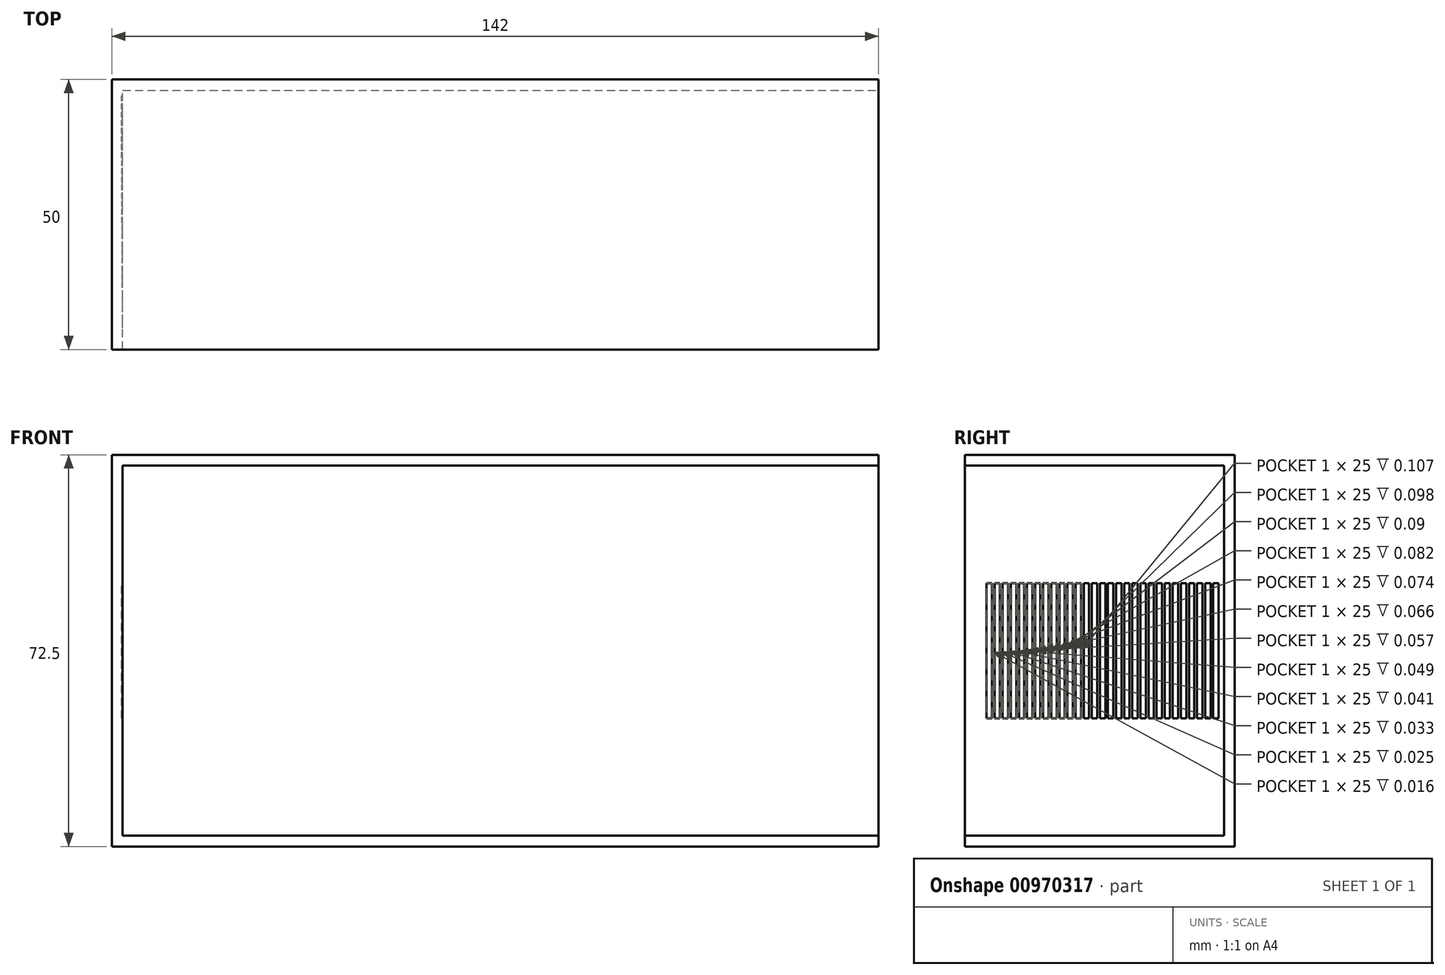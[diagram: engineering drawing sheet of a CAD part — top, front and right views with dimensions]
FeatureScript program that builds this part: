
annotation { "Feature Type Name" : "Feature", "Feature Type Description" : "" }
export const myFeature = defineFeature(function(context is Context, id is Id, definition is map)
    precondition{}
    {
        {
            var Q0;
            Q0=qCreatedBy(makeId("Front.planeOp"),FACE);
            var sketch = newSketch(context, id + "F0", { "sketchPlane" : qUnion([Q0])});
            skLineSegment(sketch, "E0.bottom", {"start": v(-71, -36.25) * mm, "end": v(71, -36.25) * mm});
            skLineSegment(sketch, "E0.top", {"start": v(-71, 36.25) * mm, "end": v(71, 36.25) * mm});
            skLineSegment(sketch, "E0.left", {"start": v(-71, -36.25) * mm, "end": v(-71, 36.25) * mm});
            skLineSegment(sketch, "E0.right", {"start": v(71, -36.25) * mm, "end": v(71, 36.25) * mm});
            skPoint(sketch, "E0.middle", {"position": v(0, 0) * mm});
            skSolve(sketch);
        }
        {
            var Q0;
            Q0=makeQuery(id+"F0.imprint","IMPRINT",FACE,{"disambiguationData":[TD([[makeQuery(id+"F0.imprint","IMPRINT",EDGE,{"derivedFrom":sQuery(id+"F0.wireOp",EDGE,"E0.bottom")}),1.0]])]});
            extrude(context, id + "F1", {"entities" : qUnion([Q0]), "depth" : 50 * mm, "offsetDistance" : 25 * mm});
        }
        {
            var Q0;
            Q0=makeQuery(id+"F1.opExtrude","SWEPT_FACE",FACE,{"disambiguationData":[OSD([sQuery(id+"F0.wireOp",EDGE,"E0.right")])]});
            shell(context, id + "F2", {"entities" : qUnion([Q0]), "thickness" : 2 * mm});
        }
        {
            var Q0;
            Q0=makeQuery(id+"F1.opExtrude","SWEPT_FACE",FACE,{"disambiguationData":[OSD([sQuery(id+"F0.wireOp",EDGE,"E0.right")])]});
            var sketch = newSketch(context, id + "F3", { "sketchPlane" : qUnion([Q0])});
            skLineSegment(sketch, "E1.0", {"start": v(-48, -34.25) * mm, "end": v(-48, 34.25) * mm});
            skLineSegment(sketch, "E2", {"start": v(-48, 34.25) * mm, "end": v(-50, 34.25) * mm});
            skLineSegment(sketch, "E3", {"start": v(-50, 34.25) * mm, "end": v(-50, -34.25) * mm});
            skLineSegment(sketch, "E4", {"start": v(-50, -34.25) * mm, "end": v(-48, -34.25) * mm});
            skSolve(sketch);
        }
        {
            var Q0;
            Q0=makeQuery(id+"F3.imprint","IMPRINT",FACE,{"disambiguationData":[TD([[makeQuery(id+"F3.imprint","IMPRINT",EDGE,{"derivedFrom":sQuery(id+"F3.wireOp",EDGE,"E1.0")}),1.0]])]});
            extrude(context, id + "F4", {"entities" : qUnion([Q0]), "operationType" : NewBodyOperationType.REMOVE, "oppositeDirection" : true, "depth" : 140 * mm, "offsetDistance" : 25 * mm});
        }
        {
            var Q0;
            Q0=qCreatedBy(makeId("Top.planeOp"),FACE);
            var sketch = newSketch(context, id + "F5", { "sketchPlane" : qUnion([Q0])});
            skLineSegment(sketch, "E5.top", {"start": v(-69, -49) * mm, "end": v(-68, -49) * mm});
            skLineSegment(sketch, "E6.bottom", {"start": v(-68, -49) * mm, "end": v(-69, -49) * mm});
            skLineSegment(sketch, "E6.top", {"start": v(-68, -48) * mm, "end": v(-69, -48) * mm});
            skLineSegment(sketch, "E6.left", {"start": v(-68, -49) * mm, "end": v(-68, -48) * mm});
            skLineSegment(sketch, "E6.right", {"start": v(-69, -49) * mm, "end": v(-69, -48) * mm});
            skLineSegment(sketch, "E7.0.1.0", {"start": v(-68, -47.5) * mm, "end": v(-69, -47.5) * mm});
            skLineSegment(sketch, "E7.0.1.1", {"start": v(-68, -46.5) * mm, "end": v(-69, -46.5) * mm});
            skLineSegment(sketch, "E7.0.1.2", {"start": v(-69, -47.5) * mm, "end": v(-68, -47.5) * mm});
            skLineSegment(sketch, "E7.0.1.3", {"start": v(-69, -47.5) * mm, "end": v(-69, -46.5) * mm});
            skLineSegment(sketch, "E7.0.1.4", {"start": v(-68, -47.5) * mm, "end": v(-68, -46.5) * mm});
            skLineSegment(sketch, "E7.0.2.0", {"start": v(-68.02, -46) * mm, "end": v(-69.02, -46) * mm});
            skLineSegment(sketch, "E7.0.2.1", {"start": v(-68.02, -45) * mm, "end": v(-69.02, -45) * mm});
            skLineSegment(sketch, "E7.0.2.2", {"start": v(-69.02, -46) * mm, "end": v(-68.02, -46) * mm});
            skLineSegment(sketch, "E7.0.2.3", {"start": v(-69.02, -46) * mm, "end": v(-69.02, -45) * mm});
            skLineSegment(sketch, "E7.0.2.4", {"start": v(-68.02, -46) * mm, "end": v(-68.02, -45) * mm});
            skLineSegment(sketch, "E7.0.3.0", {"start": v(-68.02, -44.5) * mm, "end": v(-69.02, -44.5) * mm});
            skLineSegment(sketch, "E7.0.3.1", {"start": v(-68.02, -43.5) * mm, "end": v(-69.02, -43.5) * mm});
            skLineSegment(sketch, "E7.0.3.2", {"start": v(-69.02, -44.5) * mm, "end": v(-68.02, -44.5) * mm});
            skLineSegment(sketch, "E7.0.3.3", {"start": v(-69.02, -44.5) * mm, "end": v(-69.02, -43.5) * mm});
            skLineSegment(sketch, "E7.0.3.4", {"start": v(-68.02, -44.5) * mm, "end": v(-68.02, -43.5) * mm});
            skLineSegment(sketch, "E7.0.4.0", {"start": v(-68.03, -43) * mm, "end": v(-69.03, -43) * mm});
            skLineSegment(sketch, "E7.0.4.1", {"start": v(-68.03, -42) * mm, "end": v(-69.03, -42) * mm});
            skLineSegment(sketch, "E7.0.4.2", {"start": v(-69.03, -43) * mm, "end": v(-68.03, -43) * mm});
            skLineSegment(sketch, "E7.0.4.3", {"start": v(-69.03, -43) * mm, "end": v(-69.03, -42) * mm});
            skLineSegment(sketch, "E7.0.4.4", {"start": v(-68.03, -43) * mm, "end": v(-68.03, -42) * mm});
            skLineSegment(sketch, "E7.0.5.0", {"start": v(-68.04, -41.5) * mm, "end": v(-69.04, -41.5) * mm});
            skLineSegment(sketch, "E7.0.5.1", {"start": v(-68.04, -40.5) * mm, "end": v(-69.04, -40.5) * mm});
            skLineSegment(sketch, "E7.0.5.2", {"start": v(-69.04, -41.5) * mm, "end": v(-68.04, -41.5) * mm});
            skLineSegment(sketch, "E7.0.5.3", {"start": v(-69.04, -41.5) * mm, "end": v(-69.04, -40.5) * mm});
            skLineSegment(sketch, "E7.0.5.4", {"start": v(-68.04, -41.5) * mm, "end": v(-68.04, -40.5) * mm});
            skLineSegment(sketch, "E7.0.6.0", {"start": v(-68.05, -40) * mm, "end": v(-69.05, -40) * mm});
            skLineSegment(sketch, "E7.0.6.1", {"start": v(-68.05, -39) * mm, "end": v(-69.05, -39) * mm});
            skLineSegment(sketch, "E7.0.6.2", {"start": v(-69.05, -40) * mm, "end": v(-68.05, -40) * mm});
            skLineSegment(sketch, "E7.0.6.3", {"start": v(-69.05, -40) * mm, "end": v(-69.05, -39) * mm});
            skLineSegment(sketch, "E7.0.6.4", {"start": v(-68.05, -40) * mm, "end": v(-68.05, -39) * mm});
            skLineSegment(sketch, "E7.0.7.0", {"start": v(-68.06, -38.5) * mm, "end": v(-69.06, -38.5) * mm});
            skLineSegment(sketch, "E7.0.7.1", {"start": v(-68.06, -37.5) * mm, "end": v(-69.06, -37.5) * mm});
            skLineSegment(sketch, "E7.0.7.2", {"start": v(-69.06, -38.5) * mm, "end": v(-68.06, -38.5) * mm});
            skLineSegment(sketch, "E7.0.7.3", {"start": v(-69.06, -38.5) * mm, "end": v(-69.06, -37.5) * mm});
            skLineSegment(sketch, "E7.0.7.4", {"start": v(-68.06, -38.5) * mm, "end": v(-68.06, -37.5) * mm});
            skLineSegment(sketch, "E7.0.8.0", {"start": v(-68.07, -37) * mm, "end": v(-69.07, -37) * mm});
            skLineSegment(sketch, "E7.0.8.1", {"start": v(-68.07, -36) * mm, "end": v(-69.07, -36) * mm});
            skLineSegment(sketch, "E7.0.8.2", {"start": v(-69.07, -37) * mm, "end": v(-68.07, -37) * mm});
            skLineSegment(sketch, "E7.0.8.3", {"start": v(-69.07, -37) * mm, "end": v(-69.07, -36) * mm});
            skLineSegment(sketch, "E7.0.8.4", {"start": v(-68.07, -37) * mm, "end": v(-68.07, -36) * mm});
            skLineSegment(sketch, "E7.0.9.0", {"start": v(-68.07, -35.5) * mm, "end": v(-69.07, -35.5) * mm});
            skLineSegment(sketch, "E7.0.9.1", {"start": v(-68.07, -34.5) * mm, "end": v(-69.07, -34.5) * mm});
            skLineSegment(sketch, "E7.0.9.2", {"start": v(-69.07, -35.5) * mm, "end": v(-68.07, -35.5) * mm});
            skLineSegment(sketch, "E7.0.9.3", {"start": v(-69.07, -35.5) * mm, "end": v(-69.07, -34.5) * mm});
            skLineSegment(sketch, "E7.0.9.4", {"start": v(-68.07, -35.5) * mm, "end": v(-68.07, -34.5) * mm});
            skLineSegment(sketch, "E7.0.10.0", {"start": v(-68.08, -34) * mm, "end": v(-69.08, -34) * mm});
            skLineSegment(sketch, "E7.0.10.1", {"start": v(-68.08, -33) * mm, "end": v(-69.08, -33) * mm});
            skLineSegment(sketch, "E7.0.10.2", {"start": v(-69.08, -34) * mm, "end": v(-68.08, -34) * mm});
            skLineSegment(sketch, "E7.0.10.3", {"start": v(-69.08, -34) * mm, "end": v(-69.08, -33) * mm});
            skLineSegment(sketch, "E7.0.10.4", {"start": v(-68.08, -34) * mm, "end": v(-68.08, -33) * mm});
            skLineSegment(sketch, "E7.0.11.0", {"start": v(-68.1, -32.5) * mm, "end": v(-69.1, -32.5) * mm});
            skLineSegment(sketch, "E7.0.11.1", {"start": v(-68.1, -31.5) * mm, "end": v(-69.1, -31.5) * mm});
            skLineSegment(sketch, "E7.0.11.2", {"start": v(-69.1, -32.5) * mm, "end": v(-68.1, -32.5) * mm});
            skLineSegment(sketch, "E7.0.11.3", {"start": v(-69.1, -32.5) * mm, "end": v(-69.1, -31.5) * mm});
            skLineSegment(sketch, "E7.0.11.4", {"start": v(-68.1, -32.5) * mm, "end": v(-68.1, -31.5) * mm});
            skLineSegment(sketch, "E7.0.12.0", {"start": v(-68.1, -31) * mm, "end": v(-69.1, -31) * mm});
            skLineSegment(sketch, "E7.0.12.1", {"start": v(-68.1, -30) * mm, "end": v(-69.1, -30) * mm});
            skLineSegment(sketch, "E7.0.12.2", {"start": v(-69.1, -31) * mm, "end": v(-68.1, -31) * mm});
            skLineSegment(sketch, "E7.0.12.3", {"start": v(-69.1, -31) * mm, "end": v(-69.1, -30) * mm});
            skLineSegment(sketch, "E7.0.12.4", {"start": v(-68.1, -31) * mm, "end": v(-68.1, -30) * mm});
            skLineSegment(sketch, "E7.0.13.0", {"start": v(-68.1, -29.5) * mm, "end": v(-69.1, -29.5) * mm});
            skLineSegment(sketch, "E7.0.13.1", {"start": v(-68.1, -28.5) * mm, "end": v(-69.1, -28.5) * mm});
            skLineSegment(sketch, "E7.0.13.2", {"start": v(-69.1, -29.5) * mm, "end": v(-68.1, -29.5) * mm});
            skLineSegment(sketch, "E7.0.13.3", {"start": v(-69.1, -29.5) * mm, "end": v(-69.1, -28.5) * mm});
            skLineSegment(sketch, "E7.0.13.4", {"start": v(-68.1, -29.5) * mm, "end": v(-68.1, -28.5) * mm});
            skLineSegment(sketch, "E7.0.14.0", {"start": v(-68.11, -28) * mm, "end": v(-69.11, -28) * mm});
            skLineSegment(sketch, "E7.0.14.1", {"start": v(-68.11, -27) * mm, "end": v(-69.11, -27) * mm});
            skLineSegment(sketch, "E7.0.14.2", {"start": v(-69.11, -28) * mm, "end": v(-68.11, -28) * mm});
            skLineSegment(sketch, "E7.0.14.3", {"start": v(-69.11, -28) * mm, "end": v(-69.11, -27) * mm});
            skLineSegment(sketch, "E7.0.14.4", {"start": v(-68.11, -28) * mm, "end": v(-68.11, -27) * mm});
            skLineSegment(sketch, "E7.0.15.0", {"start": v(-68.12, -26.5) * mm, "end": v(-69.12, -26.5) * mm});
            skLineSegment(sketch, "E7.0.15.1", {"start": v(-68.12, -25.5) * mm, "end": v(-69.12, -25.5) * mm});
            skLineSegment(sketch, "E7.0.15.2", {"start": v(-69.12, -26.5) * mm, "end": v(-68.12, -26.5) * mm});
            skLineSegment(sketch, "E7.0.15.3", {"start": v(-69.12, -26.5) * mm, "end": v(-69.12, -25.5) * mm});
            skLineSegment(sketch, "E7.0.15.4", {"start": v(-68.12, -26.5) * mm, "end": v(-68.12, -25.5) * mm});
            skLineSegment(sketch, "E7.0.16.0", {"start": v(-68.13, -25) * mm, "end": v(-69.13, -25) * mm});
            skLineSegment(sketch, "E7.0.16.1", {"start": v(-68.13, -24) * mm, "end": v(-69.13, -24) * mm});
            skLineSegment(sketch, "E7.0.16.2", {"start": v(-69.13, -25) * mm, "end": v(-68.13, -25) * mm});
            skLineSegment(sketch, "E7.0.16.3", {"start": v(-69.13, -25) * mm, "end": v(-69.13, -24) * mm});
            skLineSegment(sketch, "E7.0.16.4", {"start": v(-68.13, -25) * mm, "end": v(-68.13, -24) * mm});
            skLineSegment(sketch, "E7.0.17.0", {"start": v(-68.14, -23.5) * mm, "end": v(-69.14, -23.5) * mm});
            skLineSegment(sketch, "E7.0.17.1", {"start": v(-68.14, -22.5) * mm, "end": v(-69.14, -22.5) * mm});
            skLineSegment(sketch, "E7.0.17.2", {"start": v(-69.14, -23.5) * mm, "end": v(-68.14, -23.5) * mm});
            skLineSegment(sketch, "E7.0.17.3", {"start": v(-69.14, -23.5) * mm, "end": v(-69.14, -22.5) * mm});
            skLineSegment(sketch, "E7.0.17.4", {"start": v(-68.14, -23.5) * mm, "end": v(-68.14, -22.5) * mm});
            skLineSegment(sketch, "E7.0.18.0", {"start": v(-68.15, -22) * mm, "end": v(-69.15, -22) * mm});
            skLineSegment(sketch, "E7.0.18.1", {"start": v(-68.15, -21) * mm, "end": v(-69.15, -21) * mm});
            skLineSegment(sketch, "E7.0.18.2", {"start": v(-69.15, -22) * mm, "end": v(-68.15, -22) * mm});
            skLineSegment(sketch, "E7.0.18.3", {"start": v(-69.15, -22) * mm, "end": v(-69.15, -21) * mm});
            skLineSegment(sketch, "E7.0.18.4", {"start": v(-68.15, -22) * mm, "end": v(-68.15, -21) * mm});
            skLineSegment(sketch, "E7.0.19.0", {"start": v(-68.16, -20.5) * mm, "end": v(-69.16, -20.5) * mm});
            skLineSegment(sketch, "E7.0.19.1", {"start": v(-68.16, -19.5) * mm, "end": v(-69.16, -19.5) * mm});
            skLineSegment(sketch, "E7.0.19.2", {"start": v(-69.16, -20.5) * mm, "end": v(-68.16, -20.5) * mm});
            skLineSegment(sketch, "E7.0.19.3", {"start": v(-69.16, -20.5) * mm, "end": v(-69.16, -19.5) * mm});
            skLineSegment(sketch, "E7.0.19.4", {"start": v(-68.16, -20.5) * mm, "end": v(-68.16, -19.5) * mm});
            skLineSegment(sketch, "E7.0.20.0", {"start": v(-68.16, -19) * mm, "end": v(-69.16, -19) * mm});
            skLineSegment(sketch, "E7.0.20.1", {"start": v(-68.16, -18) * mm, "end": v(-69.16, -18) * mm});
            skLineSegment(sketch, "E7.0.20.2", {"start": v(-69.16, -19) * mm, "end": v(-68.16, -19) * mm});
            skLineSegment(sketch, "E7.0.20.3", {"start": v(-69.16, -19) * mm, "end": v(-69.16, -18) * mm});
            skLineSegment(sketch, "E7.0.20.4", {"start": v(-68.16, -19) * mm, "end": v(-68.16, -18) * mm});
            skLineSegment(sketch, "E7.0.21.0", {"start": v(-68.17, -17.5) * mm, "end": v(-69.17, -17.5) * mm});
            skLineSegment(sketch, "E7.0.21.1", {"start": v(-68.17, -16.5) * mm, "end": v(-69.17, -16.5) * mm});
            skLineSegment(sketch, "E7.0.21.2", {"start": v(-69.17, -17.5) * mm, "end": v(-68.17, -17.5) * mm});
            skLineSegment(sketch, "E7.0.21.3", {"start": v(-69.17, -17.5) * mm, "end": v(-69.17, -16.5) * mm});
            skLineSegment(sketch, "E7.0.21.4", {"start": v(-68.17, -17.5) * mm, "end": v(-68.17, -16.5) * mm});
            skLineSegment(sketch, "E7.0.22.0", {"start": v(-68.18, -16) * mm, "end": v(-69.18, -16) * mm});
            skLineSegment(sketch, "E7.0.22.1", {"start": v(-68.18, -15) * mm, "end": v(-69.18, -15) * mm});
            skLineSegment(sketch, "E7.0.22.2", {"start": v(-69.18, -16) * mm, "end": v(-68.18, -16) * mm});
            skLineSegment(sketch, "E7.0.22.3", {"start": v(-69.18, -16) * mm, "end": v(-69.18, -15) * mm});
            skLineSegment(sketch, "E7.0.22.4", {"start": v(-68.18, -16) * mm, "end": v(-68.18, -15) * mm});
            skLineSegment(sketch, "E7.0.23.0", {"start": v(-68.19, -14.5) * mm, "end": v(-69.19, -14.5) * mm});
            skLineSegment(sketch, "E7.0.23.1", {"start": v(-68.19, -13.5) * mm, "end": v(-69.19, -13.5) * mm});
            skLineSegment(sketch, "E7.0.23.2", {"start": v(-69.19, -14.5) * mm, "end": v(-68.19, -14.5) * mm});
            skLineSegment(sketch, "E7.0.23.3", {"start": v(-69.19, -14.5) * mm, "end": v(-69.19, -13.5) * mm});
            skLineSegment(sketch, "E7.0.23.4", {"start": v(-68.19, -14.5) * mm, "end": v(-68.19, -13.5) * mm});
            skLineSegment(sketch, "E7.0.24.0", {"start": v(-68.2, -13) * mm, "end": v(-69.2, -13) * mm});
            skLineSegment(sketch, "E7.0.24.1", {"start": v(-68.2, -12) * mm, "end": v(-69.2, -12) * mm});
            skLineSegment(sketch, "E7.0.24.2", {"start": v(-69.2, -13) * mm, "end": v(-68.2, -13) * mm});
            skLineSegment(sketch, "E7.0.24.3", {"start": v(-69.2, -13) * mm, "end": v(-69.2, -12) * mm});
            skLineSegment(sketch, "E7.0.24.4", {"start": v(-68.2, -13) * mm, "end": v(-68.2, -12) * mm});
            skLineSegment(sketch, "E7.0.25.0", {"start": v(-68.2, -11.5) * mm, "end": v(-69.2, -11.5) * mm});
            skLineSegment(sketch, "E7.0.25.1", {"start": v(-68.2, -10.5) * mm, "end": v(-69.2, -10.5) * mm});
            skLineSegment(sketch, "E7.0.25.2", {"start": v(-69.2, -11.5) * mm, "end": v(-68.2, -11.5) * mm});
            skLineSegment(sketch, "E7.0.25.3", {"start": v(-69.2, -11.5) * mm, "end": v(-69.2, -10.5) * mm});
            skLineSegment(sketch, "E7.0.25.4", {"start": v(-68.2, -11.5) * mm, "end": v(-68.2, -10.5) * mm});
            skLineSegment(sketch, "E7.0.26.0", {"start": v(-68.21, -10) * mm, "end": v(-69.21, -10) * mm});
            skLineSegment(sketch, "E7.0.26.1", {"start": v(-68.21, -9) * mm, "end": v(-69.21, -9) * mm});
            skLineSegment(sketch, "E7.0.26.2", {"start": v(-69.21, -10) * mm, "end": v(-68.21, -10) * mm});
            skLineSegment(sketch, "E7.0.26.3", {"start": v(-69.21, -10) * mm, "end": v(-69.21, -9) * mm});
            skLineSegment(sketch, "E7.0.26.4", {"start": v(-68.21, -10) * mm, "end": v(-68.21, -9) * mm});
            skLineSegment(sketch, "E7.0.27.0", {"start": v(-68.22, -8.5) * mm, "end": v(-69.22, -8.5) * mm});
            skLineSegment(sketch, "E7.0.27.1", {"start": v(-68.22, -7.5) * mm, "end": v(-69.22, -7.5) * mm});
            skLineSegment(sketch, "E7.0.27.2", {"start": v(-69.22, -8.5) * mm, "end": v(-68.22, -8.5) * mm});
            skLineSegment(sketch, "E7.0.27.3", {"start": v(-69.22, -8.5) * mm, "end": v(-69.22, -7.5) * mm});
            skLineSegment(sketch, "E7.0.27.4", {"start": v(-68.22, -8.5) * mm, "end": v(-68.22, -7.5) * mm});
            skLineSegment(sketch, "E7.0.28.0", {"start": v(-68.23, -7) * mm, "end": v(-69.23, -7) * mm});
            skLineSegment(sketch, "E7.0.28.1", {"start": v(-68.23, -6) * mm, "end": v(-69.23, -6) * mm});
            skLineSegment(sketch, "E7.0.28.2", {"start": v(-69.23, -7) * mm, "end": v(-68.23, -7) * mm});
            skLineSegment(sketch, "E7.0.28.3", {"start": v(-69.23, -7) * mm, "end": v(-69.23, -6) * mm});
            skLineSegment(sketch, "E7.0.28.4", {"start": v(-68.23, -7) * mm, "end": v(-68.23, -6) * mm});
            skLineSegment(sketch, "E7.0.29.0", {"start": v(-68.24, -5.5) * mm, "end": v(-69.24, -5.5) * mm});
            skLineSegment(sketch, "E7.0.29.1", {"start": v(-68.24, -4.5) * mm, "end": v(-69.24, -4.5) * mm});
            skLineSegment(sketch, "E7.0.29.2", {"start": v(-69.24, -5.5) * mm, "end": v(-68.24, -5.5) * mm});
            skLineSegment(sketch, "E7.0.29.3", {"start": v(-69.24, -5.5) * mm, "end": v(-69.24, -4.5) * mm});
            skLineSegment(sketch, "E7.0.29.4", {"start": v(-68.24, -5.5) * mm, "end": v(-68.24, -4.5) * mm});
            skLineSegment(sketch, "E7.0.30.0", {"start": v(-68.25, -4) * mm, "end": v(-69.25, -4) * mm});
            skLineSegment(sketch, "E7.0.30.1", {"start": v(-68.25, -3) * mm, "end": v(-69.25, -3) * mm});
            skLineSegment(sketch, "E7.0.30.2", {"start": v(-69.25, -4) * mm, "end": v(-68.25, -4) * mm});
            skLineSegment(sketch, "E7.0.30.3", {"start": v(-69.25, -4) * mm, "end": v(-69.25, -3) * mm});
            skLineSegment(sketch, "E7.0.30.4", {"start": v(-68.25, -4) * mm, "end": v(-68.25, -3) * mm});
            skLineSegment(sketch, "E7.1.0.0", {"start": v(-66.5, -49) * mm, "end": v(-67.5, -49) * mm});
            skLineSegment(sketch, "E7.1.0.1", {"start": v(-66.5, -48) * mm, "end": v(-67.5, -48) * mm});
            skLineSegment(sketch, "E7.1.0.2", {"start": v(-67.5, -49) * mm, "end": v(-66.5, -49) * mm});
            skLineSegment(sketch, "E7.1.0.3", {"start": v(-67.5, -49) * mm, "end": v(-67.5, -48) * mm});
            skLineSegment(sketch, "E7.1.0.4", {"start": v(-66.5, -49) * mm, "end": v(-66.5, -48) * mm});
            skLineSegment(sketch, "E7.1.1.0", {"start": v(-66.5, -47.5) * mm, "end": v(-67.5, -47.5) * mm});
            skLineSegment(sketch, "E7.1.1.1", {"start": v(-66.5, -46.5) * mm, "end": v(-67.5, -46.5) * mm});
            skLineSegment(sketch, "E7.1.1.2", {"start": v(-67.5, -47.5) * mm, "end": v(-66.5, -47.5) * mm});
            skLineSegment(sketch, "E7.1.1.3", {"start": v(-67.5, -47.5) * mm, "end": v(-67.5, -46.5) * mm});
            skLineSegment(sketch, "E7.1.1.4", {"start": v(-66.5, -47.5) * mm, "end": v(-66.5, -46.5) * mm});
            skLineSegment(sketch, "E7.1.2.0", {"start": v(-66.52, -46) * mm, "end": v(-67.52, -46) * mm});
            skLineSegment(sketch, "E7.1.2.1", {"start": v(-66.52, -45) * mm, "end": v(-67.52, -45) * mm});
            skLineSegment(sketch, "E7.1.2.2", {"start": v(-67.52, -46) * mm, "end": v(-66.52, -46) * mm});
            skLineSegment(sketch, "E7.1.2.3", {"start": v(-67.52, -46) * mm, "end": v(-67.52, -45) * mm});
            skLineSegment(sketch, "E7.1.2.4", {"start": v(-66.52, -46) * mm, "end": v(-66.52, -45) * mm});
            skLineSegment(sketch, "E7.1.3.0", {"start": v(-66.52, -44.5) * mm, "end": v(-67.52, -44.5) * mm});
            skLineSegment(sketch, "E7.1.3.1", {"start": v(-66.52, -43.5) * mm, "end": v(-67.52, -43.5) * mm});
            skLineSegment(sketch, "E7.1.3.2", {"start": v(-67.52, -44.5) * mm, "end": v(-66.52, -44.5) * mm});
            skLineSegment(sketch, "E7.1.3.3", {"start": v(-67.52, -44.5) * mm, "end": v(-67.52, -43.5) * mm});
            skLineSegment(sketch, "E7.1.3.4", {"start": v(-66.52, -44.5) * mm, "end": v(-66.52, -43.5) * mm});
            skLineSegment(sketch, "E7.1.4.0", {"start": v(-66.53, -43) * mm, "end": v(-67.53, -43) * mm});
            skLineSegment(sketch, "E7.1.4.1", {"start": v(-66.53, -42) * mm, "end": v(-67.53, -42) * mm});
            skLineSegment(sketch, "E7.1.4.2", {"start": v(-67.53, -43) * mm, "end": v(-66.53, -43) * mm});
            skLineSegment(sketch, "E7.1.4.3", {"start": v(-67.53, -43) * mm, "end": v(-67.53, -42) * mm});
            skLineSegment(sketch, "E7.1.4.4", {"start": v(-66.53, -43) * mm, "end": v(-66.53, -42) * mm});
            skLineSegment(sketch, "E7.1.5.0", {"start": v(-66.54, -41.5) * mm, "end": v(-67.54, -41.5) * mm});
            skLineSegment(sketch, "E7.1.5.1", {"start": v(-66.54, -40.5) * mm, "end": v(-67.54, -40.5) * mm});
            skLineSegment(sketch, "E7.1.5.2", {"start": v(-67.54, -41.5) * mm, "end": v(-66.54, -41.5) * mm});
            skLineSegment(sketch, "E7.1.5.3", {"start": v(-67.54, -41.5) * mm, "end": v(-67.54, -40.5) * mm});
            skLineSegment(sketch, "E7.1.5.4", {"start": v(-66.54, -41.5) * mm, "end": v(-66.54, -40.5) * mm});
            skLineSegment(sketch, "E7.1.6.0", {"start": v(-66.55, -40) * mm, "end": v(-67.55, -40) * mm});
            skLineSegment(sketch, "E7.1.6.1", {"start": v(-66.55, -39) * mm, "end": v(-67.55, -39) * mm});
            skLineSegment(sketch, "E7.1.6.2", {"start": v(-67.55, -40) * mm, "end": v(-66.55, -40) * mm});
            skLineSegment(sketch, "E7.1.6.3", {"start": v(-67.55, -40) * mm, "end": v(-67.55, -39) * mm});
            skLineSegment(sketch, "E7.1.6.4", {"start": v(-66.55, -40) * mm, "end": v(-66.55, -39) * mm});
            skLineSegment(sketch, "E7.1.7.0", {"start": v(-66.56, -38.5) * mm, "end": v(-67.56, -38.5) * mm});
            skLineSegment(sketch, "E7.1.7.1", {"start": v(-66.56, -37.5) * mm, "end": v(-67.56, -37.5) * mm});
            skLineSegment(sketch, "E7.1.7.2", {"start": v(-67.56, -38.5) * mm, "end": v(-66.56, -38.5) * mm});
            skLineSegment(sketch, "E7.1.7.3", {"start": v(-67.56, -38.5) * mm, "end": v(-67.56, -37.5) * mm});
            skLineSegment(sketch, "E7.1.7.4", {"start": v(-66.56, -38.5) * mm, "end": v(-66.56, -37.5) * mm});
            skLineSegment(sketch, "E7.1.8.0", {"start": v(-66.57, -37) * mm, "end": v(-67.57, -37) * mm});
            skLineSegment(sketch, "E7.1.8.1", {"start": v(-66.57, -36) * mm, "end": v(-67.57, -36) * mm});
            skLineSegment(sketch, "E7.1.8.2", {"start": v(-67.57, -37) * mm, "end": v(-66.57, -37) * mm});
            skLineSegment(sketch, "E7.1.8.3", {"start": v(-67.57, -37) * mm, "end": v(-67.57, -36) * mm});
            skLineSegment(sketch, "E7.1.8.4", {"start": v(-66.57, -37) * mm, "end": v(-66.57, -36) * mm});
            skLineSegment(sketch, "E7.1.9.0", {"start": v(-66.57, -35.5) * mm, "end": v(-67.57, -35.5) * mm});
            skLineSegment(sketch, "E7.1.9.1", {"start": v(-66.57, -34.5) * mm, "end": v(-67.57, -34.5) * mm});
            skLineSegment(sketch, "E7.1.9.2", {"start": v(-67.57, -35.5) * mm, "end": v(-66.57, -35.5) * mm});
            skLineSegment(sketch, "E7.1.9.3", {"start": v(-67.57, -35.5) * mm, "end": v(-67.57, -34.5) * mm});
            skLineSegment(sketch, "E7.1.9.4", {"start": v(-66.57, -35.5) * mm, "end": v(-66.57, -34.5) * mm});
            skLineSegment(sketch, "E7.1.10.0", {"start": v(-66.58, -34) * mm, "end": v(-67.58, -34) * mm});
            skLineSegment(sketch, "E7.1.10.1", {"start": v(-66.58, -33) * mm, "end": v(-67.58, -33) * mm});
            skLineSegment(sketch, "E7.1.10.2", {"start": v(-67.58, -34) * mm, "end": v(-66.58, -34) * mm});
            skLineSegment(sketch, "E7.1.10.3", {"start": v(-67.58, -34) * mm, "end": v(-67.58, -33) * mm});
            skLineSegment(sketch, "E7.1.10.4", {"start": v(-66.58, -34) * mm, "end": v(-66.58, -33) * mm});
            skLineSegment(sketch, "E7.1.11.0", {"start": v(-66.6, -32.5) * mm, "end": v(-67.6, -32.5) * mm});
            skLineSegment(sketch, "E7.1.11.1", {"start": v(-66.6, -31.5) * mm, "end": v(-67.6, -31.5) * mm});
            skLineSegment(sketch, "E7.1.11.2", {"start": v(-67.6, -32.5) * mm, "end": v(-66.6, -32.5) * mm});
            skLineSegment(sketch, "E7.1.11.3", {"start": v(-67.6, -32.5) * mm, "end": v(-67.6, -31.5) * mm});
            skLineSegment(sketch, "E7.1.11.4", {"start": v(-66.6, -32.5) * mm, "end": v(-66.6, -31.5) * mm});
            skLineSegment(sketch, "E7.1.12.0", {"start": v(-66.6, -31) * mm, "end": v(-67.6, -31) * mm});
            skLineSegment(sketch, "E7.1.12.1", {"start": v(-66.6, -30) * mm, "end": v(-67.6, -30) * mm});
            skLineSegment(sketch, "E7.1.12.2", {"start": v(-67.6, -31) * mm, "end": v(-66.6, -31) * mm});
            skLineSegment(sketch, "E7.1.12.3", {"start": v(-67.6, -31) * mm, "end": v(-67.6, -30) * mm});
            skLineSegment(sketch, "E7.1.12.4", {"start": v(-66.6, -31) * mm, "end": v(-66.6, -30) * mm});
            skLineSegment(sketch, "E7.1.13.0", {"start": v(-66.6, -29.5) * mm, "end": v(-67.6, -29.5) * mm});
            skLineSegment(sketch, "E7.1.13.1", {"start": v(-66.6, -28.5) * mm, "end": v(-67.6, -28.5) * mm});
            skLineSegment(sketch, "E7.1.13.2", {"start": v(-67.6, -29.5) * mm, "end": v(-66.6, -29.5) * mm});
            skLineSegment(sketch, "E7.1.13.3", {"start": v(-67.6, -29.5) * mm, "end": v(-67.6, -28.5) * mm});
            skLineSegment(sketch, "E7.1.13.4", {"start": v(-66.6, -29.5) * mm, "end": v(-66.6, -28.5) * mm});
            skLineSegment(sketch, "E7.1.14.0", {"start": v(-66.61, -28) * mm, "end": v(-67.61, -28) * mm});
            skLineSegment(sketch, "E7.1.14.1", {"start": v(-66.61, -27) * mm, "end": v(-67.61, -27) * mm});
            skLineSegment(sketch, "E7.1.14.2", {"start": v(-67.61, -28) * mm, "end": v(-66.61, -28) * mm});
            skLineSegment(sketch, "E7.1.14.3", {"start": v(-67.61, -28) * mm, "end": v(-67.61, -27) * mm});
            skLineSegment(sketch, "E7.1.14.4", {"start": v(-66.61, -28) * mm, "end": v(-66.61, -27) * mm});
            skLineSegment(sketch, "E7.1.15.0", {"start": v(-66.62, -26.5) * mm, "end": v(-67.62, -26.5) * mm});
            skLineSegment(sketch, "E7.1.15.1", {"start": v(-66.62, -25.5) * mm, "end": v(-67.62, -25.5) * mm});
            skLineSegment(sketch, "E7.1.15.2", {"start": v(-67.62, -26.5) * mm, "end": v(-66.62, -26.5) * mm});
            skLineSegment(sketch, "E7.1.15.3", {"start": v(-67.62, -26.5) * mm, "end": v(-67.62, -25.5) * mm});
            skLineSegment(sketch, "E7.1.15.4", {"start": v(-66.62, -26.5) * mm, "end": v(-66.62, -25.5) * mm});
            skLineSegment(sketch, "E7.1.16.0", {"start": v(-66.63, -25) * mm, "end": v(-67.63, -25) * mm});
            skLineSegment(sketch, "E7.1.16.1", {"start": v(-66.63, -24) * mm, "end": v(-67.63, -24) * mm});
            skLineSegment(sketch, "E7.1.16.2", {"start": v(-67.63, -25) * mm, "end": v(-66.63, -25) * mm});
            skLineSegment(sketch, "E7.1.16.3", {"start": v(-67.63, -25) * mm, "end": v(-67.63, -24) * mm});
            skLineSegment(sketch, "E7.1.16.4", {"start": v(-66.63, -25) * mm, "end": v(-66.63, -24) * mm});
            skLineSegment(sketch, "E7.1.17.0", {"start": v(-66.64, -23.5) * mm, "end": v(-67.64, -23.5) * mm});
            skLineSegment(sketch, "E7.1.17.1", {"start": v(-66.64, -22.5) * mm, "end": v(-67.64, -22.5) * mm});
            skLineSegment(sketch, "E7.1.17.2", {"start": v(-67.64, -23.5) * mm, "end": v(-66.64, -23.5) * mm});
            skLineSegment(sketch, "E7.1.17.3", {"start": v(-67.64, -23.5) * mm, "end": v(-67.64, -22.5) * mm});
            skLineSegment(sketch, "E7.1.17.4", {"start": v(-66.64, -23.5) * mm, "end": v(-66.64, -22.5) * mm});
            skLineSegment(sketch, "E7.1.18.0", {"start": v(-66.65, -22) * mm, "end": v(-67.65, -22) * mm});
            skLineSegment(sketch, "E7.1.18.1", {"start": v(-66.65, -21) * mm, "end": v(-67.65, -21) * mm});
            skLineSegment(sketch, "E7.1.18.2", {"start": v(-67.65, -22) * mm, "end": v(-66.65, -22) * mm});
            skLineSegment(sketch, "E7.1.18.3", {"start": v(-67.65, -22) * mm, "end": v(-67.65, -21) * mm});
            skLineSegment(sketch, "E7.1.18.4", {"start": v(-66.65, -22) * mm, "end": v(-66.65, -21) * mm});
            skLineSegment(sketch, "E7.1.19.0", {"start": v(-66.66, -20.5) * mm, "end": v(-67.66, -20.5) * mm});
            skLineSegment(sketch, "E7.1.19.1", {"start": v(-66.66, -19.5) * mm, "end": v(-67.66, -19.5) * mm});
            skLineSegment(sketch, "E7.1.19.2", {"start": v(-67.66, -20.5) * mm, "end": v(-66.66, -20.5) * mm});
            skLineSegment(sketch, "E7.1.19.3", {"start": v(-67.66, -20.5) * mm, "end": v(-67.66, -19.5) * mm});
            skLineSegment(sketch, "E7.1.19.4", {"start": v(-66.66, -20.5) * mm, "end": v(-66.66, -19.5) * mm});
            skLineSegment(sketch, "E7.1.20.0", {"start": v(-66.66, -19) * mm, "end": v(-67.66, -19) * mm});
            skLineSegment(sketch, "E7.1.20.1", {"start": v(-66.66, -18) * mm, "end": v(-67.66, -18) * mm});
            skLineSegment(sketch, "E7.1.20.2", {"start": v(-67.66, -19) * mm, "end": v(-66.66, -19) * mm});
            skLineSegment(sketch, "E7.1.20.3", {"start": v(-67.66, -19) * mm, "end": v(-67.66, -18) * mm});
            skLineSegment(sketch, "E7.1.20.4", {"start": v(-66.66, -19) * mm, "end": v(-66.66, -18) * mm});
            skLineSegment(sketch, "E7.1.21.0", {"start": v(-66.67, -17.5) * mm, "end": v(-67.67, -17.5) * mm});
            skLineSegment(sketch, "E7.1.21.1", {"start": v(-66.67, -16.5) * mm, "end": v(-67.67, -16.5) * mm});
            skLineSegment(sketch, "E7.1.21.2", {"start": v(-67.67, -17.5) * mm, "end": v(-66.67, -17.5) * mm});
            skLineSegment(sketch, "E7.1.21.3", {"start": v(-67.67, -17.5) * mm, "end": v(-67.67, -16.5) * mm});
            skLineSegment(sketch, "E7.1.21.4", {"start": v(-66.67, -17.5) * mm, "end": v(-66.67, -16.5) * mm});
            skLineSegment(sketch, "E7.1.22.0", {"start": v(-66.68, -16) * mm, "end": v(-67.68, -16) * mm});
            skLineSegment(sketch, "E7.1.22.1", {"start": v(-66.68, -15) * mm, "end": v(-67.68, -15) * mm});
            skLineSegment(sketch, "E7.1.22.2", {"start": v(-67.68, -16) * mm, "end": v(-66.68, -16) * mm});
            skLineSegment(sketch, "E7.1.22.3", {"start": v(-67.68, -16) * mm, "end": v(-67.68, -15) * mm});
            skLineSegment(sketch, "E7.1.22.4", {"start": v(-66.68, -16) * mm, "end": v(-66.68, -15) * mm});
            skLineSegment(sketch, "E7.1.23.0", {"start": v(-66.69, -14.5) * mm, "end": v(-67.69, -14.5) * mm});
            skLineSegment(sketch, "E7.1.23.1", {"start": v(-66.69, -13.5) * mm, "end": v(-67.69, -13.5) * mm});
            skLineSegment(sketch, "E7.1.23.2", {"start": v(-67.69, -14.5) * mm, "end": v(-66.69, -14.5) * mm});
            skLineSegment(sketch, "E7.1.23.3", {"start": v(-67.69, -14.5) * mm, "end": v(-67.69, -13.5) * mm});
            skLineSegment(sketch, "E7.1.23.4", {"start": v(-66.69, -14.5) * mm, "end": v(-66.69, -13.5) * mm});
            skLineSegment(sketch, "E7.1.24.0", {"start": v(-66.7, -13) * mm, "end": v(-67.7, -13) * mm});
            skLineSegment(sketch, "E7.1.24.1", {"start": v(-66.7, -12) * mm, "end": v(-67.7, -12) * mm});
            skLineSegment(sketch, "E7.1.24.2", {"start": v(-67.7, -13) * mm, "end": v(-66.7, -13) * mm});
            skLineSegment(sketch, "E7.1.24.3", {"start": v(-67.7, -13) * mm, "end": v(-67.7, -12) * mm});
            skLineSegment(sketch, "E7.1.24.4", {"start": v(-66.7, -13) * mm, "end": v(-66.7, -12) * mm});
            skLineSegment(sketch, "E7.1.25.0", {"start": v(-66.7, -11.5) * mm, "end": v(-67.7, -11.5) * mm});
            skLineSegment(sketch, "E7.1.25.1", {"start": v(-66.7, -10.5) * mm, "end": v(-67.7, -10.5) * mm});
            skLineSegment(sketch, "E7.1.25.2", {"start": v(-67.7, -11.5) * mm, "end": v(-66.7, -11.5) * mm});
            skLineSegment(sketch, "E7.1.25.3", {"start": v(-67.7, -11.5) * mm, "end": v(-67.7, -10.5) * mm});
            skLineSegment(sketch, "E7.1.25.4", {"start": v(-66.7, -11.5) * mm, "end": v(-66.7, -10.5) * mm});
            skLineSegment(sketch, "E7.1.26.0", {"start": v(-66.71, -10) * mm, "end": v(-67.71, -10) * mm});
            skLineSegment(sketch, "E7.1.26.1", {"start": v(-66.71, -9) * mm, "end": v(-67.71, -9) * mm});
            skLineSegment(sketch, "E7.1.26.2", {"start": v(-67.71, -10) * mm, "end": v(-66.71, -10) * mm});
            skLineSegment(sketch, "E7.1.26.3", {"start": v(-67.71, -10) * mm, "end": v(-67.71, -9) * mm});
            skLineSegment(sketch, "E7.1.26.4", {"start": v(-66.71, -10) * mm, "end": v(-66.71, -9) * mm});
            skLineSegment(sketch, "E7.1.27.0", {"start": v(-66.72, -8.5) * mm, "end": v(-67.72, -8.5) * mm});
            skLineSegment(sketch, "E7.1.27.1", {"start": v(-66.72, -7.5) * mm, "end": v(-67.72, -7.5) * mm});
            skLineSegment(sketch, "E7.1.27.2", {"start": v(-67.72, -8.5) * mm, "end": v(-66.72, -8.5) * mm});
            skLineSegment(sketch, "E7.1.27.3", {"start": v(-67.72, -8.5) * mm, "end": v(-67.72, -7.5) * mm});
            skLineSegment(sketch, "E7.1.27.4", {"start": v(-66.72, -8.5) * mm, "end": v(-66.72, -7.5) * mm});
            skLineSegment(sketch, "E7.1.28.0", {"start": v(-66.73, -7) * mm, "end": v(-67.73, -7) * mm});
            skLineSegment(sketch, "E7.1.28.1", {"start": v(-66.73, -6) * mm, "end": v(-67.73, -6) * mm});
            skLineSegment(sketch, "E7.1.28.2", {"start": v(-67.73, -7) * mm, "end": v(-66.73, -7) * mm});
            skLineSegment(sketch, "E7.1.28.3", {"start": v(-67.73, -7) * mm, "end": v(-67.73, -6) * mm});
            skLineSegment(sketch, "E7.1.28.4", {"start": v(-66.73, -7) * mm, "end": v(-66.73, -6) * mm});
            skLineSegment(sketch, "E7.1.29.0", {"start": v(-66.74, -5.5) * mm, "end": v(-67.74, -5.5) * mm});
            skLineSegment(sketch, "E7.1.29.1", {"start": v(-66.74, -4.5) * mm, "end": v(-67.74, -4.5) * mm});
            skLineSegment(sketch, "E7.1.29.2", {"start": v(-67.74, -5.5) * mm, "end": v(-66.74, -5.5) * mm});
            skLineSegment(sketch, "E7.1.29.3", {"start": v(-67.74, -5.5) * mm, "end": v(-67.74, -4.5) * mm});
            skLineSegment(sketch, "E7.1.29.4", {"start": v(-66.74, -5.5) * mm, "end": v(-66.74, -4.5) * mm});
            skLineSegment(sketch, "E7.1.30.0", {"start": v(-66.75, -4) * mm, "end": v(-67.75, -4) * mm});
            skLineSegment(sketch, "E7.1.30.1", {"start": v(-66.75, -3) * mm, "end": v(-67.75, -3) * mm});
            skLineSegment(sketch, "E7.1.30.2", {"start": v(-67.75, -4) * mm, "end": v(-66.75, -4) * mm});
            skLineSegment(sketch, "E7.1.30.3", {"start": v(-67.75, -4) * mm, "end": v(-67.75, -3) * mm});
            skLineSegment(sketch, "E7.1.30.4", {"start": v(-66.75, -4) * mm, "end": v(-66.75, -3) * mm});
            skLineSegment(sketch, "E7.2.0.0", {"start": v(-65, -49) * mm, "end": v(-66, -49) * mm});
            skLineSegment(sketch, "E7.2.0.1", {"start": v(-65, -48) * mm, "end": v(-66, -48) * mm});
            skLineSegment(sketch, "E7.2.0.2", {"start": v(-66, -49) * mm, "end": v(-65, -49) * mm});
            skLineSegment(sketch, "E7.2.0.3", {"start": v(-66, -49) * mm, "end": v(-66, -48) * mm});
            skLineSegment(sketch, "E7.2.0.4", {"start": v(-65, -49) * mm, "end": v(-65, -48) * mm});
            skLineSegment(sketch, "E7.2.1.0", {"start": v(-65, -47.5) * mm, "end": v(-66, -47.5) * mm});
            skLineSegment(sketch, "E7.2.1.1", {"start": v(-65, -46.5) * mm, "end": v(-66, -46.5) * mm});
            skLineSegment(sketch, "E7.2.1.2", {"start": v(-66, -47.5) * mm, "end": v(-65, -47.5) * mm});
            skLineSegment(sketch, "E7.2.1.3", {"start": v(-66, -47.5) * mm, "end": v(-66, -46.5) * mm});
            skLineSegment(sketch, "E7.2.1.4", {"start": v(-65, -47.5) * mm, "end": v(-65, -46.5) * mm});
            skLineSegment(sketch, "E7.2.2.0", {"start": v(-65.02, -46) * mm, "end": v(-66.02, -46) * mm});
            skLineSegment(sketch, "E7.2.2.1", {"start": v(-65.02, -45) * mm, "end": v(-66.02, -45) * mm});
            skLineSegment(sketch, "E7.2.2.2", {"start": v(-66.02, -46) * mm, "end": v(-65.02, -46) * mm});
            skLineSegment(sketch, "E7.2.2.3", {"start": v(-66.02, -46) * mm, "end": v(-66.02, -45) * mm});
            skLineSegment(sketch, "E7.2.2.4", {"start": v(-65.02, -46) * mm, "end": v(-65.02, -45) * mm});
            skLineSegment(sketch, "E7.2.3.0", {"start": v(-65.02, -44.5) * mm, "end": v(-66.02, -44.5) * mm});
            skLineSegment(sketch, "E7.2.3.1", {"start": v(-65.02, -43.5) * mm, "end": v(-66.02, -43.5) * mm});
            skLineSegment(sketch, "E7.2.3.2", {"start": v(-66.02, -44.5) * mm, "end": v(-65.02, -44.5) * mm});
            skLineSegment(sketch, "E7.2.3.3", {"start": v(-66.02, -44.5) * mm, "end": v(-66.02, -43.5) * mm});
            skLineSegment(sketch, "E7.2.3.4", {"start": v(-65.02, -44.5) * mm, "end": v(-65.02, -43.5) * mm});
            skLineSegment(sketch, "E7.2.4.0", {"start": v(-65.03, -43) * mm, "end": v(-66.03, -43) * mm});
            skLineSegment(sketch, "E7.2.4.1", {"start": v(-65.03, -42) * mm, "end": v(-66.03, -42) * mm});
            skLineSegment(sketch, "E7.2.4.2", {"start": v(-66.03, -43) * mm, "end": v(-65.03, -43) * mm});
            skLineSegment(sketch, "E7.2.4.3", {"start": v(-66.03, -43) * mm, "end": v(-66.03, -42) * mm});
            skLineSegment(sketch, "E7.2.4.4", {"start": v(-65.03, -43) * mm, "end": v(-65.03, -42) * mm});
            skLineSegment(sketch, "E7.2.5.0", {"start": v(-65.04, -41.5) * mm, "end": v(-66.04, -41.5) * mm});
            skLineSegment(sketch, "E7.2.5.1", {"start": v(-65.04, -40.5) * mm, "end": v(-66.04, -40.5) * mm});
            skLineSegment(sketch, "E7.2.5.2", {"start": v(-66.04, -41.5) * mm, "end": v(-65.04, -41.5) * mm});
            skLineSegment(sketch, "E7.2.5.3", {"start": v(-66.04, -41.5) * mm, "end": v(-66.04, -40.5) * mm});
            skLineSegment(sketch, "E7.2.5.4", {"start": v(-65.04, -41.5) * mm, "end": v(-65.04, -40.5) * mm});
            skLineSegment(sketch, "E7.2.6.0", {"start": v(-65.05, -40) * mm, "end": v(-66.05, -40) * mm});
            skLineSegment(sketch, "E7.2.6.1", {"start": v(-65.05, -39) * mm, "end": v(-66.05, -39) * mm});
            skLineSegment(sketch, "E7.2.6.2", {"start": v(-66.05, -40) * mm, "end": v(-65.05, -40) * mm});
            skLineSegment(sketch, "E7.2.6.3", {"start": v(-66.05, -40) * mm, "end": v(-66.05, -39) * mm});
            skLineSegment(sketch, "E7.2.6.4", {"start": v(-65.05, -40) * mm, "end": v(-65.05, -39) * mm});
            skLineSegment(sketch, "E7.2.7.0", {"start": v(-65.06, -38.5) * mm, "end": v(-66.06, -38.5) * mm});
            skLineSegment(sketch, "E7.2.7.1", {"start": v(-65.06, -37.5) * mm, "end": v(-66.06, -37.5) * mm});
            skLineSegment(sketch, "E7.2.7.2", {"start": v(-66.06, -38.5) * mm, "end": v(-65.06, -38.5) * mm});
            skLineSegment(sketch, "E7.2.7.3", {"start": v(-66.06, -38.5) * mm, "end": v(-66.06, -37.5) * mm});
            skLineSegment(sketch, "E7.2.7.4", {"start": v(-65.06, -38.5) * mm, "end": v(-65.06, -37.5) * mm});
            skLineSegment(sketch, "E7.2.8.0", {"start": v(-65.07, -37) * mm, "end": v(-66.07, -37) * mm});
            skLineSegment(sketch, "E7.2.8.1", {"start": v(-65.07, -36) * mm, "end": v(-66.07, -36) * mm});
            skLineSegment(sketch, "E7.2.8.2", {"start": v(-66.07, -37) * mm, "end": v(-65.07, -37) * mm});
            skLineSegment(sketch, "E7.2.8.3", {"start": v(-66.07, -37) * mm, "end": v(-66.07, -36) * mm});
            skLineSegment(sketch, "E7.2.8.4", {"start": v(-65.07, -37) * mm, "end": v(-65.07, -36) * mm});
            skLineSegment(sketch, "E7.2.9.0", {"start": v(-65.07, -35.5) * mm, "end": v(-66.07, -35.5) * mm});
            skLineSegment(sketch, "E7.2.9.1", {"start": v(-65.07, -34.5) * mm, "end": v(-66.07, -34.5) * mm});
            skLineSegment(sketch, "E7.2.9.2", {"start": v(-66.07, -35.5) * mm, "end": v(-65.07, -35.5) * mm});
            skLineSegment(sketch, "E7.2.9.3", {"start": v(-66.07, -35.5) * mm, "end": v(-66.07, -34.5) * mm});
            skLineSegment(sketch, "E7.2.9.4", {"start": v(-65.07, -35.5) * mm, "end": v(-65.07, -34.5) * mm});
            skLineSegment(sketch, "E7.2.10.0", {"start": v(-65.08, -34) * mm, "end": v(-66.08, -34) * mm});
            skLineSegment(sketch, "E7.2.10.1", {"start": v(-65.08, -33) * mm, "end": v(-66.08, -33) * mm});
            skLineSegment(sketch, "E7.2.10.2", {"start": v(-66.08, -34) * mm, "end": v(-65.08, -34) * mm});
            skLineSegment(sketch, "E7.2.10.3", {"start": v(-66.08, -34) * mm, "end": v(-66.08, -33) * mm});
            skLineSegment(sketch, "E7.2.10.4", {"start": v(-65.08, -34) * mm, "end": v(-65.08, -33) * mm});
            skLineSegment(sketch, "E7.2.11.0", {"start": v(-65.1, -32.5) * mm, "end": v(-66.1, -32.5) * mm});
            skLineSegment(sketch, "E7.2.11.1", {"start": v(-65.1, -31.5) * mm, "end": v(-66.1, -31.5) * mm});
            skLineSegment(sketch, "E7.2.11.2", {"start": v(-66.1, -32.5) * mm, "end": v(-65.1, -32.5) * mm});
            skLineSegment(sketch, "E7.2.11.3", {"start": v(-66.1, -32.5) * mm, "end": v(-66.1, -31.5) * mm});
            skLineSegment(sketch, "E7.2.11.4", {"start": v(-65.1, -32.5) * mm, "end": v(-65.1, -31.5) * mm});
            skLineSegment(sketch, "E7.2.12.0", {"start": v(-65.1, -31) * mm, "end": v(-66.1, -31) * mm});
            skLineSegment(sketch, "E7.2.12.1", {"start": v(-65.1, -30) * mm, "end": v(-66.1, -30) * mm});
            skLineSegment(sketch, "E7.2.12.2", {"start": v(-66.1, -31) * mm, "end": v(-65.1, -31) * mm});
            skLineSegment(sketch, "E7.2.12.3", {"start": v(-66.1, -31) * mm, "end": v(-66.1, -30) * mm});
            skLineSegment(sketch, "E7.2.12.4", {"start": v(-65.1, -31) * mm, "end": v(-65.1, -30) * mm});
            skLineSegment(sketch, "E7.2.13.0", {"start": v(-65.1, -29.5) * mm, "end": v(-66.1, -29.5) * mm});
            skLineSegment(sketch, "E7.2.13.1", {"start": v(-65.1, -28.5) * mm, "end": v(-66.1, -28.5) * mm});
            skLineSegment(sketch, "E7.2.13.2", {"start": v(-66.1, -29.5) * mm, "end": v(-65.1, -29.5) * mm});
            skLineSegment(sketch, "E7.2.13.3", {"start": v(-66.1, -29.5) * mm, "end": v(-66.1, -28.5) * mm});
            skLineSegment(sketch, "E7.2.13.4", {"start": v(-65.1, -29.5) * mm, "end": v(-65.1, -28.5) * mm});
            skLineSegment(sketch, "E7.2.14.0", {"start": v(-65.11, -28) * mm, "end": v(-66.11, -28) * mm});
            skLineSegment(sketch, "E7.2.14.1", {"start": v(-65.11, -27) * mm, "end": v(-66.11, -27) * mm});
            skLineSegment(sketch, "E7.2.14.2", {"start": v(-66.11, -28) * mm, "end": v(-65.11, -28) * mm});
            skLineSegment(sketch, "E7.2.14.3", {"start": v(-66.11, -28) * mm, "end": v(-66.11, -27) * mm});
            skLineSegment(sketch, "E7.2.14.4", {"start": v(-65.11, -28) * mm, "end": v(-65.11, -27) * mm});
            skLineSegment(sketch, "E7.2.15.0", {"start": v(-65.12, -26.5) * mm, "end": v(-66.12, -26.5) * mm});
            skLineSegment(sketch, "E7.2.15.1", {"start": v(-65.12, -25.5) * mm, "end": v(-66.12, -25.5) * mm});
            skLineSegment(sketch, "E7.2.15.2", {"start": v(-66.12, -26.5) * mm, "end": v(-65.12, -26.5) * mm});
            skLineSegment(sketch, "E7.2.15.3", {"start": v(-66.12, -26.5) * mm, "end": v(-66.12, -25.5) * mm});
            skLineSegment(sketch, "E7.2.15.4", {"start": v(-65.12, -26.5) * mm, "end": v(-65.12, -25.5) * mm});
            skLineSegment(sketch, "E7.2.16.0", {"start": v(-65.13, -25) * mm, "end": v(-66.13, -25) * mm});
            skLineSegment(sketch, "E7.2.16.1", {"start": v(-65.13, -24) * mm, "end": v(-66.13, -24) * mm});
            skLineSegment(sketch, "E7.2.16.2", {"start": v(-66.13, -25) * mm, "end": v(-65.13, -25) * mm});
            skLineSegment(sketch, "E7.2.16.3", {"start": v(-66.13, -25) * mm, "end": v(-66.13, -24) * mm});
            skLineSegment(sketch, "E7.2.16.4", {"start": v(-65.13, -25) * mm, "end": v(-65.13, -24) * mm});
            skLineSegment(sketch, "E7.2.17.0", {"start": v(-65.14, -23.5) * mm, "end": v(-66.14, -23.5) * mm});
            skLineSegment(sketch, "E7.2.17.1", {"start": v(-65.14, -22.5) * mm, "end": v(-66.14, -22.5) * mm});
            skLineSegment(sketch, "E7.2.17.2", {"start": v(-66.14, -23.5) * mm, "end": v(-65.14, -23.5) * mm});
            skLineSegment(sketch, "E7.2.17.3", {"start": v(-66.14, -23.5) * mm, "end": v(-66.14, -22.5) * mm});
            skLineSegment(sketch, "E7.2.17.4", {"start": v(-65.14, -23.5) * mm, "end": v(-65.14, -22.5) * mm});
            skLineSegment(sketch, "E7.2.18.0", {"start": v(-65.15, -22) * mm, "end": v(-66.15, -22) * mm});
            skLineSegment(sketch, "E7.2.18.1", {"start": v(-65.15, -21) * mm, "end": v(-66.15, -21) * mm});
            skLineSegment(sketch, "E7.2.18.2", {"start": v(-66.15, -22) * mm, "end": v(-65.15, -22) * mm});
            skLineSegment(sketch, "E7.2.18.3", {"start": v(-66.15, -22) * mm, "end": v(-66.15, -21) * mm});
            skLineSegment(sketch, "E7.2.18.4", {"start": v(-65.15, -22) * mm, "end": v(-65.15, -21) * mm});
            skLineSegment(sketch, "E7.2.19.0", {"start": v(-65.16, -20.5) * mm, "end": v(-66.16, -20.5) * mm});
            skLineSegment(sketch, "E7.2.19.1", {"start": v(-65.16, -19.5) * mm, "end": v(-66.16, -19.5) * mm});
            skLineSegment(sketch, "E7.2.19.2", {"start": v(-66.16, -20.5) * mm, "end": v(-65.16, -20.5) * mm});
            skLineSegment(sketch, "E7.2.19.3", {"start": v(-66.16, -20.5) * mm, "end": v(-66.16, -19.5) * mm});
            skLineSegment(sketch, "E7.2.19.4", {"start": v(-65.16, -20.5) * mm, "end": v(-65.16, -19.5) * mm});
            skLineSegment(sketch, "E7.2.20.0", {"start": v(-65.16, -19) * mm, "end": v(-66.16, -19) * mm});
            skLineSegment(sketch, "E7.2.20.1", {"start": v(-65.16, -18) * mm, "end": v(-66.16, -18) * mm});
            skLineSegment(sketch, "E7.2.20.2", {"start": v(-66.16, -19) * mm, "end": v(-65.16, -19) * mm});
            skLineSegment(sketch, "E7.2.20.3", {"start": v(-66.16, -19) * mm, "end": v(-66.16, -18) * mm});
            skLineSegment(sketch, "E7.2.20.4", {"start": v(-65.16, -19) * mm, "end": v(-65.16, -18) * mm});
            skLineSegment(sketch, "E7.2.21.0", {"start": v(-65.17, -17.5) * mm, "end": v(-66.17, -17.5) * mm});
            skLineSegment(sketch, "E7.2.21.1", {"start": v(-65.17, -16.5) * mm, "end": v(-66.17, -16.5) * mm});
            skLineSegment(sketch, "E7.2.21.2", {"start": v(-66.17, -17.5) * mm, "end": v(-65.17, -17.5) * mm});
            skLineSegment(sketch, "E7.2.21.3", {"start": v(-66.17, -17.5) * mm, "end": v(-66.17, -16.5) * mm});
            skLineSegment(sketch, "E7.2.21.4", {"start": v(-65.17, -17.5) * mm, "end": v(-65.17, -16.5) * mm});
            skLineSegment(sketch, "E7.2.22.0", {"start": v(-65.18, -16) * mm, "end": v(-66.18, -16) * mm});
            skLineSegment(sketch, "E7.2.22.1", {"start": v(-65.18, -15) * mm, "end": v(-66.18, -15) * mm});
            skLineSegment(sketch, "E7.2.22.2", {"start": v(-66.18, -16) * mm, "end": v(-65.18, -16) * mm});
            skLineSegment(sketch, "E7.2.22.3", {"start": v(-66.18, -16) * mm, "end": v(-66.18, -15) * mm});
            skLineSegment(sketch, "E7.2.22.4", {"start": v(-65.18, -16) * mm, "end": v(-65.18, -15) * mm});
            skLineSegment(sketch, "E7.2.23.0", {"start": v(-65.19, -14.5) * mm, "end": v(-66.19, -14.5) * mm});
            skLineSegment(sketch, "E7.2.23.1", {"start": v(-65.19, -13.5) * mm, "end": v(-66.19, -13.5) * mm});
            skLineSegment(sketch, "E7.2.23.2", {"start": v(-66.19, -14.5) * mm, "end": v(-65.19, -14.5) * mm});
            skLineSegment(sketch, "E7.2.23.3", {"start": v(-66.19, -14.5) * mm, "end": v(-66.19, -13.5) * mm});
            skLineSegment(sketch, "E7.2.23.4", {"start": v(-65.19, -14.5) * mm, "end": v(-65.19, -13.5) * mm});
            skLineSegment(sketch, "E7.2.24.0", {"start": v(-65.2, -13) * mm, "end": v(-66.2, -13) * mm});
            skLineSegment(sketch, "E7.2.24.1", {"start": v(-65.2, -12) * mm, "end": v(-66.2, -12) * mm});
            skLineSegment(sketch, "E7.2.24.2", {"start": v(-66.2, -13) * mm, "end": v(-65.2, -13) * mm});
            skLineSegment(sketch, "E7.2.24.3", {"start": v(-66.2, -13) * mm, "end": v(-66.2, -12) * mm});
            skLineSegment(sketch, "E7.2.24.4", {"start": v(-65.2, -13) * mm, "end": v(-65.2, -12) * mm});
            skLineSegment(sketch, "E7.2.25.0", {"start": v(-65.2, -11.5) * mm, "end": v(-66.2, -11.5) * mm});
            skLineSegment(sketch, "E7.2.25.1", {"start": v(-65.2, -10.5) * mm, "end": v(-66.2, -10.5) * mm});
            skLineSegment(sketch, "E7.2.25.2", {"start": v(-66.2, -11.5) * mm, "end": v(-65.2, -11.5) * mm});
            skLineSegment(sketch, "E7.2.25.3", {"start": v(-66.2, -11.5) * mm, "end": v(-66.2, -10.5) * mm});
            skLineSegment(sketch, "E7.2.25.4", {"start": v(-65.2, -11.5) * mm, "end": v(-65.2, -10.5) * mm});
            skLineSegment(sketch, "E7.2.26.0", {"start": v(-65.21, -10) * mm, "end": v(-66.21, -10) * mm});
            skLineSegment(sketch, "E7.2.26.1", {"start": v(-65.21, -9) * mm, "end": v(-66.21, -9) * mm});
            skLineSegment(sketch, "E7.2.26.2", {"start": v(-66.21, -10) * mm, "end": v(-65.21, -10) * mm});
            skLineSegment(sketch, "E7.2.26.3", {"start": v(-66.21, -10) * mm, "end": v(-66.21, -9) * mm});
            skLineSegment(sketch, "E7.2.26.4", {"start": v(-65.21, -10) * mm, "end": v(-65.21, -9) * mm});
            skLineSegment(sketch, "E7.2.27.0", {"start": v(-65.22, -8.5) * mm, "end": v(-66.22, -8.5) * mm});
            skLineSegment(sketch, "E7.2.27.1", {"start": v(-65.22, -7.5) * mm, "end": v(-66.22, -7.5) * mm});
            skLineSegment(sketch, "E7.2.27.2", {"start": v(-66.22, -8.5) * mm, "end": v(-65.22, -8.5) * mm});
            skLineSegment(sketch, "E7.2.27.3", {"start": v(-66.22, -8.5) * mm, "end": v(-66.22, -7.5) * mm});
            skLineSegment(sketch, "E7.2.27.4", {"start": v(-65.22, -8.5) * mm, "end": v(-65.22, -7.5) * mm});
            skLineSegment(sketch, "E7.2.28.0", {"start": v(-65.23, -7) * mm, "end": v(-66.23, -7) * mm});
            skLineSegment(sketch, "E7.2.28.1", {"start": v(-65.23, -6) * mm, "end": v(-66.23, -6) * mm});
            skLineSegment(sketch, "E7.2.28.2", {"start": v(-66.23, -7) * mm, "end": v(-65.23, -7) * mm});
            skLineSegment(sketch, "E7.2.28.3", {"start": v(-66.23, -7) * mm, "end": v(-66.23, -6) * mm});
            skLineSegment(sketch, "E7.2.28.4", {"start": v(-65.23, -7) * mm, "end": v(-65.23, -6) * mm});
            skLineSegment(sketch, "E7.2.29.0", {"start": v(-65.24, -5.5) * mm, "end": v(-66.24, -5.5) * mm});
            skLineSegment(sketch, "E7.2.29.1", {"start": v(-65.24, -4.5) * mm, "end": v(-66.24, -4.5) * mm});
            skLineSegment(sketch, "E7.2.29.2", {"start": v(-66.24, -5.5) * mm, "end": v(-65.24, -5.5) * mm});
            skLineSegment(sketch, "E7.2.29.3", {"start": v(-66.24, -5.5) * mm, "end": v(-66.24, -4.5) * mm});
            skLineSegment(sketch, "E7.2.29.4", {"start": v(-65.24, -5.5) * mm, "end": v(-65.24, -4.5) * mm});
            skLineSegment(sketch, "E7.2.30.0", {"start": v(-65.25, -4) * mm, "end": v(-66.25, -4) * mm});
            skLineSegment(sketch, "E7.2.30.1", {"start": v(-65.25, -3) * mm, "end": v(-66.25, -3) * mm});
            skLineSegment(sketch, "E7.2.30.2", {"start": v(-66.25, -4) * mm, "end": v(-65.25, -4) * mm});
            skLineSegment(sketch, "E7.2.30.3", {"start": v(-66.25, -4) * mm, "end": v(-66.25, -3) * mm});
            skLineSegment(sketch, "E7.2.30.4", {"start": v(-65.25, -4) * mm, "end": v(-65.25, -3) * mm});
            skLineSegment(sketch, "E7.3.0.0", {"start": v(-63.5, -49) * mm, "end": v(-64.5, -49) * mm});
            skLineSegment(sketch, "E7.3.0.1", {"start": v(-63.5, -48) * mm, "end": v(-64.5, -48) * mm});
            skLineSegment(sketch, "E7.3.0.2", {"start": v(-64.5, -49) * mm, "end": v(-63.5, -49) * mm});
            skLineSegment(sketch, "E7.3.0.3", {"start": v(-64.5, -49) * mm, "end": v(-64.5, -48) * mm});
            skLineSegment(sketch, "E7.3.0.4", {"start": v(-63.5, -49) * mm, "end": v(-63.5, -48) * mm});
            skLineSegment(sketch, "E7.3.1.0", {"start": v(-63.5, -47.5) * mm, "end": v(-64.5, -47.5) * mm});
            skLineSegment(sketch, "E7.3.1.1", {"start": v(-63.5, -46.5) * mm, "end": v(-64.5, -46.5) * mm});
            skLineSegment(sketch, "E7.3.1.2", {"start": v(-64.5, -47.5) * mm, "end": v(-63.5, -47.5) * mm});
            skLineSegment(sketch, "E7.3.1.3", {"start": v(-64.5, -47.5) * mm, "end": v(-64.5, -46.5) * mm});
            skLineSegment(sketch, "E7.3.1.4", {"start": v(-63.5, -47.5) * mm, "end": v(-63.5, -46.5) * mm});
            skLineSegment(sketch, "E7.3.2.0", {"start": v(-63.52, -46) * mm, "end": v(-64.52, -46) * mm});
            skLineSegment(sketch, "E7.3.2.1", {"start": v(-63.52, -45) * mm, "end": v(-64.52, -45) * mm});
            skLineSegment(sketch, "E7.3.2.2", {"start": v(-64.52, -46) * mm, "end": v(-63.52, -46) * mm});
            skLineSegment(sketch, "E7.3.2.3", {"start": v(-64.52, -46) * mm, "end": v(-64.52, -45) * mm});
            skLineSegment(sketch, "E7.3.2.4", {"start": v(-63.52, -46) * mm, "end": v(-63.52, -45) * mm});
            skLineSegment(sketch, "E7.3.3.0", {"start": v(-63.52, -44.5) * mm, "end": v(-64.52, -44.5) * mm});
            skLineSegment(sketch, "E7.3.3.1", {"start": v(-63.52, -43.5) * mm, "end": v(-64.52, -43.5) * mm});
            skLineSegment(sketch, "E7.3.3.2", {"start": v(-64.52, -44.5) * mm, "end": v(-63.52, -44.5) * mm});
            skLineSegment(sketch, "E7.3.3.3", {"start": v(-64.52, -44.5) * mm, "end": v(-64.52, -43.5) * mm});
            skLineSegment(sketch, "E7.3.3.4", {"start": v(-63.52, -44.5) * mm, "end": v(-63.52, -43.5) * mm});
            skLineSegment(sketch, "E7.3.4.0", {"start": v(-63.53, -43) * mm, "end": v(-64.53, -43) * mm});
            skLineSegment(sketch, "E7.3.4.1", {"start": v(-63.53, -42) * mm, "end": v(-64.53, -42) * mm});
            skLineSegment(sketch, "E7.3.4.2", {"start": v(-64.53, -43) * mm, "end": v(-63.53, -43) * mm});
            skLineSegment(sketch, "E7.3.4.3", {"start": v(-64.53, -43) * mm, "end": v(-64.53, -42) * mm});
            skLineSegment(sketch, "E7.3.4.4", {"start": v(-63.53, -43) * mm, "end": v(-63.53, -42) * mm});
            skLineSegment(sketch, "E7.3.5.0", {"start": v(-63.54, -41.5) * mm, "end": v(-64.54, -41.5) * mm});
            skLineSegment(sketch, "E7.3.5.1", {"start": v(-63.54, -40.5) * mm, "end": v(-64.54, -40.5) * mm});
            skLineSegment(sketch, "E7.3.5.2", {"start": v(-64.54, -41.5) * mm, "end": v(-63.54, -41.5) * mm});
            skLineSegment(sketch, "E7.3.5.3", {"start": v(-64.54, -41.5) * mm, "end": v(-64.54, -40.5) * mm});
            skLineSegment(sketch, "E7.3.5.4", {"start": v(-63.54, -41.5) * mm, "end": v(-63.54, -40.5) * mm});
            skLineSegment(sketch, "E7.3.6.0", {"start": v(-63.55, -40) * mm, "end": v(-64.55, -40) * mm});
            skLineSegment(sketch, "E7.3.6.1", {"start": v(-63.55, -39) * mm, "end": v(-64.55, -39) * mm});
            skLineSegment(sketch, "E7.3.6.2", {"start": v(-64.55, -40) * mm, "end": v(-63.55, -40) * mm});
            skLineSegment(sketch, "E7.3.6.3", {"start": v(-64.55, -40) * mm, "end": v(-64.55, -39) * mm});
            skLineSegment(sketch, "E7.3.6.4", {"start": v(-63.55, -40) * mm, "end": v(-63.55, -39) * mm});
            skLineSegment(sketch, "E7.3.7.0", {"start": v(-63.56, -38.5) * mm, "end": v(-64.56, -38.5) * mm});
            skLineSegment(sketch, "E7.3.7.1", {"start": v(-63.56, -37.5) * mm, "end": v(-64.56, -37.5) * mm});
            skLineSegment(sketch, "E7.3.7.2", {"start": v(-64.56, -38.5) * mm, "end": v(-63.56, -38.5) * mm});
            skLineSegment(sketch, "E7.3.7.3", {"start": v(-64.56, -38.5) * mm, "end": v(-64.56, -37.5) * mm});
            skLineSegment(sketch, "E7.3.7.4", {"start": v(-63.56, -38.5) * mm, "end": v(-63.56, -37.5) * mm});
            skLineSegment(sketch, "E7.3.8.0", {"start": v(-63.57, -37) * mm, "end": v(-64.57, -37) * mm});
            skLineSegment(sketch, "E7.3.8.1", {"start": v(-63.57, -36) * mm, "end": v(-64.57, -36) * mm});
            skLineSegment(sketch, "E7.3.8.2", {"start": v(-64.57, -37) * mm, "end": v(-63.57, -37) * mm});
            skLineSegment(sketch, "E7.3.8.3", {"start": v(-64.57, -37) * mm, "end": v(-64.57, -36) * mm});
            skLineSegment(sketch, "E7.3.8.4", {"start": v(-63.57, -37) * mm, "end": v(-63.57, -36) * mm});
            skLineSegment(sketch, "E7.3.9.0", {"start": v(-63.57, -35.5) * mm, "end": v(-64.57, -35.5) * mm});
            skLineSegment(sketch, "E7.3.9.1", {"start": v(-63.57, -34.5) * mm, "end": v(-64.57, -34.5) * mm});
            skLineSegment(sketch, "E7.3.9.2", {"start": v(-64.57, -35.5) * mm, "end": v(-63.57, -35.5) * mm});
            skLineSegment(sketch, "E7.3.9.3", {"start": v(-64.57, -35.5) * mm, "end": v(-64.57, -34.5) * mm});
            skLineSegment(sketch, "E7.3.9.4", {"start": v(-63.57, -35.5) * mm, "end": v(-63.57, -34.5) * mm});
            skLineSegment(sketch, "E7.3.10.0", {"start": v(-63.58, -34) * mm, "end": v(-64.58, -34) * mm});
            skLineSegment(sketch, "E7.3.10.1", {"start": v(-63.58, -33) * mm, "end": v(-64.58, -33) * mm});
            skLineSegment(sketch, "E7.3.10.2", {"start": v(-64.58, -34) * mm, "end": v(-63.58, -34) * mm});
            skLineSegment(sketch, "E7.3.10.3", {"start": v(-64.58, -34) * mm, "end": v(-64.58, -33) * mm});
            skLineSegment(sketch, "E7.3.10.4", {"start": v(-63.58, -34) * mm, "end": v(-63.58, -33) * mm});
            skLineSegment(sketch, "E7.3.11.0", {"start": v(-63.6, -32.5) * mm, "end": v(-64.6, -32.5) * mm});
            skLineSegment(sketch, "E7.3.11.1", {"start": v(-63.6, -31.5) * mm, "end": v(-64.6, -31.5) * mm});
            skLineSegment(sketch, "E7.3.11.2", {"start": v(-64.6, -32.5) * mm, "end": v(-63.6, -32.5) * mm});
            skLineSegment(sketch, "E7.3.11.3", {"start": v(-64.6, -32.5) * mm, "end": v(-64.6, -31.5) * mm});
            skLineSegment(sketch, "E7.3.11.4", {"start": v(-63.6, -32.5) * mm, "end": v(-63.6, -31.5) * mm});
            skLineSegment(sketch, "E7.3.12.0", {"start": v(-63.6, -31) * mm, "end": v(-64.6, -31) * mm});
            skLineSegment(sketch, "E7.3.12.1", {"start": v(-63.6, -30) * mm, "end": v(-64.6, -30) * mm});
            skLineSegment(sketch, "E7.3.12.2", {"start": v(-64.6, -31) * mm, "end": v(-63.6, -31) * mm});
            skLineSegment(sketch, "E7.3.12.3", {"start": v(-64.6, -31) * mm, "end": v(-64.6, -30) * mm});
            skLineSegment(sketch, "E7.3.12.4", {"start": v(-63.6, -31) * mm, "end": v(-63.6, -30) * mm});
            skLineSegment(sketch, "E7.3.13.0", {"start": v(-63.6, -29.5) * mm, "end": v(-64.6, -29.5) * mm});
            skLineSegment(sketch, "E7.3.13.1", {"start": v(-63.6, -28.5) * mm, "end": v(-64.6, -28.5) * mm});
            skLineSegment(sketch, "E7.3.13.2", {"start": v(-64.6, -29.5) * mm, "end": v(-63.6, -29.5) * mm});
            skLineSegment(sketch, "E7.3.13.3", {"start": v(-64.6, -29.5) * mm, "end": v(-64.6, -28.5) * mm});
            skLineSegment(sketch, "E7.3.13.4", {"start": v(-63.6, -29.5) * mm, "end": v(-63.6, -28.5) * mm});
            skLineSegment(sketch, "E7.3.14.0", {"start": v(-63.61, -28) * mm, "end": v(-64.61, -28) * mm});
            skLineSegment(sketch, "E7.3.14.1", {"start": v(-63.61, -27) * mm, "end": v(-64.61, -27) * mm});
            skLineSegment(sketch, "E7.3.14.2", {"start": v(-64.61, -28) * mm, "end": v(-63.61, -28) * mm});
            skLineSegment(sketch, "E7.3.14.3", {"start": v(-64.61, -28) * mm, "end": v(-64.61, -27) * mm});
            skLineSegment(sketch, "E7.3.14.4", {"start": v(-63.61, -28) * mm, "end": v(-63.61, -27) * mm});
            skLineSegment(sketch, "E7.3.15.0", {"start": v(-63.62, -26.5) * mm, "end": v(-64.62, -26.5) * mm});
            skLineSegment(sketch, "E7.3.15.1", {"start": v(-63.62, -25.5) * mm, "end": v(-64.62, -25.5) * mm});
            skLineSegment(sketch, "E7.3.15.2", {"start": v(-64.62, -26.5) * mm, "end": v(-63.62, -26.5) * mm});
            skLineSegment(sketch, "E7.3.15.3", {"start": v(-64.62, -26.5) * mm, "end": v(-64.62, -25.5) * mm});
            skLineSegment(sketch, "E7.3.15.4", {"start": v(-63.62, -26.5) * mm, "end": v(-63.62, -25.5) * mm});
            skLineSegment(sketch, "E7.3.16.0", {"start": v(-63.63, -25) * mm, "end": v(-64.63, -25) * mm});
            skLineSegment(sketch, "E7.3.16.1", {"start": v(-63.63, -24) * mm, "end": v(-64.63, -24) * mm});
            skLineSegment(sketch, "E7.3.16.2", {"start": v(-64.63, -25) * mm, "end": v(-63.63, -25) * mm});
            skLineSegment(sketch, "E7.3.16.3", {"start": v(-64.63, -25) * mm, "end": v(-64.63, -24) * mm});
            skLineSegment(sketch, "E7.3.16.4", {"start": v(-63.63, -25) * mm, "end": v(-63.63, -24) * mm});
            skLineSegment(sketch, "E7.3.17.0", {"start": v(-63.64, -23.5) * mm, "end": v(-64.64, -23.5) * mm});
            skLineSegment(sketch, "E7.3.17.1", {"start": v(-63.64, -22.5) * mm, "end": v(-64.64, -22.5) * mm});
            skLineSegment(sketch, "E7.3.17.2", {"start": v(-64.64, -23.5) * mm, "end": v(-63.64, -23.5) * mm});
            skLineSegment(sketch, "E7.3.17.3", {"start": v(-64.64, -23.5) * mm, "end": v(-64.64, -22.5) * mm});
            skLineSegment(sketch, "E7.3.17.4", {"start": v(-63.64, -23.5) * mm, "end": v(-63.64, -22.5) * mm});
            skLineSegment(sketch, "E7.3.18.0", {"start": v(-63.65, -22) * mm, "end": v(-64.65, -22) * mm});
            skLineSegment(sketch, "E7.3.18.1", {"start": v(-63.65, -21) * mm, "end": v(-64.65, -21) * mm});
            skLineSegment(sketch, "E7.3.18.2", {"start": v(-64.65, -22) * mm, "end": v(-63.65, -22) * mm});
            skLineSegment(sketch, "E7.3.18.3", {"start": v(-64.65, -22) * mm, "end": v(-64.65, -21) * mm});
            skLineSegment(sketch, "E7.3.18.4", {"start": v(-63.65, -22) * mm, "end": v(-63.65, -21) * mm});
            skLineSegment(sketch, "E7.3.19.0", {"start": v(-63.66, -20.5) * mm, "end": v(-64.66, -20.5) * mm});
            skLineSegment(sketch, "E7.3.19.1", {"start": v(-63.66, -19.5) * mm, "end": v(-64.66, -19.5) * mm});
            skLineSegment(sketch, "E7.3.19.2", {"start": v(-64.66, -20.5) * mm, "end": v(-63.66, -20.5) * mm});
            skLineSegment(sketch, "E7.3.19.3", {"start": v(-64.66, -20.5) * mm, "end": v(-64.66, -19.5) * mm});
            skLineSegment(sketch, "E7.3.19.4", {"start": v(-63.66, -20.5) * mm, "end": v(-63.66, -19.5) * mm});
            skLineSegment(sketch, "E7.3.20.0", {"start": v(-63.66, -19) * mm, "end": v(-64.66, -19) * mm});
            skLineSegment(sketch, "E7.3.20.1", {"start": v(-63.66, -18) * mm, "end": v(-64.66, -18) * mm});
            skLineSegment(sketch, "E7.3.20.2", {"start": v(-64.66, -19) * mm, "end": v(-63.66, -19) * mm});
            skLineSegment(sketch, "E7.3.20.3", {"start": v(-64.66, -19) * mm, "end": v(-64.66, -18) * mm});
            skLineSegment(sketch, "E7.3.20.4", {"start": v(-63.66, -19) * mm, "end": v(-63.66, -18) * mm});
            skLineSegment(sketch, "E7.3.21.0", {"start": v(-63.67, -17.5) * mm, "end": v(-64.67, -17.5) * mm});
            skLineSegment(sketch, "E7.3.21.1", {"start": v(-63.67, -16.5) * mm, "end": v(-64.67, -16.5) * mm});
            skLineSegment(sketch, "E7.3.21.2", {"start": v(-64.67, -17.5) * mm, "end": v(-63.67, -17.5) * mm});
            skLineSegment(sketch, "E7.3.21.3", {"start": v(-64.67, -17.5) * mm, "end": v(-64.67, -16.5) * mm});
            skLineSegment(sketch, "E7.3.21.4", {"start": v(-63.67, -17.5) * mm, "end": v(-63.67, -16.5) * mm});
            skLineSegment(sketch, "E7.3.22.0", {"start": v(-63.68, -16) * mm, "end": v(-64.68, -16) * mm});
            skLineSegment(sketch, "E7.3.22.1", {"start": v(-63.68, -15) * mm, "end": v(-64.68, -15) * mm});
            skLineSegment(sketch, "E7.3.22.2", {"start": v(-64.68, -16) * mm, "end": v(-63.68, -16) * mm});
            skLineSegment(sketch, "E7.3.22.3", {"start": v(-64.68, -16) * mm, "end": v(-64.68, -15) * mm});
            skLineSegment(sketch, "E7.3.22.4", {"start": v(-63.68, -16) * mm, "end": v(-63.68, -15) * mm});
            skLineSegment(sketch, "E7.3.23.0", {"start": v(-63.69, -14.5) * mm, "end": v(-64.69, -14.5) * mm});
            skLineSegment(sketch, "E7.3.23.1", {"start": v(-63.69, -13.5) * mm, "end": v(-64.69, -13.5) * mm});
            skLineSegment(sketch, "E7.3.23.2", {"start": v(-64.69, -14.5) * mm, "end": v(-63.69, -14.5) * mm});
            skLineSegment(sketch, "E7.3.23.3", {"start": v(-64.69, -14.5) * mm, "end": v(-64.69, -13.5) * mm});
            skLineSegment(sketch, "E7.3.23.4", {"start": v(-63.69, -14.5) * mm, "end": v(-63.69, -13.5) * mm});
            skLineSegment(sketch, "E7.3.24.0", {"start": v(-63.7, -13) * mm, "end": v(-64.7, -13) * mm});
            skLineSegment(sketch, "E7.3.24.1", {"start": v(-63.7, -12) * mm, "end": v(-64.7, -12) * mm});
            skLineSegment(sketch, "E7.3.24.2", {"start": v(-64.7, -13) * mm, "end": v(-63.7, -13) * mm});
            skLineSegment(sketch, "E7.3.24.3", {"start": v(-64.7, -13) * mm, "end": v(-64.7, -12) * mm});
            skLineSegment(sketch, "E7.3.24.4", {"start": v(-63.7, -13) * mm, "end": v(-63.7, -12) * mm});
            skLineSegment(sketch, "E7.3.25.0", {"start": v(-63.7, -11.5) * mm, "end": v(-64.7, -11.5) * mm});
            skLineSegment(sketch, "E7.3.25.1", {"start": v(-63.7, -10.5) * mm, "end": v(-64.7, -10.5) * mm});
            skLineSegment(sketch, "E7.3.25.2", {"start": v(-64.7, -11.5) * mm, "end": v(-63.7, -11.5) * mm});
            skLineSegment(sketch, "E7.3.25.3", {"start": v(-64.7, -11.5) * mm, "end": v(-64.7, -10.5) * mm});
            skLineSegment(sketch, "E7.3.25.4", {"start": v(-63.7, -11.5) * mm, "end": v(-63.7, -10.5) * mm});
            skLineSegment(sketch, "E7.3.26.0", {"start": v(-63.71, -10) * mm, "end": v(-64.71, -10) * mm});
            skLineSegment(sketch, "E7.3.26.1", {"start": v(-63.71, -9) * mm, "end": v(-64.71, -9) * mm});
            skLineSegment(sketch, "E7.3.26.2", {"start": v(-64.71, -10) * mm, "end": v(-63.71, -10) * mm});
            skLineSegment(sketch, "E7.3.26.3", {"start": v(-64.71, -10) * mm, "end": v(-64.71, -9) * mm});
            skLineSegment(sketch, "E7.3.26.4", {"start": v(-63.71, -10) * mm, "end": v(-63.71, -9) * mm});
            skLineSegment(sketch, "E7.3.27.0", {"start": v(-63.72, -8.5) * mm, "end": v(-64.72, -8.5) * mm});
            skLineSegment(sketch, "E7.3.27.1", {"start": v(-63.72, -7.5) * mm, "end": v(-64.72, -7.5) * mm});
            skLineSegment(sketch, "E7.3.27.2", {"start": v(-64.72, -8.5) * mm, "end": v(-63.72, -8.5) * mm});
            skLineSegment(sketch, "E7.3.27.3", {"start": v(-64.72, -8.5) * mm, "end": v(-64.72, -7.5) * mm});
            skLineSegment(sketch, "E7.3.27.4", {"start": v(-63.72, -8.5) * mm, "end": v(-63.72, -7.5) * mm});
            skLineSegment(sketch, "E7.3.28.0", {"start": v(-63.73, -7) * mm, "end": v(-64.73, -7) * mm});
            skLineSegment(sketch, "E7.3.28.1", {"start": v(-63.73, -6) * mm, "end": v(-64.73, -6) * mm});
            skLineSegment(sketch, "E7.3.28.2", {"start": v(-64.73, -7) * mm, "end": v(-63.73, -7) * mm});
            skLineSegment(sketch, "E7.3.28.3", {"start": v(-64.73, -7) * mm, "end": v(-64.73, -6) * mm});
            skLineSegment(sketch, "E7.3.28.4", {"start": v(-63.73, -7) * mm, "end": v(-63.73, -6) * mm});
            skLineSegment(sketch, "E7.3.29.0", {"start": v(-63.74, -5.5) * mm, "end": v(-64.74, -5.5) * mm});
            skLineSegment(sketch, "E7.3.29.1", {"start": v(-63.74, -4.5) * mm, "end": v(-64.74, -4.5) * mm});
            skLineSegment(sketch, "E7.3.29.2", {"start": v(-64.74, -5.5) * mm, "end": v(-63.74, -5.5) * mm});
            skLineSegment(sketch, "E7.3.29.3", {"start": v(-64.74, -5.5) * mm, "end": v(-64.74, -4.5) * mm});
            skLineSegment(sketch, "E7.3.29.4", {"start": v(-63.74, -5.5) * mm, "end": v(-63.74, -4.5) * mm});
            skLineSegment(sketch, "E7.3.30.0", {"start": v(-63.75, -4) * mm, "end": v(-64.75, -4) * mm});
            skLineSegment(sketch, "E7.3.30.1", {"start": v(-63.75, -3) * mm, "end": v(-64.75, -3) * mm});
            skLineSegment(sketch, "E7.3.30.2", {"start": v(-64.75, -4) * mm, "end": v(-63.75, -4) * mm});
            skLineSegment(sketch, "E7.3.30.3", {"start": v(-64.75, -4) * mm, "end": v(-64.75, -3) * mm});
            skLineSegment(sketch, "E7.3.30.4", {"start": v(-63.75, -4) * mm, "end": v(-63.75, -3) * mm});
            skLineSegment(sketch, "E7.4.0.0", {"start": v(-62, -49) * mm, "end": v(-63, -49) * mm});
            skLineSegment(sketch, "E7.4.0.1", {"start": v(-62, -48) * mm, "end": v(-63, -48) * mm});
            skLineSegment(sketch, "E7.4.0.2", {"start": v(-63, -49) * mm, "end": v(-62, -49) * mm});
            skLineSegment(sketch, "E7.4.0.3", {"start": v(-63, -49) * mm, "end": v(-63, -48) * mm});
            skLineSegment(sketch, "E7.4.0.4", {"start": v(-62, -49) * mm, "end": v(-62, -48) * mm});
            skLineSegment(sketch, "E7.4.1.0", {"start": v(-62, -47.5) * mm, "end": v(-63, -47.5) * mm});
            skLineSegment(sketch, "E7.4.1.1", {"start": v(-62, -46.5) * mm, "end": v(-63, -46.5) * mm});
            skLineSegment(sketch, "E7.4.1.2", {"start": v(-63, -47.5) * mm, "end": v(-62, -47.5) * mm});
            skLineSegment(sketch, "E7.4.1.3", {"start": v(-63, -47.5) * mm, "end": v(-63, -46.5) * mm});
            skLineSegment(sketch, "E7.4.1.4", {"start": v(-62, -47.5) * mm, "end": v(-62, -46.5) * mm});
            skLineSegment(sketch, "E7.4.2.0", {"start": v(-62.02, -46) * mm, "end": v(-63.02, -46) * mm});
            skLineSegment(sketch, "E7.4.2.1", {"start": v(-62.02, -45) * mm, "end": v(-63.02, -45) * mm});
            skLineSegment(sketch, "E7.4.2.2", {"start": v(-63.02, -46) * mm, "end": v(-62.02, -46) * mm});
            skLineSegment(sketch, "E7.4.2.3", {"start": v(-63.02, -46) * mm, "end": v(-63.02, -45) * mm});
            skLineSegment(sketch, "E7.4.2.4", {"start": v(-62.02, -46) * mm, "end": v(-62.02, -45) * mm});
            skLineSegment(sketch, "E7.4.3.0", {"start": v(-62.02, -44.5) * mm, "end": v(-63.02, -44.5) * mm});
            skLineSegment(sketch, "E7.4.3.1", {"start": v(-62.02, -43.5) * mm, "end": v(-63.02, -43.5) * mm});
            skLineSegment(sketch, "E7.4.3.2", {"start": v(-63.02, -44.5) * mm, "end": v(-62.02, -44.5) * mm});
            skLineSegment(sketch, "E7.4.3.3", {"start": v(-63.02, -44.5) * mm, "end": v(-63.02, -43.5) * mm});
            skLineSegment(sketch, "E7.4.3.4", {"start": v(-62.02, -44.5) * mm, "end": v(-62.02, -43.5) * mm});
            skLineSegment(sketch, "E7.4.4.0", {"start": v(-62.03, -43) * mm, "end": v(-63.03, -43) * mm});
            skLineSegment(sketch, "E7.4.4.1", {"start": v(-62.03, -42) * mm, "end": v(-63.03, -42) * mm});
            skLineSegment(sketch, "E7.4.4.2", {"start": v(-63.03, -43) * mm, "end": v(-62.03, -43) * mm});
            skLineSegment(sketch, "E7.4.4.3", {"start": v(-63.03, -43) * mm, "end": v(-63.03, -42) * mm});
            skLineSegment(sketch, "E7.4.4.4", {"start": v(-62.03, -43) * mm, "end": v(-62.03, -42) * mm});
            skLineSegment(sketch, "E7.4.5.0", {"start": v(-62.04, -41.5) * mm, "end": v(-63.04, -41.5) * mm});
            skLineSegment(sketch, "E7.4.5.1", {"start": v(-62.04, -40.5) * mm, "end": v(-63.04, -40.5) * mm});
            skLineSegment(sketch, "E7.4.5.2", {"start": v(-63.04, -41.5) * mm, "end": v(-62.04, -41.5) * mm});
            skLineSegment(sketch, "E7.4.5.3", {"start": v(-63.04, -41.5) * mm, "end": v(-63.04, -40.5) * mm});
            skLineSegment(sketch, "E7.4.5.4", {"start": v(-62.04, -41.5) * mm, "end": v(-62.04, -40.5) * mm});
            skLineSegment(sketch, "E7.4.6.0", {"start": v(-62.05, -40) * mm, "end": v(-63.05, -40) * mm});
            skLineSegment(sketch, "E7.4.6.1", {"start": v(-62.05, -39) * mm, "end": v(-63.05, -39) * mm});
            skLineSegment(sketch, "E7.4.6.2", {"start": v(-63.05, -40) * mm, "end": v(-62.05, -40) * mm});
            skLineSegment(sketch, "E7.4.6.3", {"start": v(-63.05, -40) * mm, "end": v(-63.05, -39) * mm});
            skLineSegment(sketch, "E7.4.6.4", {"start": v(-62.05, -40) * mm, "end": v(-62.05, -39) * mm});
            skLineSegment(sketch, "E7.4.7.0", {"start": v(-62.06, -38.5) * mm, "end": v(-63.06, -38.5) * mm});
            skLineSegment(sketch, "E7.4.7.1", {"start": v(-62.06, -37.5) * mm, "end": v(-63.06, -37.5) * mm});
            skLineSegment(sketch, "E7.4.7.2", {"start": v(-63.06, -38.5) * mm, "end": v(-62.06, -38.5) * mm});
            skLineSegment(sketch, "E7.4.7.3", {"start": v(-63.06, -38.5) * mm, "end": v(-63.06, -37.5) * mm});
            skLineSegment(sketch, "E7.4.7.4", {"start": v(-62.06, -38.5) * mm, "end": v(-62.06, -37.5) * mm});
            skLineSegment(sketch, "E7.4.8.0", {"start": v(-62.07, -37) * mm, "end": v(-63.07, -37) * mm});
            skLineSegment(sketch, "E7.4.8.1", {"start": v(-62.07, -36) * mm, "end": v(-63.07, -36) * mm});
            skLineSegment(sketch, "E7.4.8.2", {"start": v(-63.07, -37) * mm, "end": v(-62.07, -37) * mm});
            skLineSegment(sketch, "E7.4.8.3", {"start": v(-63.07, -37) * mm, "end": v(-63.07, -36) * mm});
            skLineSegment(sketch, "E7.4.8.4", {"start": v(-62.07, -37) * mm, "end": v(-62.07, -36) * mm});
            skLineSegment(sketch, "E7.4.9.0", {"start": v(-62.07, -35.5) * mm, "end": v(-63.07, -35.5) * mm});
            skLineSegment(sketch, "E7.4.9.1", {"start": v(-62.07, -34.5) * mm, "end": v(-63.07, -34.5) * mm});
            skLineSegment(sketch, "E7.4.9.2", {"start": v(-63.07, -35.5) * mm, "end": v(-62.07, -35.5) * mm});
            skLineSegment(sketch, "E7.4.9.3", {"start": v(-63.07, -35.5) * mm, "end": v(-63.07, -34.5) * mm});
            skLineSegment(sketch, "E7.4.9.4", {"start": v(-62.07, -35.5) * mm, "end": v(-62.07, -34.5) * mm});
            skLineSegment(sketch, "E7.4.10.0", {"start": v(-62.08, -34) * mm, "end": v(-63.08, -34) * mm});
            skLineSegment(sketch, "E7.4.10.1", {"start": v(-62.08, -33) * mm, "end": v(-63.08, -33) * mm});
            skLineSegment(sketch, "E7.4.10.2", {"start": v(-63.08, -34) * mm, "end": v(-62.08, -34) * mm});
            skLineSegment(sketch, "E7.4.10.3", {"start": v(-63.08, -34) * mm, "end": v(-63.08, -33) * mm});
            skLineSegment(sketch, "E7.4.10.4", {"start": v(-62.08, -34) * mm, "end": v(-62.08, -33) * mm});
            skLineSegment(sketch, "E7.4.11.0", {"start": v(-62.1, -32.5) * mm, "end": v(-63.1, -32.5) * mm});
            skLineSegment(sketch, "E7.4.11.1", {"start": v(-62.1, -31.5) * mm, "end": v(-63.1, -31.5) * mm});
            skLineSegment(sketch, "E7.4.11.2", {"start": v(-63.1, -32.5) * mm, "end": v(-62.1, -32.5) * mm});
            skLineSegment(sketch, "E7.4.11.3", {"start": v(-63.1, -32.5) * mm, "end": v(-63.1, -31.5) * mm});
            skLineSegment(sketch, "E7.4.11.4", {"start": v(-62.1, -32.5) * mm, "end": v(-62.1, -31.5) * mm});
            skLineSegment(sketch, "E7.4.12.0", {"start": v(-62.1, -31) * mm, "end": v(-63.1, -31) * mm});
            skLineSegment(sketch, "E7.4.12.1", {"start": v(-62.1, -30) * mm, "end": v(-63.1, -30) * mm});
            skLineSegment(sketch, "E7.4.12.2", {"start": v(-63.1, -31) * mm, "end": v(-62.1, -31) * mm});
            skLineSegment(sketch, "E7.4.12.3", {"start": v(-63.1, -31) * mm, "end": v(-63.1, -30) * mm});
            skLineSegment(sketch, "E7.4.12.4", {"start": v(-62.1, -31) * mm, "end": v(-62.1, -30) * mm});
            skLineSegment(sketch, "E7.4.13.0", {"start": v(-62.1, -29.5) * mm, "end": v(-63.1, -29.5) * mm});
            skLineSegment(sketch, "E7.4.13.1", {"start": v(-62.1, -28.5) * mm, "end": v(-63.1, -28.5) * mm});
            skLineSegment(sketch, "E7.4.13.2", {"start": v(-63.1, -29.5) * mm, "end": v(-62.1, -29.5) * mm});
            skLineSegment(sketch, "E7.4.13.3", {"start": v(-63.1, -29.5) * mm, "end": v(-63.1, -28.5) * mm});
            skLineSegment(sketch, "E7.4.13.4", {"start": v(-62.1, -29.5) * mm, "end": v(-62.1, -28.5) * mm});
            skLineSegment(sketch, "E7.4.14.0", {"start": v(-62.11, -28) * mm, "end": v(-63.11, -28) * mm});
            skLineSegment(sketch, "E7.4.14.1", {"start": v(-62.11, -27) * mm, "end": v(-63.11, -27) * mm});
            skLineSegment(sketch, "E7.4.14.2", {"start": v(-63.11, -28) * mm, "end": v(-62.11, -28) * mm});
            skLineSegment(sketch, "E7.4.14.3", {"start": v(-63.11, -28) * mm, "end": v(-63.11, -27) * mm});
            skLineSegment(sketch, "E7.4.14.4", {"start": v(-62.11, -28) * mm, "end": v(-62.11, -27) * mm});
            skLineSegment(sketch, "E7.4.15.0", {"start": v(-62.12, -26.5) * mm, "end": v(-63.12, -26.5) * mm});
            skLineSegment(sketch, "E7.4.15.1", {"start": v(-62.12, -25.5) * mm, "end": v(-63.12, -25.5) * mm});
            skLineSegment(sketch, "E7.4.15.2", {"start": v(-63.12, -26.5) * mm, "end": v(-62.12, -26.5) * mm});
            skLineSegment(sketch, "E7.4.15.3", {"start": v(-63.12, -26.5) * mm, "end": v(-63.12, -25.5) * mm});
            skLineSegment(sketch, "E7.4.15.4", {"start": v(-62.12, -26.5) * mm, "end": v(-62.12, -25.5) * mm});
            skLineSegment(sketch, "E7.4.16.0", {"start": v(-62.13, -25) * mm, "end": v(-63.13, -25) * mm});
            skLineSegment(sketch, "E7.4.16.1", {"start": v(-62.13, -24) * mm, "end": v(-63.13, -24) * mm});
            skLineSegment(sketch, "E7.4.16.2", {"start": v(-63.13, -25) * mm, "end": v(-62.13, -25) * mm});
            skLineSegment(sketch, "E7.4.16.3", {"start": v(-63.13, -25) * mm, "end": v(-63.13, -24) * mm});
            skLineSegment(sketch, "E7.4.16.4", {"start": v(-62.13, -25) * mm, "end": v(-62.13, -24) * mm});
            skLineSegment(sketch, "E7.4.17.0", {"start": v(-62.14, -23.5) * mm, "end": v(-63.14, -23.5) * mm});
            skLineSegment(sketch, "E7.4.17.1", {"start": v(-62.14, -22.5) * mm, "end": v(-63.14, -22.5) * mm});
            skLineSegment(sketch, "E7.4.17.2", {"start": v(-63.14, -23.5) * mm, "end": v(-62.14, -23.5) * mm});
            skLineSegment(sketch, "E7.4.17.3", {"start": v(-63.14, -23.5) * mm, "end": v(-63.14, -22.5) * mm});
            skLineSegment(sketch, "E7.4.17.4", {"start": v(-62.14, -23.5) * mm, "end": v(-62.14, -22.5) * mm});
            skLineSegment(sketch, "E7.4.18.0", {"start": v(-62.15, -22) * mm, "end": v(-63.15, -22) * mm});
            skLineSegment(sketch, "E7.4.18.1", {"start": v(-62.15, -21) * mm, "end": v(-63.15, -21) * mm});
            skLineSegment(sketch, "E7.4.18.2", {"start": v(-63.15, -22) * mm, "end": v(-62.15, -22) * mm});
            skLineSegment(sketch, "E7.4.18.3", {"start": v(-63.15, -22) * mm, "end": v(-63.15, -21) * mm});
            skLineSegment(sketch, "E7.4.18.4", {"start": v(-62.15, -22) * mm, "end": v(-62.15, -21) * mm});
            skLineSegment(sketch, "E7.4.19.0", {"start": v(-62.16, -20.5) * mm, "end": v(-63.16, -20.5) * mm});
            skLineSegment(sketch, "E7.4.19.1", {"start": v(-62.16, -19.5) * mm, "end": v(-63.16, -19.5) * mm});
            skLineSegment(sketch, "E7.4.19.2", {"start": v(-63.16, -20.5) * mm, "end": v(-62.16, -20.5) * mm});
            skLineSegment(sketch, "E7.4.19.3", {"start": v(-63.16, -20.5) * mm, "end": v(-63.16, -19.5) * mm});
            skLineSegment(sketch, "E7.4.19.4", {"start": v(-62.16, -20.5) * mm, "end": v(-62.16, -19.5) * mm});
            skLineSegment(sketch, "E7.4.20.0", {"start": v(-62.16, -19) * mm, "end": v(-63.16, -19) * mm});
            skLineSegment(sketch, "E7.4.20.1", {"start": v(-62.16, -18) * mm, "end": v(-63.16, -18) * mm});
            skLineSegment(sketch, "E7.4.20.2", {"start": v(-63.16, -19) * mm, "end": v(-62.16, -19) * mm});
            skLineSegment(sketch, "E7.4.20.3", {"start": v(-63.16, -19) * mm, "end": v(-63.16, -18) * mm});
            skLineSegment(sketch, "E7.4.20.4", {"start": v(-62.16, -19) * mm, "end": v(-62.16, -18) * mm});
            skLineSegment(sketch, "E7.4.21.0", {"start": v(-62.17, -17.5) * mm, "end": v(-63.17, -17.5) * mm});
            skLineSegment(sketch, "E7.4.21.1", {"start": v(-62.17, -16.5) * mm, "end": v(-63.17, -16.5) * mm});
            skLineSegment(sketch, "E7.4.21.2", {"start": v(-63.17, -17.5) * mm, "end": v(-62.17, -17.5) * mm});
            skLineSegment(sketch, "E7.4.21.3", {"start": v(-63.17, -17.5) * mm, "end": v(-63.17, -16.5) * mm});
            skLineSegment(sketch, "E7.4.21.4", {"start": v(-62.17, -17.5) * mm, "end": v(-62.17, -16.5) * mm});
            skLineSegment(sketch, "E7.4.22.0", {"start": v(-62.18, -16) * mm, "end": v(-63.18, -16) * mm});
            skLineSegment(sketch, "E7.4.22.1", {"start": v(-62.18, -15) * mm, "end": v(-63.18, -15) * mm});
            skLineSegment(sketch, "E7.4.22.2", {"start": v(-63.18, -16) * mm, "end": v(-62.18, -16) * mm});
            skLineSegment(sketch, "E7.4.22.3", {"start": v(-63.18, -16) * mm, "end": v(-63.18, -15) * mm});
            skLineSegment(sketch, "E7.4.22.4", {"start": v(-62.18, -16) * mm, "end": v(-62.18, -15) * mm});
            skLineSegment(sketch, "E7.4.23.0", {"start": v(-62.19, -14.5) * mm, "end": v(-63.19, -14.5) * mm});
            skLineSegment(sketch, "E7.4.23.1", {"start": v(-62.19, -13.5) * mm, "end": v(-63.19, -13.5) * mm});
            skLineSegment(sketch, "E7.4.23.2", {"start": v(-63.19, -14.5) * mm, "end": v(-62.19, -14.5) * mm});
            skLineSegment(sketch, "E7.4.23.3", {"start": v(-63.19, -14.5) * mm, "end": v(-63.19, -13.5) * mm});
            skLineSegment(sketch, "E7.4.23.4", {"start": v(-62.19, -14.5) * mm, "end": v(-62.19, -13.5) * mm});
            skLineSegment(sketch, "E7.4.24.0", {"start": v(-62.2, -13) * mm, "end": v(-63.2, -13) * mm});
            skLineSegment(sketch, "E7.4.24.1", {"start": v(-62.2, -12) * mm, "end": v(-63.2, -12) * mm});
            skLineSegment(sketch, "E7.4.24.2", {"start": v(-63.2, -13) * mm, "end": v(-62.2, -13) * mm});
            skLineSegment(sketch, "E7.4.24.3", {"start": v(-63.2, -13) * mm, "end": v(-63.2, -12) * mm});
            skLineSegment(sketch, "E7.4.24.4", {"start": v(-62.2, -13) * mm, "end": v(-62.2, -12) * mm});
            skLineSegment(sketch, "E7.4.25.0", {"start": v(-62.2, -11.5) * mm, "end": v(-63.2, -11.5) * mm});
            skLineSegment(sketch, "E7.4.25.1", {"start": v(-62.2, -10.5) * mm, "end": v(-63.2, -10.5) * mm});
            skLineSegment(sketch, "E7.4.25.2", {"start": v(-63.2, -11.5) * mm, "end": v(-62.2, -11.5) * mm});
            skLineSegment(sketch, "E7.4.25.3", {"start": v(-63.2, -11.5) * mm, "end": v(-63.2, -10.5) * mm});
            skLineSegment(sketch, "E7.4.25.4", {"start": v(-62.2, -11.5) * mm, "end": v(-62.2, -10.5) * mm});
            skLineSegment(sketch, "E7.4.26.0", {"start": v(-62.21, -10) * mm, "end": v(-63.21, -10) * mm});
            skLineSegment(sketch, "E7.4.26.1", {"start": v(-62.21, -9) * mm, "end": v(-63.21, -9) * mm});
            skLineSegment(sketch, "E7.4.26.2", {"start": v(-63.21, -10) * mm, "end": v(-62.21, -10) * mm});
            skLineSegment(sketch, "E7.4.26.3", {"start": v(-63.21, -10) * mm, "end": v(-63.21, -9) * mm});
            skLineSegment(sketch, "E7.4.26.4", {"start": v(-62.21, -10) * mm, "end": v(-62.21, -9) * mm});
            skLineSegment(sketch, "E7.4.27.0", {"start": v(-62.22, -8.5) * mm, "end": v(-63.22, -8.5) * mm});
            skLineSegment(sketch, "E7.4.27.1", {"start": v(-62.22, -7.5) * mm, "end": v(-63.22, -7.5) * mm});
            skLineSegment(sketch, "E7.4.27.2", {"start": v(-63.22, -8.5) * mm, "end": v(-62.22, -8.5) * mm});
            skLineSegment(sketch, "E7.4.27.3", {"start": v(-63.22, -8.5) * mm, "end": v(-63.22, -7.5) * mm});
            skLineSegment(sketch, "E7.4.27.4", {"start": v(-62.22, -8.5) * mm, "end": v(-62.22, -7.5) * mm});
            skLineSegment(sketch, "E7.4.28.0", {"start": v(-62.23, -7) * mm, "end": v(-63.23, -7) * mm});
            skLineSegment(sketch, "E7.4.28.1", {"start": v(-62.23, -6) * mm, "end": v(-63.23, -6) * mm});
            skLineSegment(sketch, "E7.4.28.2", {"start": v(-63.23, -7) * mm, "end": v(-62.23, -7) * mm});
            skLineSegment(sketch, "E7.4.28.3", {"start": v(-63.23, -7) * mm, "end": v(-63.23, -6) * mm});
            skLineSegment(sketch, "E7.4.28.4", {"start": v(-62.23, -7) * mm, "end": v(-62.23, -6) * mm});
            skLineSegment(sketch, "E7.4.29.0", {"start": v(-62.24, -5.5) * mm, "end": v(-63.24, -5.5) * mm});
            skLineSegment(sketch, "E7.4.29.1", {"start": v(-62.24, -4.5) * mm, "end": v(-63.24, -4.5) * mm});
            skLineSegment(sketch, "E7.4.29.2", {"start": v(-63.24, -5.5) * mm, "end": v(-62.24, -5.5) * mm});
            skLineSegment(sketch, "E7.4.29.3", {"start": v(-63.24, -5.5) * mm, "end": v(-63.24, -4.5) * mm});
            skLineSegment(sketch, "E7.4.29.4", {"start": v(-62.24, -5.5) * mm, "end": v(-62.24, -4.5) * mm});
            skLineSegment(sketch, "E7.4.30.0", {"start": v(-62.25, -4) * mm, "end": v(-63.25, -4) * mm});
            skLineSegment(sketch, "E7.4.30.1", {"start": v(-62.25, -3) * mm, "end": v(-63.25, -3) * mm});
            skLineSegment(sketch, "E7.4.30.2", {"start": v(-63.25, -4) * mm, "end": v(-62.25, -4) * mm});
            skLineSegment(sketch, "E7.4.30.3", {"start": v(-63.25, -4) * mm, "end": v(-63.25, -3) * mm});
            skLineSegment(sketch, "E7.4.30.4", {"start": v(-62.25, -4) * mm, "end": v(-62.25, -3) * mm});
            skLineSegment(sketch, "E7.5.0.0", {"start": v(-60.5, -49) * mm, "end": v(-61.5, -49) * mm});
            skLineSegment(sketch, "E7.5.0.1", {"start": v(-60.5, -48) * mm, "end": v(-61.5, -48) * mm});
            skLineSegment(sketch, "E7.5.0.2", {"start": v(-61.5, -49) * mm, "end": v(-60.5, -49) * mm});
            skLineSegment(sketch, "E7.5.0.3", {"start": v(-61.5, -49) * mm, "end": v(-61.5, -48) * mm});
            skLineSegment(sketch, "E7.5.0.4", {"start": v(-60.5, -49) * mm, "end": v(-60.5, -48) * mm});
            skLineSegment(sketch, "E7.5.1.0", {"start": v(-60.5, -47.5) * mm, "end": v(-61.5, -47.5) * mm});
            skLineSegment(sketch, "E7.5.1.1", {"start": v(-60.5, -46.5) * mm, "end": v(-61.5, -46.5) * mm});
            skLineSegment(sketch, "E7.5.1.2", {"start": v(-61.5, -47.5) * mm, "end": v(-60.5, -47.5) * mm});
            skLineSegment(sketch, "E7.5.1.3", {"start": v(-61.5, -47.5) * mm, "end": v(-61.5, -46.5) * mm});
            skLineSegment(sketch, "E7.5.1.4", {"start": v(-60.5, -47.5) * mm, "end": v(-60.5, -46.5) * mm});
            skLineSegment(sketch, "E7.5.2.0", {"start": v(-60.52, -46) * mm, "end": v(-61.52, -46) * mm});
            skLineSegment(sketch, "E7.5.2.1", {"start": v(-60.52, -45) * mm, "end": v(-61.52, -45) * mm});
            skLineSegment(sketch, "E7.5.2.2", {"start": v(-61.52, -46) * mm, "end": v(-60.52, -46) * mm});
            skLineSegment(sketch, "E7.5.2.3", {"start": v(-61.52, -46) * mm, "end": v(-61.52, -45) * mm});
            skLineSegment(sketch, "E7.5.2.4", {"start": v(-60.52, -46) * mm, "end": v(-60.52, -45) * mm});
            skLineSegment(sketch, "E7.5.3.0", {"start": v(-60.52, -44.5) * mm, "end": v(-61.52, -44.5) * mm});
            skLineSegment(sketch, "E7.5.3.1", {"start": v(-60.52, -43.5) * mm, "end": v(-61.52, -43.5) * mm});
            skLineSegment(sketch, "E7.5.3.2", {"start": v(-61.52, -44.5) * mm, "end": v(-60.52, -44.5) * mm});
            skLineSegment(sketch, "E7.5.3.3", {"start": v(-61.52, -44.5) * mm, "end": v(-61.52, -43.5) * mm});
            skLineSegment(sketch, "E7.5.3.4", {"start": v(-60.52, -44.5) * mm, "end": v(-60.52, -43.5) * mm});
            skLineSegment(sketch, "E7.5.4.0", {"start": v(-60.53, -43) * mm, "end": v(-61.53, -43) * mm});
            skLineSegment(sketch, "E7.5.4.1", {"start": v(-60.53, -42) * mm, "end": v(-61.53, -42) * mm});
            skLineSegment(sketch, "E7.5.4.2", {"start": v(-61.53, -43) * mm, "end": v(-60.53, -43) * mm});
            skLineSegment(sketch, "E7.5.4.3", {"start": v(-61.53, -43) * mm, "end": v(-61.53, -42) * mm});
            skLineSegment(sketch, "E7.5.4.4", {"start": v(-60.53, -43) * mm, "end": v(-60.53, -42) * mm});
            skLineSegment(sketch, "E7.5.5.0", {"start": v(-60.54, -41.5) * mm, "end": v(-61.54, -41.5) * mm});
            skLineSegment(sketch, "E7.5.5.1", {"start": v(-60.54, -40.5) * mm, "end": v(-61.54, -40.5) * mm});
            skLineSegment(sketch, "E7.5.5.2", {"start": v(-61.54, -41.5) * mm, "end": v(-60.54, -41.5) * mm});
            skLineSegment(sketch, "E7.5.5.3", {"start": v(-61.54, -41.5) * mm, "end": v(-61.54, -40.5) * mm});
            skLineSegment(sketch, "E7.5.5.4", {"start": v(-60.54, -41.5) * mm, "end": v(-60.54, -40.5) * mm});
            skLineSegment(sketch, "E7.5.6.0", {"start": v(-60.55, -40) * mm, "end": v(-61.55, -40) * mm});
            skLineSegment(sketch, "E7.5.6.1", {"start": v(-60.55, -39) * mm, "end": v(-61.55, -39) * mm});
            skLineSegment(sketch, "E7.5.6.2", {"start": v(-61.55, -40) * mm, "end": v(-60.55, -40) * mm});
            skLineSegment(sketch, "E7.5.6.3", {"start": v(-61.55, -40) * mm, "end": v(-61.55, -39) * mm});
            skLineSegment(sketch, "E7.5.6.4", {"start": v(-60.55, -40) * mm, "end": v(-60.55, -39) * mm});
            skLineSegment(sketch, "E7.5.7.0", {"start": v(-60.56, -38.5) * mm, "end": v(-61.56, -38.5) * mm});
            skLineSegment(sketch, "E7.5.7.1", {"start": v(-60.56, -37.5) * mm, "end": v(-61.56, -37.5) * mm});
            skLineSegment(sketch, "E7.5.7.2", {"start": v(-61.56, -38.5) * mm, "end": v(-60.56, -38.5) * mm});
            skLineSegment(sketch, "E7.5.7.3", {"start": v(-61.56, -38.5) * mm, "end": v(-61.56, -37.5) * mm});
            skLineSegment(sketch, "E7.5.7.4", {"start": v(-60.56, -38.5) * mm, "end": v(-60.56, -37.5) * mm});
            skLineSegment(sketch, "E7.5.8.0", {"start": v(-60.57, -37) * mm, "end": v(-61.57, -37) * mm});
            skLineSegment(sketch, "E7.5.8.1", {"start": v(-60.57, -36) * mm, "end": v(-61.57, -36) * mm});
            skLineSegment(sketch, "E7.5.8.2", {"start": v(-61.57, -37) * mm, "end": v(-60.57, -37) * mm});
            skLineSegment(sketch, "E7.5.8.3", {"start": v(-61.57, -37) * mm, "end": v(-61.57, -36) * mm});
            skLineSegment(sketch, "E7.5.8.4", {"start": v(-60.57, -37) * mm, "end": v(-60.57, -36) * mm});
            skLineSegment(sketch, "E7.5.9.0", {"start": v(-60.57, -35.5) * mm, "end": v(-61.57, -35.5) * mm});
            skLineSegment(sketch, "E7.5.9.1", {"start": v(-60.57, -34.5) * mm, "end": v(-61.57, -34.5) * mm});
            skLineSegment(sketch, "E7.5.9.2", {"start": v(-61.57, -35.5) * mm, "end": v(-60.57, -35.5) * mm});
            skLineSegment(sketch, "E7.5.9.3", {"start": v(-61.57, -35.5) * mm, "end": v(-61.57, -34.5) * mm});
            skLineSegment(sketch, "E7.5.9.4", {"start": v(-60.57, -35.5) * mm, "end": v(-60.57, -34.5) * mm});
            skLineSegment(sketch, "E7.5.10.0", {"start": v(-60.58, -34) * mm, "end": v(-61.58, -34) * mm});
            skLineSegment(sketch, "E7.5.10.1", {"start": v(-60.58, -33) * mm, "end": v(-61.58, -33) * mm});
            skLineSegment(sketch, "E7.5.10.2", {"start": v(-61.58, -34) * mm, "end": v(-60.58, -34) * mm});
            skLineSegment(sketch, "E7.5.10.3", {"start": v(-61.58, -34) * mm, "end": v(-61.58, -33) * mm});
            skLineSegment(sketch, "E7.5.10.4", {"start": v(-60.58, -34) * mm, "end": v(-60.58, -33) * mm});
            skLineSegment(sketch, "E7.5.11.0", {"start": v(-60.6, -32.5) * mm, "end": v(-61.6, -32.5) * mm});
            skLineSegment(sketch, "E7.5.11.1", {"start": v(-60.6, -31.5) * mm, "end": v(-61.6, -31.5) * mm});
            skLineSegment(sketch, "E7.5.11.2", {"start": v(-61.6, -32.5) * mm, "end": v(-60.6, -32.5) * mm});
            skLineSegment(sketch, "E7.5.11.3", {"start": v(-61.6, -32.5) * mm, "end": v(-61.6, -31.5) * mm});
            skLineSegment(sketch, "E7.5.11.4", {"start": v(-60.6, -32.5) * mm, "end": v(-60.6, -31.5) * mm});
            skLineSegment(sketch, "E7.5.12.0", {"start": v(-60.6, -31) * mm, "end": v(-61.6, -31) * mm});
            skLineSegment(sketch, "E7.5.12.1", {"start": v(-60.6, -30) * mm, "end": v(-61.6, -30) * mm});
            skLineSegment(sketch, "E7.5.12.2", {"start": v(-61.6, -31) * mm, "end": v(-60.6, -31) * mm});
            skLineSegment(sketch, "E7.5.12.3", {"start": v(-61.6, -31) * mm, "end": v(-61.6, -30) * mm});
            skLineSegment(sketch, "E7.5.12.4", {"start": v(-60.6, -31) * mm, "end": v(-60.6, -30) * mm});
            skLineSegment(sketch, "E7.5.13.0", {"start": v(-60.6, -29.5) * mm, "end": v(-61.6, -29.5) * mm});
            skLineSegment(sketch, "E7.5.13.1", {"start": v(-60.6, -28.5) * mm, "end": v(-61.6, -28.5) * mm});
            skLineSegment(sketch, "E7.5.13.2", {"start": v(-61.6, -29.5) * mm, "end": v(-60.6, -29.5) * mm});
            skLineSegment(sketch, "E7.5.13.3", {"start": v(-61.6, -29.5) * mm, "end": v(-61.6, -28.5) * mm});
            skLineSegment(sketch, "E7.5.13.4", {"start": v(-60.6, -29.5) * mm, "end": v(-60.6, -28.5) * mm});
            skLineSegment(sketch, "E7.5.14.0", {"start": v(-60.61, -28) * mm, "end": v(-61.61, -28) * mm});
            skLineSegment(sketch, "E7.5.14.1", {"start": v(-60.61, -27) * mm, "end": v(-61.61, -27) * mm});
            skLineSegment(sketch, "E7.5.14.2", {"start": v(-61.61, -28) * mm, "end": v(-60.61, -28) * mm});
            skLineSegment(sketch, "E7.5.14.3", {"start": v(-61.61, -28) * mm, "end": v(-61.61, -27) * mm});
            skLineSegment(sketch, "E7.5.14.4", {"start": v(-60.61, -28) * mm, "end": v(-60.61, -27) * mm});
            skLineSegment(sketch, "E7.5.15.0", {"start": v(-60.62, -26.5) * mm, "end": v(-61.62, -26.5) * mm});
            skLineSegment(sketch, "E7.5.15.1", {"start": v(-60.62, -25.5) * mm, "end": v(-61.62, -25.5) * mm});
            skLineSegment(sketch, "E7.5.15.2", {"start": v(-61.62, -26.5) * mm, "end": v(-60.62, -26.5) * mm});
            skLineSegment(sketch, "E7.5.15.3", {"start": v(-61.62, -26.5) * mm, "end": v(-61.62, -25.5) * mm});
            skLineSegment(sketch, "E7.5.15.4", {"start": v(-60.62, -26.5) * mm, "end": v(-60.62, -25.5) * mm});
            skLineSegment(sketch, "E7.5.16.0", {"start": v(-60.63, -25) * mm, "end": v(-61.63, -25) * mm});
            skLineSegment(sketch, "E7.5.16.1", {"start": v(-60.63, -24) * mm, "end": v(-61.63, -24) * mm});
            skLineSegment(sketch, "E7.5.16.2", {"start": v(-61.63, -25) * mm, "end": v(-60.63, -25) * mm});
            skLineSegment(sketch, "E7.5.16.3", {"start": v(-61.63, -25) * mm, "end": v(-61.63, -24) * mm});
            skLineSegment(sketch, "E7.5.16.4", {"start": v(-60.63, -25) * mm, "end": v(-60.63, -24) * mm});
            skLineSegment(sketch, "E7.5.17.0", {"start": v(-60.64, -23.5) * mm, "end": v(-61.64, -23.5) * mm});
            skLineSegment(sketch, "E7.5.17.1", {"start": v(-60.64, -22.5) * mm, "end": v(-61.64, -22.5) * mm});
            skLineSegment(sketch, "E7.5.17.2", {"start": v(-61.64, -23.5) * mm, "end": v(-60.64, -23.5) * mm});
            skLineSegment(sketch, "E7.5.17.3", {"start": v(-61.64, -23.5) * mm, "end": v(-61.64, -22.5) * mm});
            skLineSegment(sketch, "E7.5.17.4", {"start": v(-60.64, -23.5) * mm, "end": v(-60.64, -22.5) * mm});
            skLineSegment(sketch, "E7.5.18.0", {"start": v(-60.65, -22) * mm, "end": v(-61.65, -22) * mm});
            skLineSegment(sketch, "E7.5.18.1", {"start": v(-60.65, -21) * mm, "end": v(-61.65, -21) * mm});
            skLineSegment(sketch, "E7.5.18.2", {"start": v(-61.65, -22) * mm, "end": v(-60.65, -22) * mm});
            skLineSegment(sketch, "E7.5.18.3", {"start": v(-61.65, -22) * mm, "end": v(-61.65, -21) * mm});
            skLineSegment(sketch, "E7.5.18.4", {"start": v(-60.65, -22) * mm, "end": v(-60.65, -21) * mm});
            skLineSegment(sketch, "E7.5.19.0", {"start": v(-60.66, -20.5) * mm, "end": v(-61.66, -20.5) * mm});
            skLineSegment(sketch, "E7.5.19.1", {"start": v(-60.66, -19.5) * mm, "end": v(-61.66, -19.5) * mm});
            skLineSegment(sketch, "E7.5.19.2", {"start": v(-61.66, -20.5) * mm, "end": v(-60.66, -20.5) * mm});
            skLineSegment(sketch, "E7.5.19.3", {"start": v(-61.66, -20.5) * mm, "end": v(-61.66, -19.5) * mm});
            skLineSegment(sketch, "E7.5.19.4", {"start": v(-60.66, -20.5) * mm, "end": v(-60.66, -19.5) * mm});
            skLineSegment(sketch, "E7.5.20.0", {"start": v(-60.66, -19) * mm, "end": v(-61.66, -19) * mm});
            skLineSegment(sketch, "E7.5.20.1", {"start": v(-60.66, -18) * mm, "end": v(-61.66, -18) * mm});
            skLineSegment(sketch, "E7.5.20.2", {"start": v(-61.66, -19) * mm, "end": v(-60.66, -19) * mm});
            skLineSegment(sketch, "E7.5.20.3", {"start": v(-61.66, -19) * mm, "end": v(-61.66, -18) * mm});
            skLineSegment(sketch, "E7.5.20.4", {"start": v(-60.66, -19) * mm, "end": v(-60.66, -18) * mm});
            skLineSegment(sketch, "E7.5.21.0", {"start": v(-60.67, -17.5) * mm, "end": v(-61.67, -17.5) * mm});
            skLineSegment(sketch, "E7.5.21.1", {"start": v(-60.67, -16.5) * mm, "end": v(-61.67, -16.5) * mm});
            skLineSegment(sketch, "E7.5.21.2", {"start": v(-61.67, -17.5) * mm, "end": v(-60.67, -17.5) * mm});
            skLineSegment(sketch, "E7.5.21.3", {"start": v(-61.67, -17.5) * mm, "end": v(-61.67, -16.5) * mm});
            skLineSegment(sketch, "E7.5.21.4", {"start": v(-60.67, -17.5) * mm, "end": v(-60.67, -16.5) * mm});
            skLineSegment(sketch, "E7.5.22.0", {"start": v(-60.68, -16) * mm, "end": v(-61.68, -16) * mm});
            skLineSegment(sketch, "E7.5.22.1", {"start": v(-60.68, -15) * mm, "end": v(-61.68, -15) * mm});
            skLineSegment(sketch, "E7.5.22.2", {"start": v(-61.68, -16) * mm, "end": v(-60.68, -16) * mm});
            skLineSegment(sketch, "E7.5.22.3", {"start": v(-61.68, -16) * mm, "end": v(-61.68, -15) * mm});
            skLineSegment(sketch, "E7.5.22.4", {"start": v(-60.68, -16) * mm, "end": v(-60.68, -15) * mm});
            skLineSegment(sketch, "E7.5.23.0", {"start": v(-60.69, -14.5) * mm, "end": v(-61.69, -14.5) * mm});
            skLineSegment(sketch, "E7.5.23.1", {"start": v(-60.69, -13.5) * mm, "end": v(-61.69, -13.5) * mm});
            skLineSegment(sketch, "E7.5.23.2", {"start": v(-61.69, -14.5) * mm, "end": v(-60.69, -14.5) * mm});
            skLineSegment(sketch, "E7.5.23.3", {"start": v(-61.69, -14.5) * mm, "end": v(-61.69, -13.5) * mm});
            skLineSegment(sketch, "E7.5.23.4", {"start": v(-60.69, -14.5) * mm, "end": v(-60.69, -13.5) * mm});
            skLineSegment(sketch, "E7.5.24.0", {"start": v(-60.7, -13) * mm, "end": v(-61.7, -13) * mm});
            skLineSegment(sketch, "E7.5.24.1", {"start": v(-60.7, -12) * mm, "end": v(-61.7, -12) * mm});
            skLineSegment(sketch, "E7.5.24.2", {"start": v(-61.7, -13) * mm, "end": v(-60.7, -13) * mm});
            skLineSegment(sketch, "E7.5.24.3", {"start": v(-61.7, -13) * mm, "end": v(-61.7, -12) * mm});
            skLineSegment(sketch, "E7.5.24.4", {"start": v(-60.7, -13) * mm, "end": v(-60.7, -12) * mm});
            skLineSegment(sketch, "E7.5.25.0", {"start": v(-60.7, -11.5) * mm, "end": v(-61.7, -11.5) * mm});
            skLineSegment(sketch, "E7.5.25.1", {"start": v(-60.7, -10.5) * mm, "end": v(-61.7, -10.5) * mm});
            skLineSegment(sketch, "E7.5.25.2", {"start": v(-61.7, -11.5) * mm, "end": v(-60.7, -11.5) * mm});
            skLineSegment(sketch, "E7.5.25.3", {"start": v(-61.7, -11.5) * mm, "end": v(-61.7, -10.5) * mm});
            skLineSegment(sketch, "E7.5.25.4", {"start": v(-60.7, -11.5) * mm, "end": v(-60.7, -10.5) * mm});
            skLineSegment(sketch, "E7.5.26.0", {"start": v(-60.71, -10) * mm, "end": v(-61.71, -10) * mm});
            skLineSegment(sketch, "E7.5.26.1", {"start": v(-60.71, -9) * mm, "end": v(-61.71, -9) * mm});
            skLineSegment(sketch, "E7.5.26.2", {"start": v(-61.71, -10) * mm, "end": v(-60.71, -10) * mm});
            skLineSegment(sketch, "E7.5.26.3", {"start": v(-61.71, -10) * mm, "end": v(-61.71, -9) * mm});
            skLineSegment(sketch, "E7.5.26.4", {"start": v(-60.71, -10) * mm, "end": v(-60.71, -9) * mm});
            skLineSegment(sketch, "E7.5.27.0", {"start": v(-60.72, -8.5) * mm, "end": v(-61.72, -8.5) * mm});
            skLineSegment(sketch, "E7.5.27.1", {"start": v(-60.72, -7.5) * mm, "end": v(-61.72, -7.5) * mm});
            skLineSegment(sketch, "E7.5.27.2", {"start": v(-61.72, -8.5) * mm, "end": v(-60.72, -8.5) * mm});
            skLineSegment(sketch, "E7.5.27.3", {"start": v(-61.72, -8.5) * mm, "end": v(-61.72, -7.5) * mm});
            skLineSegment(sketch, "E7.5.27.4", {"start": v(-60.72, -8.5) * mm, "end": v(-60.72, -7.5) * mm});
            skLineSegment(sketch, "E7.5.28.0", {"start": v(-60.73, -7) * mm, "end": v(-61.73, -7) * mm});
            skLineSegment(sketch, "E7.5.28.1", {"start": v(-60.73, -6) * mm, "end": v(-61.73, -6) * mm});
            skLineSegment(sketch, "E7.5.28.2", {"start": v(-61.73, -7) * mm, "end": v(-60.73, -7) * mm});
            skLineSegment(sketch, "E7.5.28.3", {"start": v(-61.73, -7) * mm, "end": v(-61.73, -6) * mm});
            skLineSegment(sketch, "E7.5.28.4", {"start": v(-60.73, -7) * mm, "end": v(-60.73, -6) * mm});
            skLineSegment(sketch, "E7.5.29.0", {"start": v(-60.74, -5.5) * mm, "end": v(-61.74, -5.5) * mm});
            skLineSegment(sketch, "E7.5.29.1", {"start": v(-60.74, -4.5) * mm, "end": v(-61.74, -4.5) * mm});
            skLineSegment(sketch, "E7.5.29.2", {"start": v(-61.74, -5.5) * mm, "end": v(-60.74, -5.5) * mm});
            skLineSegment(sketch, "E7.5.29.3", {"start": v(-61.74, -5.5) * mm, "end": v(-61.74, -4.5) * mm});
            skLineSegment(sketch, "E7.5.29.4", {"start": v(-60.74, -5.5) * mm, "end": v(-60.74, -4.5) * mm});
            skLineSegment(sketch, "E7.5.30.0", {"start": v(-60.75, -4) * mm, "end": v(-61.75, -4) * mm});
            skLineSegment(sketch, "E7.5.30.1", {"start": v(-60.75, -3) * mm, "end": v(-61.75, -3) * mm});
            skLineSegment(sketch, "E7.5.30.2", {"start": v(-61.75, -4) * mm, "end": v(-60.75, -4) * mm});
            skLineSegment(sketch, "E7.5.30.3", {"start": v(-61.75, -4) * mm, "end": v(-61.75, -3) * mm});
            skLineSegment(sketch, "E7.5.30.4", {"start": v(-60.75, -4) * mm, "end": v(-60.75, -3) * mm});
            skLineSegment(sketch, "E7.6.0.0", {"start": v(-59, -49) * mm, "end": v(-60, -49) * mm});
            skLineSegment(sketch, "E7.6.0.1", {"start": v(-59, -48) * mm, "end": v(-60, -48) * mm});
            skLineSegment(sketch, "E7.6.0.2", {"start": v(-60, -49) * mm, "end": v(-59, -49) * mm});
            skLineSegment(sketch, "E7.6.0.3", {"start": v(-60, -49) * mm, "end": v(-60, -48) * mm});
            skLineSegment(sketch, "E7.6.0.4", {"start": v(-59, -49) * mm, "end": v(-59, -48) * mm});
            skLineSegment(sketch, "E7.6.1.0", {"start": v(-59, -47.5) * mm, "end": v(-60, -47.5) * mm});
            skLineSegment(sketch, "E7.6.1.1", {"start": v(-59, -46.5) * mm, "end": v(-60, -46.5) * mm});
            skLineSegment(sketch, "E7.6.1.2", {"start": v(-60, -47.5) * mm, "end": v(-59, -47.5) * mm});
            skLineSegment(sketch, "E7.6.1.3", {"start": v(-60, -47.5) * mm, "end": v(-60, -46.5) * mm});
            skLineSegment(sketch, "E7.6.1.4", {"start": v(-59, -47.5) * mm, "end": v(-59, -46.5) * mm});
            skLineSegment(sketch, "E7.6.2.0", {"start": v(-59.02, -46) * mm, "end": v(-60.02, -46) * mm});
            skLineSegment(sketch, "E7.6.2.1", {"start": v(-59.02, -45) * mm, "end": v(-60.02, -45) * mm});
            skLineSegment(sketch, "E7.6.2.2", {"start": v(-60.02, -46) * mm, "end": v(-59.02, -46) * mm});
            skLineSegment(sketch, "E7.6.2.3", {"start": v(-60.02, -46) * mm, "end": v(-60.02, -45) * mm});
            skLineSegment(sketch, "E7.6.2.4", {"start": v(-59.02, -46) * mm, "end": v(-59.02, -45) * mm});
            skLineSegment(sketch, "E7.6.3.0", {"start": v(-59.02, -44.5) * mm, "end": v(-60.02, -44.5) * mm});
            skLineSegment(sketch, "E7.6.3.1", {"start": v(-59.02, -43.5) * mm, "end": v(-60.02, -43.5) * mm});
            skLineSegment(sketch, "E7.6.3.2", {"start": v(-60.02, -44.5) * mm, "end": v(-59.02, -44.5) * mm});
            skLineSegment(sketch, "E7.6.3.3", {"start": v(-60.02, -44.5) * mm, "end": v(-60.02, -43.5) * mm});
            skLineSegment(sketch, "E7.6.3.4", {"start": v(-59.02, -44.5) * mm, "end": v(-59.02, -43.5) * mm});
            skLineSegment(sketch, "E7.6.4.0", {"start": v(-59.03, -43) * mm, "end": v(-60.03, -43) * mm});
            skLineSegment(sketch, "E7.6.4.1", {"start": v(-59.03, -42) * mm, "end": v(-60.03, -42) * mm});
            skLineSegment(sketch, "E7.6.4.2", {"start": v(-60.03, -43) * mm, "end": v(-59.03, -43) * mm});
            skLineSegment(sketch, "E7.6.4.3", {"start": v(-60.03, -43) * mm, "end": v(-60.03, -42) * mm});
            skLineSegment(sketch, "E7.6.4.4", {"start": v(-59.03, -43) * mm, "end": v(-59.03, -42) * mm});
            skLineSegment(sketch, "E7.6.5.0", {"start": v(-59.04, -41.5) * mm, "end": v(-60.04, -41.5) * mm});
            skLineSegment(sketch, "E7.6.5.1", {"start": v(-59.04, -40.5) * mm, "end": v(-60.04, -40.5) * mm});
            skLineSegment(sketch, "E7.6.5.2", {"start": v(-60.04, -41.5) * mm, "end": v(-59.04, -41.5) * mm});
            skLineSegment(sketch, "E7.6.5.3", {"start": v(-60.04, -41.5) * mm, "end": v(-60.04, -40.5) * mm});
            skLineSegment(sketch, "E7.6.5.4", {"start": v(-59.04, -41.5) * mm, "end": v(-59.04, -40.5) * mm});
            skLineSegment(sketch, "E7.6.6.0", {"start": v(-59.05, -40) * mm, "end": v(-60.05, -40) * mm});
            skLineSegment(sketch, "E7.6.6.1", {"start": v(-59.05, -39) * mm, "end": v(-60.05, -39) * mm});
            skLineSegment(sketch, "E7.6.6.2", {"start": v(-60.05, -40) * mm, "end": v(-59.05, -40) * mm});
            skLineSegment(sketch, "E7.6.6.3", {"start": v(-60.05, -40) * mm, "end": v(-60.05, -39) * mm});
            skLineSegment(sketch, "E7.6.6.4", {"start": v(-59.05, -40) * mm, "end": v(-59.05, -39) * mm});
            skLineSegment(sketch, "E7.6.7.0", {"start": v(-59.06, -38.5) * mm, "end": v(-60.06, -38.5) * mm});
            skLineSegment(sketch, "E7.6.7.1", {"start": v(-59.06, -37.5) * mm, "end": v(-60.06, -37.5) * mm});
            skLineSegment(sketch, "E7.6.7.2", {"start": v(-60.06, -38.5) * mm, "end": v(-59.06, -38.5) * mm});
            skLineSegment(sketch, "E7.6.7.3", {"start": v(-60.06, -38.5) * mm, "end": v(-60.06, -37.5) * mm});
            skLineSegment(sketch, "E7.6.7.4", {"start": v(-59.06, -38.5) * mm, "end": v(-59.06, -37.5) * mm});
            skLineSegment(sketch, "E7.6.8.0", {"start": v(-59.07, -37) * mm, "end": v(-60.07, -37) * mm});
            skLineSegment(sketch, "E7.6.8.1", {"start": v(-59.07, -36) * mm, "end": v(-60.07, -36) * mm});
            skLineSegment(sketch, "E7.6.8.2", {"start": v(-60.07, -37) * mm, "end": v(-59.07, -37) * mm});
            skLineSegment(sketch, "E7.6.8.3", {"start": v(-60.07, -37) * mm, "end": v(-60.07, -36) * mm});
            skLineSegment(sketch, "E7.6.8.4", {"start": v(-59.07, -37) * mm, "end": v(-59.07, -36) * mm});
            skLineSegment(sketch, "E7.6.9.0", {"start": v(-59.07, -35.5) * mm, "end": v(-60.07, -35.5) * mm});
            skLineSegment(sketch, "E7.6.9.1", {"start": v(-59.07, -34.5) * mm, "end": v(-60.07, -34.5) * mm});
            skLineSegment(sketch, "E7.6.9.2", {"start": v(-60.07, -35.5) * mm, "end": v(-59.07, -35.5) * mm});
            skLineSegment(sketch, "E7.6.9.3", {"start": v(-60.07, -35.5) * mm, "end": v(-60.07, -34.5) * mm});
            skLineSegment(sketch, "E7.6.9.4", {"start": v(-59.07, -35.5) * mm, "end": v(-59.07, -34.5) * mm});
            skLineSegment(sketch, "E7.6.10.0", {"start": v(-59.08, -34) * mm, "end": v(-60.08, -34) * mm});
            skLineSegment(sketch, "E7.6.10.1", {"start": v(-59.08, -33) * mm, "end": v(-60.08, -33) * mm});
            skLineSegment(sketch, "E7.6.10.2", {"start": v(-60.08, -34) * mm, "end": v(-59.08, -34) * mm});
            skLineSegment(sketch, "E7.6.10.3", {"start": v(-60.08, -34) * mm, "end": v(-60.08, -33) * mm});
            skLineSegment(sketch, "E7.6.10.4", {"start": v(-59.08, -34) * mm, "end": v(-59.08, -33) * mm});
            skLineSegment(sketch, "E7.6.11.0", {"start": v(-59.1, -32.5) * mm, "end": v(-60.1, -32.5) * mm});
            skLineSegment(sketch, "E7.6.11.1", {"start": v(-59.1, -31.5) * mm, "end": v(-60.1, -31.5) * mm});
            skLineSegment(sketch, "E7.6.11.2", {"start": v(-60.1, -32.5) * mm, "end": v(-59.1, -32.5) * mm});
            skLineSegment(sketch, "E7.6.11.3", {"start": v(-60.1, -32.5) * mm, "end": v(-60.1, -31.5) * mm});
            skLineSegment(sketch, "E7.6.11.4", {"start": v(-59.1, -32.5) * mm, "end": v(-59.1, -31.5) * mm});
            skLineSegment(sketch, "E7.6.12.0", {"start": v(-59.1, -31) * mm, "end": v(-60.1, -31) * mm});
            skLineSegment(sketch, "E7.6.12.1", {"start": v(-59.1, -30) * mm, "end": v(-60.1, -30) * mm});
            skLineSegment(sketch, "E7.6.12.2", {"start": v(-60.1, -31) * mm, "end": v(-59.1, -31) * mm});
            skLineSegment(sketch, "E7.6.12.3", {"start": v(-60.1, -31) * mm, "end": v(-60.1, -30) * mm});
            skLineSegment(sketch, "E7.6.12.4", {"start": v(-59.1, -31) * mm, "end": v(-59.1, -30) * mm});
            skLineSegment(sketch, "E7.6.13.0", {"start": v(-59.1, -29.5) * mm, "end": v(-60.1, -29.5) * mm});
            skLineSegment(sketch, "E7.6.13.1", {"start": v(-59.1, -28.5) * mm, "end": v(-60.1, -28.5) * mm});
            skLineSegment(sketch, "E7.6.13.2", {"start": v(-60.1, -29.5) * mm, "end": v(-59.1, -29.5) * mm});
            skLineSegment(sketch, "E7.6.13.3", {"start": v(-60.1, -29.5) * mm, "end": v(-60.1, -28.5) * mm});
            skLineSegment(sketch, "E7.6.13.4", {"start": v(-59.1, -29.5) * mm, "end": v(-59.1, -28.5) * mm});
            skLineSegment(sketch, "E7.6.14.0", {"start": v(-59.11, -28) * mm, "end": v(-60.11, -28) * mm});
            skLineSegment(sketch, "E7.6.14.1", {"start": v(-59.11, -27) * mm, "end": v(-60.11, -27) * mm});
            skLineSegment(sketch, "E7.6.14.2", {"start": v(-60.11, -28) * mm, "end": v(-59.11, -28) * mm});
            skLineSegment(sketch, "E7.6.14.3", {"start": v(-60.11, -28) * mm, "end": v(-60.11, -27) * mm});
            skLineSegment(sketch, "E7.6.14.4", {"start": v(-59.11, -28) * mm, "end": v(-59.11, -27) * mm});
            skLineSegment(sketch, "E7.6.15.0", {"start": v(-59.12, -26.5) * mm, "end": v(-60.12, -26.5) * mm});
            skLineSegment(sketch, "E7.6.15.1", {"start": v(-59.12, -25.5) * mm, "end": v(-60.12, -25.5) * mm});
            skLineSegment(sketch, "E7.6.15.2", {"start": v(-60.12, -26.5) * mm, "end": v(-59.12, -26.5) * mm});
            skLineSegment(sketch, "E7.6.15.3", {"start": v(-60.12, -26.5) * mm, "end": v(-60.12, -25.5) * mm});
            skLineSegment(sketch, "E7.6.15.4", {"start": v(-59.12, -26.5) * mm, "end": v(-59.12, -25.5) * mm});
            skLineSegment(sketch, "E7.6.16.0", {"start": v(-59.13, -25) * mm, "end": v(-60.13, -25) * mm});
            skLineSegment(sketch, "E7.6.16.1", {"start": v(-59.13, -24) * mm, "end": v(-60.13, -24) * mm});
            skLineSegment(sketch, "E7.6.16.2", {"start": v(-60.13, -25) * mm, "end": v(-59.13, -25) * mm});
            skLineSegment(sketch, "E7.6.16.3", {"start": v(-60.13, -25) * mm, "end": v(-60.13, -24) * mm});
            skLineSegment(sketch, "E7.6.16.4", {"start": v(-59.13, -25) * mm, "end": v(-59.13, -24) * mm});
            skLineSegment(sketch, "E7.6.17.0", {"start": v(-59.14, -23.5) * mm, "end": v(-60.14, -23.5) * mm});
            skLineSegment(sketch, "E7.6.17.1", {"start": v(-59.14, -22.5) * mm, "end": v(-60.14, -22.5) * mm});
            skLineSegment(sketch, "E7.6.17.2", {"start": v(-60.14, -23.5) * mm, "end": v(-59.14, -23.5) * mm});
            skLineSegment(sketch, "E7.6.17.3", {"start": v(-60.14, -23.5) * mm, "end": v(-60.14, -22.5) * mm});
            skLineSegment(sketch, "E7.6.17.4", {"start": v(-59.14, -23.5) * mm, "end": v(-59.14, -22.5) * mm});
            skLineSegment(sketch, "E7.6.18.0", {"start": v(-59.15, -22) * mm, "end": v(-60.15, -22) * mm});
            skLineSegment(sketch, "E7.6.18.1", {"start": v(-59.15, -21) * mm, "end": v(-60.15, -21) * mm});
            skLineSegment(sketch, "E7.6.18.2", {"start": v(-60.15, -22) * mm, "end": v(-59.15, -22) * mm});
            skLineSegment(sketch, "E7.6.18.3", {"start": v(-60.15, -22) * mm, "end": v(-60.15, -21) * mm});
            skLineSegment(sketch, "E7.6.18.4", {"start": v(-59.15, -22) * mm, "end": v(-59.15, -21) * mm});
            skLineSegment(sketch, "E7.6.19.0", {"start": v(-59.16, -20.5) * mm, "end": v(-60.16, -20.5) * mm});
            skLineSegment(sketch, "E7.6.19.1", {"start": v(-59.16, -19.5) * mm, "end": v(-60.16, -19.5) * mm});
            skLineSegment(sketch, "E7.6.19.2", {"start": v(-60.16, -20.5) * mm, "end": v(-59.16, -20.5) * mm});
            skLineSegment(sketch, "E7.6.19.3", {"start": v(-60.16, -20.5) * mm, "end": v(-60.16, -19.5) * mm});
            skLineSegment(sketch, "E7.6.19.4", {"start": v(-59.16, -20.5) * mm, "end": v(-59.16, -19.5) * mm});
            skLineSegment(sketch, "E7.6.20.0", {"start": v(-59.16, -19) * mm, "end": v(-60.16, -19) * mm});
            skLineSegment(sketch, "E7.6.20.1", {"start": v(-59.16, -18) * mm, "end": v(-60.16, -18) * mm});
            skLineSegment(sketch, "E7.6.20.2", {"start": v(-60.16, -19) * mm, "end": v(-59.16, -19) * mm});
            skLineSegment(sketch, "E7.6.20.3", {"start": v(-60.16, -19) * mm, "end": v(-60.16, -18) * mm});
            skLineSegment(sketch, "E7.6.20.4", {"start": v(-59.16, -19) * mm, "end": v(-59.16, -18) * mm});
            skLineSegment(sketch, "E7.6.21.0", {"start": v(-59.17, -17.5) * mm, "end": v(-60.17, -17.5) * mm});
            skLineSegment(sketch, "E7.6.21.1", {"start": v(-59.17, -16.5) * mm, "end": v(-60.17, -16.5) * mm});
            skLineSegment(sketch, "E7.6.21.2", {"start": v(-60.17, -17.5) * mm, "end": v(-59.17, -17.5) * mm});
            skLineSegment(sketch, "E7.6.21.3", {"start": v(-60.17, -17.5) * mm, "end": v(-60.17, -16.5) * mm});
            skLineSegment(sketch, "E7.6.21.4", {"start": v(-59.17, -17.5) * mm, "end": v(-59.17, -16.5) * mm});
            skLineSegment(sketch, "E7.6.22.0", {"start": v(-59.18, -16) * mm, "end": v(-60.18, -16) * mm});
            skLineSegment(sketch, "E7.6.22.1", {"start": v(-59.18, -15) * mm, "end": v(-60.18, -15) * mm});
            skLineSegment(sketch, "E7.6.22.2", {"start": v(-60.18, -16) * mm, "end": v(-59.18, -16) * mm});
            skLineSegment(sketch, "E7.6.22.3", {"start": v(-60.18, -16) * mm, "end": v(-60.18, -15) * mm});
            skLineSegment(sketch, "E7.6.22.4", {"start": v(-59.18, -16) * mm, "end": v(-59.18, -15) * mm});
            skLineSegment(sketch, "E7.6.23.0", {"start": v(-59.19, -14.5) * mm, "end": v(-60.19, -14.5) * mm});
            skLineSegment(sketch, "E7.6.23.1", {"start": v(-59.19, -13.5) * mm, "end": v(-60.19, -13.5) * mm});
            skLineSegment(sketch, "E7.6.23.2", {"start": v(-60.19, -14.5) * mm, "end": v(-59.19, -14.5) * mm});
            skLineSegment(sketch, "E7.6.23.3", {"start": v(-60.19, -14.5) * mm, "end": v(-60.19, -13.5) * mm});
            skLineSegment(sketch, "E7.6.23.4", {"start": v(-59.19, -14.5) * mm, "end": v(-59.19, -13.5) * mm});
            skLineSegment(sketch, "E7.6.24.0", {"start": v(-59.2, -13) * mm, "end": v(-60.2, -13) * mm});
            skLineSegment(sketch, "E7.6.24.1", {"start": v(-59.2, -12) * mm, "end": v(-60.2, -12) * mm});
            skLineSegment(sketch, "E7.6.24.2", {"start": v(-60.2, -13) * mm, "end": v(-59.2, -13) * mm});
            skLineSegment(sketch, "E7.6.24.3", {"start": v(-60.2, -13) * mm, "end": v(-60.2, -12) * mm});
            skLineSegment(sketch, "E7.6.24.4", {"start": v(-59.2, -13) * mm, "end": v(-59.2, -12) * mm});
            skLineSegment(sketch, "E7.6.25.0", {"start": v(-59.2, -11.5) * mm, "end": v(-60.2, -11.5) * mm});
            skLineSegment(sketch, "E7.6.25.1", {"start": v(-59.2, -10.5) * mm, "end": v(-60.2, -10.5) * mm});
            skLineSegment(sketch, "E7.6.25.2", {"start": v(-60.2, -11.5) * mm, "end": v(-59.2, -11.5) * mm});
            skLineSegment(sketch, "E7.6.25.3", {"start": v(-60.2, -11.5) * mm, "end": v(-60.2, -10.5) * mm});
            skLineSegment(sketch, "E7.6.25.4", {"start": v(-59.2, -11.5) * mm, "end": v(-59.2, -10.5) * mm});
            skLineSegment(sketch, "E7.6.26.0", {"start": v(-59.21, -10) * mm, "end": v(-60.21, -10) * mm});
            skLineSegment(sketch, "E7.6.26.1", {"start": v(-59.21, -9) * mm, "end": v(-60.21, -9) * mm});
            skLineSegment(sketch, "E7.6.26.2", {"start": v(-60.21, -10) * mm, "end": v(-59.21, -10) * mm});
            skLineSegment(sketch, "E7.6.26.3", {"start": v(-60.21, -10) * mm, "end": v(-60.21, -9) * mm});
            skLineSegment(sketch, "E7.6.26.4", {"start": v(-59.21, -10) * mm, "end": v(-59.21, -9) * mm});
            skLineSegment(sketch, "E7.6.27.0", {"start": v(-59.22, -8.5) * mm, "end": v(-60.22, -8.5) * mm});
            skLineSegment(sketch, "E7.6.27.1", {"start": v(-59.22, -7.5) * mm, "end": v(-60.22, -7.5) * mm});
            skLineSegment(sketch, "E7.6.27.2", {"start": v(-60.22, -8.5) * mm, "end": v(-59.22, -8.5) * mm});
            skLineSegment(sketch, "E7.6.27.3", {"start": v(-60.22, -8.5) * mm, "end": v(-60.22, -7.5) * mm});
            skLineSegment(sketch, "E7.6.27.4", {"start": v(-59.22, -8.5) * mm, "end": v(-59.22, -7.5) * mm});
            skLineSegment(sketch, "E7.6.28.0", {"start": v(-59.23, -7) * mm, "end": v(-60.23, -7) * mm});
            skLineSegment(sketch, "E7.6.28.1", {"start": v(-59.23, -6) * mm, "end": v(-60.23, -6) * mm});
            skLineSegment(sketch, "E7.6.28.2", {"start": v(-60.23, -7) * mm, "end": v(-59.23, -7) * mm});
            skLineSegment(sketch, "E7.6.28.3", {"start": v(-60.23, -7) * mm, "end": v(-60.23, -6) * mm});
            skLineSegment(sketch, "E7.6.28.4", {"start": v(-59.23, -7) * mm, "end": v(-59.23, -6) * mm});
            skLineSegment(sketch, "E7.6.29.0", {"start": v(-59.24, -5.5) * mm, "end": v(-60.24, -5.5) * mm});
            skLineSegment(sketch, "E7.6.29.1", {"start": v(-59.24, -4.5) * mm, "end": v(-60.24, -4.5) * mm});
            skLineSegment(sketch, "E7.6.29.2", {"start": v(-60.24, -5.5) * mm, "end": v(-59.24, -5.5) * mm});
            skLineSegment(sketch, "E7.6.29.3", {"start": v(-60.24, -5.5) * mm, "end": v(-60.24, -4.5) * mm});
            skLineSegment(sketch, "E7.6.29.4", {"start": v(-59.24, -5.5) * mm, "end": v(-59.24, -4.5) * mm});
            skLineSegment(sketch, "E7.6.30.0", {"start": v(-59.25, -4) * mm, "end": v(-60.25, -4) * mm});
            skLineSegment(sketch, "E7.6.30.1", {"start": v(-59.25, -3) * mm, "end": v(-60.25, -3) * mm});
            skLineSegment(sketch, "E7.6.30.2", {"start": v(-60.25, -4) * mm, "end": v(-59.25, -4) * mm});
            skLineSegment(sketch, "E7.6.30.3", {"start": v(-60.25, -4) * mm, "end": v(-60.25, -3) * mm});
            skLineSegment(sketch, "E7.6.30.4", {"start": v(-59.25, -4) * mm, "end": v(-59.25, -3) * mm});
            skLineSegment(sketch, "E7.7.0.0", {"start": v(-57.5, -49) * mm, "end": v(-58.5, -49) * mm});
            skLineSegment(sketch, "E7.7.0.1", {"start": v(-57.5, -48) * mm, "end": v(-58.5, -48) * mm});
            skLineSegment(sketch, "E7.7.0.2", {"start": v(-58.5, -49) * mm, "end": v(-57.5, -49) * mm});
            skLineSegment(sketch, "E7.7.0.3", {"start": v(-58.5, -49) * mm, "end": v(-58.5, -48) * mm});
            skLineSegment(sketch, "E7.7.0.4", {"start": v(-57.5, -49) * mm, "end": v(-57.5, -48) * mm});
            skLineSegment(sketch, "E7.7.1.0", {"start": v(-57.5, -47.5) * mm, "end": v(-58.5, -47.5) * mm});
            skLineSegment(sketch, "E7.7.1.1", {"start": v(-57.5, -46.5) * mm, "end": v(-58.5, -46.5) * mm});
            skLineSegment(sketch, "E7.7.1.2", {"start": v(-58.5, -47.5) * mm, "end": v(-57.5, -47.5) * mm});
            skLineSegment(sketch, "E7.7.1.3", {"start": v(-58.5, -47.5) * mm, "end": v(-58.5, -46.5) * mm});
            skLineSegment(sketch, "E7.7.1.4", {"start": v(-57.5, -47.5) * mm, "end": v(-57.5, -46.5) * mm});
            skLineSegment(sketch, "E7.7.2.0", {"start": v(-57.52, -46) * mm, "end": v(-58.52, -46) * mm});
            skLineSegment(sketch, "E7.7.2.1", {"start": v(-57.52, -45) * mm, "end": v(-58.52, -45) * mm});
            skLineSegment(sketch, "E7.7.2.2", {"start": v(-58.52, -46) * mm, "end": v(-57.52, -46) * mm});
            skLineSegment(sketch, "E7.7.2.3", {"start": v(-58.52, -46) * mm, "end": v(-58.52, -45) * mm});
            skLineSegment(sketch, "E7.7.2.4", {"start": v(-57.52, -46) * mm, "end": v(-57.52, -45) * mm});
            skLineSegment(sketch, "E7.7.3.0", {"start": v(-57.52, -44.5) * mm, "end": v(-58.52, -44.5) * mm});
            skLineSegment(sketch, "E7.7.3.1", {"start": v(-57.52, -43.5) * mm, "end": v(-58.52, -43.5) * mm});
            skLineSegment(sketch, "E7.7.3.2", {"start": v(-58.52, -44.5) * mm, "end": v(-57.52, -44.5) * mm});
            skLineSegment(sketch, "E7.7.3.3", {"start": v(-58.52, -44.5) * mm, "end": v(-58.52, -43.5) * mm});
            skLineSegment(sketch, "E7.7.3.4", {"start": v(-57.52, -44.5) * mm, "end": v(-57.52, -43.5) * mm});
            skLineSegment(sketch, "E7.7.4.0", {"start": v(-57.53, -43) * mm, "end": v(-58.53, -43) * mm});
            skLineSegment(sketch, "E7.7.4.1", {"start": v(-57.53, -42) * mm, "end": v(-58.53, -42) * mm});
            skLineSegment(sketch, "E7.7.4.2", {"start": v(-58.53, -43) * mm, "end": v(-57.53, -43) * mm});
            skLineSegment(sketch, "E7.7.4.3", {"start": v(-58.53, -43) * mm, "end": v(-58.53, -42) * mm});
            skLineSegment(sketch, "E7.7.4.4", {"start": v(-57.53, -43) * mm, "end": v(-57.53, -42) * mm});
            skLineSegment(sketch, "E7.7.5.0", {"start": v(-57.54, -41.5) * mm, "end": v(-58.54, -41.5) * mm});
            skLineSegment(sketch, "E7.7.5.1", {"start": v(-57.54, -40.5) * mm, "end": v(-58.54, -40.5) * mm});
            skLineSegment(sketch, "E7.7.5.2", {"start": v(-58.54, -41.5) * mm, "end": v(-57.54, -41.5) * mm});
            skLineSegment(sketch, "E7.7.5.3", {"start": v(-58.54, -41.5) * mm, "end": v(-58.54, -40.5) * mm});
            skLineSegment(sketch, "E7.7.5.4", {"start": v(-57.54, -41.5) * mm, "end": v(-57.54, -40.5) * mm});
            skLineSegment(sketch, "E7.7.6.0", {"start": v(-57.55, -40) * mm, "end": v(-58.55, -40) * mm});
            skLineSegment(sketch, "E7.7.6.1", {"start": v(-57.55, -39) * mm, "end": v(-58.55, -39) * mm});
            skLineSegment(sketch, "E7.7.6.2", {"start": v(-58.55, -40) * mm, "end": v(-57.55, -40) * mm});
            skLineSegment(sketch, "E7.7.6.3", {"start": v(-58.55, -40) * mm, "end": v(-58.55, -39) * mm});
            skLineSegment(sketch, "E7.7.6.4", {"start": v(-57.55, -40) * mm, "end": v(-57.55, -39) * mm});
            skLineSegment(sketch, "E7.7.7.0", {"start": v(-57.56, -38.5) * mm, "end": v(-58.56, -38.5) * mm});
            skLineSegment(sketch, "E7.7.7.1", {"start": v(-57.56, -37.5) * mm, "end": v(-58.56, -37.5) * mm});
            skLineSegment(sketch, "E7.7.7.2", {"start": v(-58.56, -38.5) * mm, "end": v(-57.56, -38.5) * mm});
            skLineSegment(sketch, "E7.7.7.3", {"start": v(-58.56, -38.5) * mm, "end": v(-58.56, -37.5) * mm});
            skLineSegment(sketch, "E7.7.7.4", {"start": v(-57.56, -38.5) * mm, "end": v(-57.56, -37.5) * mm});
            skLineSegment(sketch, "E7.7.8.0", {"start": v(-57.57, -37) * mm, "end": v(-58.57, -37) * mm});
            skLineSegment(sketch, "E7.7.8.1", {"start": v(-57.57, -36) * mm, "end": v(-58.57, -36) * mm});
            skLineSegment(sketch, "E7.7.8.2", {"start": v(-58.57, -37) * mm, "end": v(-57.57, -37) * mm});
            skLineSegment(sketch, "E7.7.8.3", {"start": v(-58.57, -37) * mm, "end": v(-58.57, -36) * mm});
            skLineSegment(sketch, "E7.7.8.4", {"start": v(-57.57, -37) * mm, "end": v(-57.57, -36) * mm});
            skLineSegment(sketch, "E7.7.9.0", {"start": v(-57.57, -35.5) * mm, "end": v(-58.57, -35.5) * mm});
            skLineSegment(sketch, "E7.7.9.1", {"start": v(-57.57, -34.5) * mm, "end": v(-58.57, -34.5) * mm});
            skLineSegment(sketch, "E7.7.9.2", {"start": v(-58.57, -35.5) * mm, "end": v(-57.57, -35.5) * mm});
            skLineSegment(sketch, "E7.7.9.3", {"start": v(-58.57, -35.5) * mm, "end": v(-58.57, -34.5) * mm});
            skLineSegment(sketch, "E7.7.9.4", {"start": v(-57.57, -35.5) * mm, "end": v(-57.57, -34.5) * mm});
            skLineSegment(sketch, "E7.7.10.0", {"start": v(-57.58, -34) * mm, "end": v(-58.58, -34) * mm});
            skLineSegment(sketch, "E7.7.10.1", {"start": v(-57.58, -33) * mm, "end": v(-58.58, -33) * mm});
            skLineSegment(sketch, "E7.7.10.2", {"start": v(-58.58, -34) * mm, "end": v(-57.58, -34) * mm});
            skLineSegment(sketch, "E7.7.10.3", {"start": v(-58.58, -34) * mm, "end": v(-58.58, -33) * mm});
            skLineSegment(sketch, "E7.7.10.4", {"start": v(-57.58, -34) * mm, "end": v(-57.58, -33) * mm});
            skLineSegment(sketch, "E7.7.11.0", {"start": v(-57.6, -32.5) * mm, "end": v(-58.6, -32.5) * mm});
            skLineSegment(sketch, "E7.7.11.1", {"start": v(-57.6, -31.5) * mm, "end": v(-58.6, -31.5) * mm});
            skLineSegment(sketch, "E7.7.11.2", {"start": v(-58.6, -32.5) * mm, "end": v(-57.6, -32.5) * mm});
            skLineSegment(sketch, "E7.7.11.3", {"start": v(-58.6, -32.5) * mm, "end": v(-58.6, -31.5) * mm});
            skLineSegment(sketch, "E7.7.11.4", {"start": v(-57.6, -32.5) * mm, "end": v(-57.6, -31.5) * mm});
            skLineSegment(sketch, "E7.7.12.0", {"start": v(-57.6, -31) * mm, "end": v(-58.6, -31) * mm});
            skLineSegment(sketch, "E7.7.12.1", {"start": v(-57.6, -30) * mm, "end": v(-58.6, -30) * mm});
            skLineSegment(sketch, "E7.7.12.2", {"start": v(-58.6, -31) * mm, "end": v(-57.6, -31) * mm});
            skLineSegment(sketch, "E7.7.12.3", {"start": v(-58.6, -31) * mm, "end": v(-58.6, -30) * mm});
            skLineSegment(sketch, "E7.7.12.4", {"start": v(-57.6, -31) * mm, "end": v(-57.6, -30) * mm});
            skLineSegment(sketch, "E7.7.13.0", {"start": v(-57.6, -29.5) * mm, "end": v(-58.6, -29.5) * mm});
            skLineSegment(sketch, "E7.7.13.1", {"start": v(-57.6, -28.5) * mm, "end": v(-58.6, -28.5) * mm});
            skLineSegment(sketch, "E7.7.13.2", {"start": v(-58.6, -29.5) * mm, "end": v(-57.6, -29.5) * mm});
            skLineSegment(sketch, "E7.7.13.3", {"start": v(-58.6, -29.5) * mm, "end": v(-58.6, -28.5) * mm});
            skLineSegment(sketch, "E7.7.13.4", {"start": v(-57.6, -29.5) * mm, "end": v(-57.6, -28.5) * mm});
            skLineSegment(sketch, "E7.7.14.0", {"start": v(-57.61, -28) * mm, "end": v(-58.61, -28) * mm});
            skLineSegment(sketch, "E7.7.14.1", {"start": v(-57.61, -27) * mm, "end": v(-58.61, -27) * mm});
            skLineSegment(sketch, "E7.7.14.2", {"start": v(-58.61, -28) * mm, "end": v(-57.61, -28) * mm});
            skLineSegment(sketch, "E7.7.14.3", {"start": v(-58.61, -28) * mm, "end": v(-58.61, -27) * mm});
            skLineSegment(sketch, "E7.7.14.4", {"start": v(-57.61, -28) * mm, "end": v(-57.61, -27) * mm});
            skLineSegment(sketch, "E7.7.15.0", {"start": v(-57.62, -26.5) * mm, "end": v(-58.62, -26.5) * mm});
            skLineSegment(sketch, "E7.7.15.1", {"start": v(-57.62, -25.5) * mm, "end": v(-58.62, -25.5) * mm});
            skLineSegment(sketch, "E7.7.15.2", {"start": v(-58.62, -26.5) * mm, "end": v(-57.62, -26.5) * mm});
            skLineSegment(sketch, "E7.7.15.3", {"start": v(-58.62, -26.5) * mm, "end": v(-58.62, -25.5) * mm});
            skLineSegment(sketch, "E7.7.15.4", {"start": v(-57.62, -26.5) * mm, "end": v(-57.62, -25.5) * mm});
            skLineSegment(sketch, "E7.7.16.0", {"start": v(-57.63, -25) * mm, "end": v(-58.63, -25) * mm});
            skLineSegment(sketch, "E7.7.16.1", {"start": v(-57.63, -24) * mm, "end": v(-58.63, -24) * mm});
            skLineSegment(sketch, "E7.7.16.2", {"start": v(-58.63, -25) * mm, "end": v(-57.63, -25) * mm});
            skLineSegment(sketch, "E7.7.16.3", {"start": v(-58.63, -25) * mm, "end": v(-58.63, -24) * mm});
            skLineSegment(sketch, "E7.7.16.4", {"start": v(-57.63, -25) * mm, "end": v(-57.63, -24) * mm});
            skLineSegment(sketch, "E7.7.17.0", {"start": v(-57.64, -23.5) * mm, "end": v(-58.64, -23.5) * mm});
            skLineSegment(sketch, "E7.7.17.1", {"start": v(-57.64, -22.5) * mm, "end": v(-58.64, -22.5) * mm});
            skLineSegment(sketch, "E7.7.17.2", {"start": v(-58.64, -23.5) * mm, "end": v(-57.64, -23.5) * mm});
            skLineSegment(sketch, "E7.7.17.3", {"start": v(-58.64, -23.5) * mm, "end": v(-58.64, -22.5) * mm});
            skLineSegment(sketch, "E7.7.17.4", {"start": v(-57.64, -23.5) * mm, "end": v(-57.64, -22.5) * mm});
            skLineSegment(sketch, "E7.7.18.0", {"start": v(-57.65, -22) * mm, "end": v(-58.65, -22) * mm});
            skLineSegment(sketch, "E7.7.18.1", {"start": v(-57.65, -21) * mm, "end": v(-58.65, -21) * mm});
            skLineSegment(sketch, "E7.7.18.2", {"start": v(-58.65, -22) * mm, "end": v(-57.65, -22) * mm});
            skLineSegment(sketch, "E7.7.18.3", {"start": v(-58.65, -22) * mm, "end": v(-58.65, -21) * mm});
            skLineSegment(sketch, "E7.7.18.4", {"start": v(-57.65, -22) * mm, "end": v(-57.65, -21) * mm});
            skLineSegment(sketch, "E7.7.19.0", {"start": v(-57.66, -20.5) * mm, "end": v(-58.66, -20.5) * mm});
            skLineSegment(sketch, "E7.7.19.1", {"start": v(-57.66, -19.5) * mm, "end": v(-58.66, -19.5) * mm});
            skLineSegment(sketch, "E7.7.19.2", {"start": v(-58.66, -20.5) * mm, "end": v(-57.66, -20.5) * mm});
            skLineSegment(sketch, "E7.7.19.3", {"start": v(-58.66, -20.5) * mm, "end": v(-58.66, -19.5) * mm});
            skLineSegment(sketch, "E7.7.19.4", {"start": v(-57.66, -20.5) * mm, "end": v(-57.66, -19.5) * mm});
            skLineSegment(sketch, "E7.7.20.0", {"start": v(-57.66, -19) * mm, "end": v(-58.66, -19) * mm});
            skLineSegment(sketch, "E7.7.20.1", {"start": v(-57.66, -18) * mm, "end": v(-58.66, -18) * mm});
            skLineSegment(sketch, "E7.7.20.2", {"start": v(-58.66, -19) * mm, "end": v(-57.66, -19) * mm});
            skLineSegment(sketch, "E7.7.20.3", {"start": v(-58.66, -19) * mm, "end": v(-58.66, -18) * mm});
            skLineSegment(sketch, "E7.7.20.4", {"start": v(-57.66, -19) * mm, "end": v(-57.66, -18) * mm});
            skLineSegment(sketch, "E7.7.21.0", {"start": v(-57.67, -17.5) * mm, "end": v(-58.67, -17.5) * mm});
            skLineSegment(sketch, "E7.7.21.1", {"start": v(-57.67, -16.5) * mm, "end": v(-58.67, -16.5) * mm});
            skLineSegment(sketch, "E7.7.21.2", {"start": v(-58.67, -17.5) * mm, "end": v(-57.67, -17.5) * mm});
            skLineSegment(sketch, "E7.7.21.3", {"start": v(-58.67, -17.5) * mm, "end": v(-58.67, -16.5) * mm});
            skLineSegment(sketch, "E7.7.21.4", {"start": v(-57.67, -17.5) * mm, "end": v(-57.67, -16.5) * mm});
            skLineSegment(sketch, "E7.7.22.0", {"start": v(-57.68, -16) * mm, "end": v(-58.68, -16) * mm});
            skLineSegment(sketch, "E7.7.22.1", {"start": v(-57.68, -15) * mm, "end": v(-58.68, -15) * mm});
            skLineSegment(sketch, "E7.7.22.2", {"start": v(-58.68, -16) * mm, "end": v(-57.68, -16) * mm});
            skLineSegment(sketch, "E7.7.22.3", {"start": v(-58.68, -16) * mm, "end": v(-58.68, -15) * mm});
            skLineSegment(sketch, "E7.7.22.4", {"start": v(-57.68, -16) * mm, "end": v(-57.68, -15) * mm});
            skLineSegment(sketch, "E7.7.23.0", {"start": v(-57.69, -14.5) * mm, "end": v(-58.69, -14.5) * mm});
            skLineSegment(sketch, "E7.7.23.1", {"start": v(-57.69, -13.5) * mm, "end": v(-58.69, -13.5) * mm});
            skLineSegment(sketch, "E7.7.23.2", {"start": v(-58.69, -14.5) * mm, "end": v(-57.69, -14.5) * mm});
            skLineSegment(sketch, "E7.7.23.3", {"start": v(-58.69, -14.5) * mm, "end": v(-58.69, -13.5) * mm});
            skLineSegment(sketch, "E7.7.23.4", {"start": v(-57.69, -14.5) * mm, "end": v(-57.69, -13.5) * mm});
            skLineSegment(sketch, "E7.7.24.0", {"start": v(-57.7, -13) * mm, "end": v(-58.7, -13) * mm});
            skLineSegment(sketch, "E7.7.24.1", {"start": v(-57.7, -12) * mm, "end": v(-58.7, -12) * mm});
            skLineSegment(sketch, "E7.7.24.2", {"start": v(-58.7, -13) * mm, "end": v(-57.7, -13) * mm});
            skLineSegment(sketch, "E7.7.24.3", {"start": v(-58.7, -13) * mm, "end": v(-58.7, -12) * mm});
            skLineSegment(sketch, "E7.7.24.4", {"start": v(-57.7, -13) * mm, "end": v(-57.7, -12) * mm});
            skLineSegment(sketch, "E7.7.25.0", {"start": v(-57.7, -11.5) * mm, "end": v(-58.7, -11.5) * mm});
            skLineSegment(sketch, "E7.7.25.1", {"start": v(-57.7, -10.5) * mm, "end": v(-58.7, -10.5) * mm});
            skLineSegment(sketch, "E7.7.25.2", {"start": v(-58.7, -11.5) * mm, "end": v(-57.7, -11.5) * mm});
            skLineSegment(sketch, "E7.7.25.3", {"start": v(-58.7, -11.5) * mm, "end": v(-58.7, -10.5) * mm});
            skLineSegment(sketch, "E7.7.25.4", {"start": v(-57.7, -11.5) * mm, "end": v(-57.7, -10.5) * mm});
            skLineSegment(sketch, "E7.7.26.0", {"start": v(-57.71, -10) * mm, "end": v(-58.71, -10) * mm});
            skLineSegment(sketch, "E7.7.26.1", {"start": v(-57.71, -9) * mm, "end": v(-58.71, -9) * mm});
            skLineSegment(sketch, "E7.7.26.2", {"start": v(-58.71, -10) * mm, "end": v(-57.71, -10) * mm});
            skLineSegment(sketch, "E7.7.26.3", {"start": v(-58.71, -10) * mm, "end": v(-58.71, -9) * mm});
            skLineSegment(sketch, "E7.7.26.4", {"start": v(-57.71, -10) * mm, "end": v(-57.71, -9) * mm});
            skLineSegment(sketch, "E7.7.27.0", {"start": v(-57.72, -8.5) * mm, "end": v(-58.72, -8.5) * mm});
            skLineSegment(sketch, "E7.7.27.1", {"start": v(-57.72, -7.5) * mm, "end": v(-58.72, -7.5) * mm});
            skLineSegment(sketch, "E7.7.27.2", {"start": v(-58.72, -8.5) * mm, "end": v(-57.72, -8.5) * mm});
            skLineSegment(sketch, "E7.7.27.3", {"start": v(-58.72, -8.5) * mm, "end": v(-58.72, -7.5) * mm});
            skLineSegment(sketch, "E7.7.27.4", {"start": v(-57.72, -8.5) * mm, "end": v(-57.72, -7.5) * mm});
            skLineSegment(sketch, "E7.7.28.0", {"start": v(-57.73, -7) * mm, "end": v(-58.73, -7) * mm});
            skLineSegment(sketch, "E7.7.28.1", {"start": v(-57.73, -6) * mm, "end": v(-58.73, -6) * mm});
            skLineSegment(sketch, "E7.7.28.2", {"start": v(-58.73, -7) * mm, "end": v(-57.73, -7) * mm});
            skLineSegment(sketch, "E7.7.28.3", {"start": v(-58.73, -7) * mm, "end": v(-58.73, -6) * mm});
            skLineSegment(sketch, "E7.7.28.4", {"start": v(-57.73, -7) * mm, "end": v(-57.73, -6) * mm});
            skLineSegment(sketch, "E7.7.29.0", {"start": v(-57.74, -5.5) * mm, "end": v(-58.74, -5.5) * mm});
            skLineSegment(sketch, "E7.7.29.1", {"start": v(-57.74, -4.5) * mm, "end": v(-58.74, -4.5) * mm});
            skLineSegment(sketch, "E7.7.29.2", {"start": v(-58.74, -5.5) * mm, "end": v(-57.74, -5.5) * mm});
            skLineSegment(sketch, "E7.7.29.3", {"start": v(-58.74, -5.5) * mm, "end": v(-58.74, -4.5) * mm});
            skLineSegment(sketch, "E7.7.29.4", {"start": v(-57.74, -5.5) * mm, "end": v(-57.74, -4.5) * mm});
            skLineSegment(sketch, "E7.7.30.0", {"start": v(-57.75, -4) * mm, "end": v(-58.75, -4) * mm});
            skLineSegment(sketch, "E7.7.30.1", {"start": v(-57.75, -3) * mm, "end": v(-58.75, -3) * mm});
            skLineSegment(sketch, "E7.7.30.2", {"start": v(-58.75, -4) * mm, "end": v(-57.75, -4) * mm});
            skLineSegment(sketch, "E7.7.30.3", {"start": v(-58.75, -4) * mm, "end": v(-58.75, -3) * mm});
            skLineSegment(sketch, "E7.7.30.4", {"start": v(-57.75, -4) * mm, "end": v(-57.75, -3) * mm});
            skLineSegment(sketch, "E7.8.0.0", {"start": v(-56, -49) * mm, "end": v(-57, -49) * mm});
            skLineSegment(sketch, "E7.8.0.1", {"start": v(-56, -48) * mm, "end": v(-57, -48) * mm});
            skLineSegment(sketch, "E7.8.0.2", {"start": v(-57, -49) * mm, "end": v(-56, -49) * mm});
            skLineSegment(sketch, "E7.8.0.3", {"start": v(-57, -49) * mm, "end": v(-57, -48) * mm});
            skLineSegment(sketch, "E7.8.0.4", {"start": v(-56, -49) * mm, "end": v(-56, -48) * mm});
            skLineSegment(sketch, "E7.8.1.0", {"start": v(-56, -47.5) * mm, "end": v(-57, -47.5) * mm});
            skLineSegment(sketch, "E7.8.1.1", {"start": v(-56, -46.5) * mm, "end": v(-57, -46.5) * mm});
            skLineSegment(sketch, "E7.8.1.2", {"start": v(-57, -47.5) * mm, "end": v(-56, -47.5) * mm});
            skLineSegment(sketch, "E7.8.1.3", {"start": v(-57, -47.5) * mm, "end": v(-57, -46.5) * mm});
            skLineSegment(sketch, "E7.8.1.4", {"start": v(-56, -47.5) * mm, "end": v(-56, -46.5) * mm});
            skLineSegment(sketch, "E7.8.2.0", {"start": v(-56.02, -46) * mm, "end": v(-57.02, -46) * mm});
            skLineSegment(sketch, "E7.8.2.1", {"start": v(-56.02, -45) * mm, "end": v(-57.02, -45) * mm});
            skLineSegment(sketch, "E7.8.2.2", {"start": v(-57.02, -46) * mm, "end": v(-56.02, -46) * mm});
            skLineSegment(sketch, "E7.8.2.3", {"start": v(-57.02, -46) * mm, "end": v(-57.02, -45) * mm});
            skLineSegment(sketch, "E7.8.2.4", {"start": v(-56.02, -46) * mm, "end": v(-56.02, -45) * mm});
            skLineSegment(sketch, "E7.8.3.0", {"start": v(-56.02, -44.5) * mm, "end": v(-57.02, -44.5) * mm});
            skLineSegment(sketch, "E7.8.3.1", {"start": v(-56.02, -43.5) * mm, "end": v(-57.02, -43.5) * mm});
            skLineSegment(sketch, "E7.8.3.2", {"start": v(-57.02, -44.5) * mm, "end": v(-56.02, -44.5) * mm});
            skLineSegment(sketch, "E7.8.3.3", {"start": v(-57.02, -44.5) * mm, "end": v(-57.02, -43.5) * mm});
            skLineSegment(sketch, "E7.8.3.4", {"start": v(-56.02, -44.5) * mm, "end": v(-56.02, -43.5) * mm});
            skLineSegment(sketch, "E7.8.4.0", {"start": v(-56.03, -43) * mm, "end": v(-57.03, -43) * mm});
            skLineSegment(sketch, "E7.8.4.1", {"start": v(-56.03, -42) * mm, "end": v(-57.03, -42) * mm});
            skLineSegment(sketch, "E7.8.4.2", {"start": v(-57.03, -43) * mm, "end": v(-56.03, -43) * mm});
            skLineSegment(sketch, "E7.8.4.3", {"start": v(-57.03, -43) * mm, "end": v(-57.03, -42) * mm});
            skLineSegment(sketch, "E7.8.4.4", {"start": v(-56.03, -43) * mm, "end": v(-56.03, -42) * mm});
            skLineSegment(sketch, "E7.8.5.0", {"start": v(-56.04, -41.5) * mm, "end": v(-57.04, -41.5) * mm});
            skLineSegment(sketch, "E7.8.5.1", {"start": v(-56.04, -40.5) * mm, "end": v(-57.04, -40.5) * mm});
            skLineSegment(sketch, "E7.8.5.2", {"start": v(-57.04, -41.5) * mm, "end": v(-56.04, -41.5) * mm});
            skLineSegment(sketch, "E7.8.5.3", {"start": v(-57.04, -41.5) * mm, "end": v(-57.04, -40.5) * mm});
            skLineSegment(sketch, "E7.8.5.4", {"start": v(-56.04, -41.5) * mm, "end": v(-56.04, -40.5) * mm});
            skLineSegment(sketch, "E7.8.6.0", {"start": v(-56.05, -40) * mm, "end": v(-57.05, -40) * mm});
            skLineSegment(sketch, "E7.8.6.1", {"start": v(-56.05, -39) * mm, "end": v(-57.05, -39) * mm});
            skLineSegment(sketch, "E7.8.6.2", {"start": v(-57.05, -40) * mm, "end": v(-56.05, -40) * mm});
            skLineSegment(sketch, "E7.8.6.3", {"start": v(-57.05, -40) * mm, "end": v(-57.05, -39) * mm});
            skLineSegment(sketch, "E7.8.6.4", {"start": v(-56.05, -40) * mm, "end": v(-56.05, -39) * mm});
            skLineSegment(sketch, "E7.8.7.0", {"start": v(-56.06, -38.5) * mm, "end": v(-57.06, -38.5) * mm});
            skLineSegment(sketch, "E7.8.7.1", {"start": v(-56.06, -37.5) * mm, "end": v(-57.06, -37.5) * mm});
            skLineSegment(sketch, "E7.8.7.2", {"start": v(-57.06, -38.5) * mm, "end": v(-56.06, -38.5) * mm});
            skLineSegment(sketch, "E7.8.7.3", {"start": v(-57.06, -38.5) * mm, "end": v(-57.06, -37.5) * mm});
            skLineSegment(sketch, "E7.8.7.4", {"start": v(-56.06, -38.5) * mm, "end": v(-56.06, -37.5) * mm});
            skLineSegment(sketch, "E7.8.8.0", {"start": v(-56.07, -37) * mm, "end": v(-57.07, -37) * mm});
            skLineSegment(sketch, "E7.8.8.1", {"start": v(-56.07, -36) * mm, "end": v(-57.07, -36) * mm});
            skLineSegment(sketch, "E7.8.8.2", {"start": v(-57.07, -37) * mm, "end": v(-56.07, -37) * mm});
            skLineSegment(sketch, "E7.8.8.3", {"start": v(-57.07, -37) * mm, "end": v(-57.07, -36) * mm});
            skLineSegment(sketch, "E7.8.8.4", {"start": v(-56.07, -37) * mm, "end": v(-56.07, -36) * mm});
            skLineSegment(sketch, "E7.8.9.0", {"start": v(-56.07, -35.5) * mm, "end": v(-57.07, -35.5) * mm});
            skLineSegment(sketch, "E7.8.9.1", {"start": v(-56.07, -34.5) * mm, "end": v(-57.07, -34.5) * mm});
            skLineSegment(sketch, "E7.8.9.2", {"start": v(-57.07, -35.5) * mm, "end": v(-56.07, -35.5) * mm});
            skLineSegment(sketch, "E7.8.9.3", {"start": v(-57.07, -35.5) * mm, "end": v(-57.07, -34.5) * mm});
            skLineSegment(sketch, "E7.8.9.4", {"start": v(-56.07, -35.5) * mm, "end": v(-56.07, -34.5) * mm});
            skLineSegment(sketch, "E7.8.10.0", {"start": v(-56.08, -34) * mm, "end": v(-57.08, -34) * mm});
            skLineSegment(sketch, "E7.8.10.1", {"start": v(-56.08, -33) * mm, "end": v(-57.08, -33) * mm});
            skLineSegment(sketch, "E7.8.10.2", {"start": v(-57.08, -34) * mm, "end": v(-56.08, -34) * mm});
            skLineSegment(sketch, "E7.8.10.3", {"start": v(-57.08, -34) * mm, "end": v(-57.08, -33) * mm});
            skLineSegment(sketch, "E7.8.10.4", {"start": v(-56.08, -34) * mm, "end": v(-56.08, -33) * mm});
            skLineSegment(sketch, "E7.8.11.0", {"start": v(-56.1, -32.5) * mm, "end": v(-57.1, -32.5) * mm});
            skLineSegment(sketch, "E7.8.11.1", {"start": v(-56.1, -31.5) * mm, "end": v(-57.1, -31.5) * mm});
            skLineSegment(sketch, "E7.8.11.2", {"start": v(-57.1, -32.5) * mm, "end": v(-56.1, -32.5) * mm});
            skLineSegment(sketch, "E7.8.11.3", {"start": v(-57.1, -32.5) * mm, "end": v(-57.1, -31.5) * mm});
            skLineSegment(sketch, "E7.8.11.4", {"start": v(-56.1, -32.5) * mm, "end": v(-56.1, -31.5) * mm});
            skLineSegment(sketch, "E7.8.12.0", {"start": v(-56.1, -31) * mm, "end": v(-57.1, -31) * mm});
            skLineSegment(sketch, "E7.8.12.1", {"start": v(-56.1, -30) * mm, "end": v(-57.1, -30) * mm});
            skLineSegment(sketch, "E7.8.12.2", {"start": v(-57.1, -31) * mm, "end": v(-56.1, -31) * mm});
            skLineSegment(sketch, "E7.8.12.3", {"start": v(-57.1, -31) * mm, "end": v(-57.1, -30) * mm});
            skLineSegment(sketch, "E7.8.12.4", {"start": v(-56.1, -31) * mm, "end": v(-56.1, -30) * mm});
            skLineSegment(sketch, "E7.8.13.0", {"start": v(-56.1, -29.5) * mm, "end": v(-57.1, -29.5) * mm});
            skLineSegment(sketch, "E7.8.13.1", {"start": v(-56.1, -28.5) * mm, "end": v(-57.1, -28.5) * mm});
            skLineSegment(sketch, "E7.8.13.2", {"start": v(-57.1, -29.5) * mm, "end": v(-56.1, -29.5) * mm});
            skLineSegment(sketch, "E7.8.13.3", {"start": v(-57.1, -29.5) * mm, "end": v(-57.1, -28.5) * mm});
            skLineSegment(sketch, "E7.8.13.4", {"start": v(-56.1, -29.5) * mm, "end": v(-56.1, -28.5) * mm});
            skLineSegment(sketch, "E7.8.14.0", {"start": v(-56.11, -28) * mm, "end": v(-57.11, -28) * mm});
            skLineSegment(sketch, "E7.8.14.1", {"start": v(-56.11, -27) * mm, "end": v(-57.11, -27) * mm});
            skLineSegment(sketch, "E7.8.14.2", {"start": v(-57.11, -28) * mm, "end": v(-56.11, -28) * mm});
            skLineSegment(sketch, "E7.8.14.3", {"start": v(-57.11, -28) * mm, "end": v(-57.11, -27) * mm});
            skLineSegment(sketch, "E7.8.14.4", {"start": v(-56.11, -28) * mm, "end": v(-56.11, -27) * mm});
            skLineSegment(sketch, "E7.8.15.0", {"start": v(-56.12, -26.5) * mm, "end": v(-57.12, -26.5) * mm});
            skLineSegment(sketch, "E7.8.15.1", {"start": v(-56.12, -25.5) * mm, "end": v(-57.12, -25.5) * mm});
            skLineSegment(sketch, "E7.8.15.2", {"start": v(-57.12, -26.5) * mm, "end": v(-56.12, -26.5) * mm});
            skLineSegment(sketch, "E7.8.15.3", {"start": v(-57.12, -26.5) * mm, "end": v(-57.12, -25.5) * mm});
            skLineSegment(sketch, "E7.8.15.4", {"start": v(-56.12, -26.5) * mm, "end": v(-56.12, -25.5) * mm});
            skLineSegment(sketch, "E7.8.16.0", {"start": v(-56.13, -25) * mm, "end": v(-57.13, -25) * mm});
            skLineSegment(sketch, "E7.8.16.1", {"start": v(-56.13, -24) * mm, "end": v(-57.13, -24) * mm});
            skLineSegment(sketch, "E7.8.16.2", {"start": v(-57.13, -25) * mm, "end": v(-56.13, -25) * mm});
            skLineSegment(sketch, "E7.8.16.3", {"start": v(-57.13, -25) * mm, "end": v(-57.13, -24) * mm});
            skLineSegment(sketch, "E7.8.16.4", {"start": v(-56.13, -25) * mm, "end": v(-56.13, -24) * mm});
            skLineSegment(sketch, "E7.8.17.0", {"start": v(-56.14, -23.5) * mm, "end": v(-57.14, -23.5) * mm});
            skLineSegment(sketch, "E7.8.17.1", {"start": v(-56.14, -22.5) * mm, "end": v(-57.14, -22.5) * mm});
            skLineSegment(sketch, "E7.8.17.2", {"start": v(-57.14, -23.5) * mm, "end": v(-56.14, -23.5) * mm});
            skLineSegment(sketch, "E7.8.17.3", {"start": v(-57.14, -23.5) * mm, "end": v(-57.14, -22.5) * mm});
            skLineSegment(sketch, "E7.8.17.4", {"start": v(-56.14, -23.5) * mm, "end": v(-56.14, -22.5) * mm});
            skLineSegment(sketch, "E7.8.18.0", {"start": v(-56.15, -22) * mm, "end": v(-57.15, -22) * mm});
            skLineSegment(sketch, "E7.8.18.1", {"start": v(-56.15, -21) * mm, "end": v(-57.15, -21) * mm});
            skLineSegment(sketch, "E7.8.18.2", {"start": v(-57.15, -22) * mm, "end": v(-56.15, -22) * mm});
            skLineSegment(sketch, "E7.8.18.3", {"start": v(-57.15, -22) * mm, "end": v(-57.15, -21) * mm});
            skLineSegment(sketch, "E7.8.18.4", {"start": v(-56.15, -22) * mm, "end": v(-56.15, -21) * mm});
            skLineSegment(sketch, "E7.8.19.0", {"start": v(-56.16, -20.5) * mm, "end": v(-57.16, -20.5) * mm});
            skLineSegment(sketch, "E7.8.19.1", {"start": v(-56.16, -19.5) * mm, "end": v(-57.16, -19.5) * mm});
            skLineSegment(sketch, "E7.8.19.2", {"start": v(-57.16, -20.5) * mm, "end": v(-56.16, -20.5) * mm});
            skLineSegment(sketch, "E7.8.19.3", {"start": v(-57.16, -20.5) * mm, "end": v(-57.16, -19.5) * mm});
            skLineSegment(sketch, "E7.8.19.4", {"start": v(-56.16, -20.5) * mm, "end": v(-56.16, -19.5) * mm});
            skLineSegment(sketch, "E7.8.20.0", {"start": v(-56.16, -19) * mm, "end": v(-57.16, -19) * mm});
            skLineSegment(sketch, "E7.8.20.1", {"start": v(-56.16, -18) * mm, "end": v(-57.16, -18) * mm});
            skLineSegment(sketch, "E7.8.20.2", {"start": v(-57.16, -19) * mm, "end": v(-56.16, -19) * mm});
            skLineSegment(sketch, "E7.8.20.3", {"start": v(-57.16, -19) * mm, "end": v(-57.16, -18) * mm});
            skLineSegment(sketch, "E7.8.20.4", {"start": v(-56.16, -19) * mm, "end": v(-56.16, -18) * mm});
            skLineSegment(sketch, "E7.8.21.0", {"start": v(-56.17, -17.5) * mm, "end": v(-57.17, -17.5) * mm});
            skLineSegment(sketch, "E7.8.21.1", {"start": v(-56.17, -16.5) * mm, "end": v(-57.17, -16.5) * mm});
            skLineSegment(sketch, "E7.8.21.2", {"start": v(-57.17, -17.5) * mm, "end": v(-56.17, -17.5) * mm});
            skLineSegment(sketch, "E7.8.21.3", {"start": v(-57.17, -17.5) * mm, "end": v(-57.17, -16.5) * mm});
            skLineSegment(sketch, "E7.8.21.4", {"start": v(-56.17, -17.5) * mm, "end": v(-56.17, -16.5) * mm});
            skLineSegment(sketch, "E7.8.22.0", {"start": v(-56.18, -16) * mm, "end": v(-57.18, -16) * mm});
            skLineSegment(sketch, "E7.8.22.1", {"start": v(-56.18, -15) * mm, "end": v(-57.18, -15) * mm});
            skLineSegment(sketch, "E7.8.22.2", {"start": v(-57.18, -16) * mm, "end": v(-56.18, -16) * mm});
            skLineSegment(sketch, "E7.8.22.3", {"start": v(-57.18, -16) * mm, "end": v(-57.18, -15) * mm});
            skLineSegment(sketch, "E7.8.22.4", {"start": v(-56.18, -16) * mm, "end": v(-56.18, -15) * mm});
            skLineSegment(sketch, "E7.8.23.0", {"start": v(-56.19, -14.5) * mm, "end": v(-57.19, -14.5) * mm});
            skLineSegment(sketch, "E7.8.23.1", {"start": v(-56.19, -13.5) * mm, "end": v(-57.19, -13.5) * mm});
            skLineSegment(sketch, "E7.8.23.2", {"start": v(-57.19, -14.5) * mm, "end": v(-56.19, -14.5) * mm});
            skLineSegment(sketch, "E7.8.23.3", {"start": v(-57.19, -14.5) * mm, "end": v(-57.19, -13.5) * mm});
            skLineSegment(sketch, "E7.8.23.4", {"start": v(-56.19, -14.5) * mm, "end": v(-56.19, -13.5) * mm});
            skLineSegment(sketch, "E7.8.24.0", {"start": v(-56.2, -13) * mm, "end": v(-57.2, -13) * mm});
            skLineSegment(sketch, "E7.8.24.1", {"start": v(-56.2, -12) * mm, "end": v(-57.2, -12) * mm});
            skLineSegment(sketch, "E7.8.24.2", {"start": v(-57.2, -13) * mm, "end": v(-56.2, -13) * mm});
            skLineSegment(sketch, "E7.8.24.3", {"start": v(-57.2, -13) * mm, "end": v(-57.2, -12) * mm});
            skLineSegment(sketch, "E7.8.24.4", {"start": v(-56.2, -13) * mm, "end": v(-56.2, -12) * mm});
            skLineSegment(sketch, "E7.8.25.0", {"start": v(-56.2, -11.5) * mm, "end": v(-57.2, -11.5) * mm});
            skLineSegment(sketch, "E7.8.25.1", {"start": v(-56.2, -10.5) * mm, "end": v(-57.2, -10.5) * mm});
            skLineSegment(sketch, "E7.8.25.2", {"start": v(-57.2, -11.5) * mm, "end": v(-56.2, -11.5) * mm});
            skLineSegment(sketch, "E7.8.25.3", {"start": v(-57.2, -11.5) * mm, "end": v(-57.2, -10.5) * mm});
            skLineSegment(sketch, "E7.8.25.4", {"start": v(-56.2, -11.5) * mm, "end": v(-56.2, -10.5) * mm});
            skLineSegment(sketch, "E7.8.26.0", {"start": v(-56.21, -10) * mm, "end": v(-57.21, -10) * mm});
            skLineSegment(sketch, "E7.8.26.1", {"start": v(-56.21, -9) * mm, "end": v(-57.21, -9) * mm});
            skLineSegment(sketch, "E7.8.26.2", {"start": v(-57.21, -10) * mm, "end": v(-56.21, -10) * mm});
            skLineSegment(sketch, "E7.8.26.3", {"start": v(-57.21, -10) * mm, "end": v(-57.21, -9) * mm});
            skLineSegment(sketch, "E7.8.26.4", {"start": v(-56.21, -10) * mm, "end": v(-56.21, -9) * mm});
            skLineSegment(sketch, "E7.8.27.0", {"start": v(-56.22, -8.5) * mm, "end": v(-57.22, -8.5) * mm});
            skLineSegment(sketch, "E7.8.27.1", {"start": v(-56.22, -7.5) * mm, "end": v(-57.22, -7.5) * mm});
            skLineSegment(sketch, "E7.8.27.2", {"start": v(-57.22, -8.5) * mm, "end": v(-56.22, -8.5) * mm});
            skLineSegment(sketch, "E7.8.27.3", {"start": v(-57.22, -8.5) * mm, "end": v(-57.22, -7.5) * mm});
            skLineSegment(sketch, "E7.8.27.4", {"start": v(-56.22, -8.5) * mm, "end": v(-56.22, -7.5) * mm});
            skLineSegment(sketch, "E7.8.28.0", {"start": v(-56.23, -7) * mm, "end": v(-57.23, -7) * mm});
            skLineSegment(sketch, "E7.8.28.1", {"start": v(-56.23, -6) * mm, "end": v(-57.23, -6) * mm});
            skLineSegment(sketch, "E7.8.28.2", {"start": v(-57.23, -7) * mm, "end": v(-56.23, -7) * mm});
            skLineSegment(sketch, "E7.8.28.3", {"start": v(-57.23, -7) * mm, "end": v(-57.23, -6) * mm});
            skLineSegment(sketch, "E7.8.28.4", {"start": v(-56.23, -7) * mm, "end": v(-56.23, -6) * mm});
            skLineSegment(sketch, "E7.8.29.0", {"start": v(-56.24, -5.5) * mm, "end": v(-57.24, -5.5) * mm});
            skLineSegment(sketch, "E7.8.29.1", {"start": v(-56.24, -4.5) * mm, "end": v(-57.24, -4.5) * mm});
            skLineSegment(sketch, "E7.8.29.2", {"start": v(-57.24, -5.5) * mm, "end": v(-56.24, -5.5) * mm});
            skLineSegment(sketch, "E7.8.29.3", {"start": v(-57.24, -5.5) * mm, "end": v(-57.24, -4.5) * mm});
            skLineSegment(sketch, "E7.8.29.4", {"start": v(-56.24, -5.5) * mm, "end": v(-56.24, -4.5) * mm});
            skLineSegment(sketch, "E7.8.30.0", {"start": v(-56.25, -4) * mm, "end": v(-57.25, -4) * mm});
            skLineSegment(sketch, "E7.8.30.1", {"start": v(-56.25, -3) * mm, "end": v(-57.25, -3) * mm});
            skLineSegment(sketch, "E7.8.30.2", {"start": v(-57.25, -4) * mm, "end": v(-56.25, -4) * mm});
            skLineSegment(sketch, "E7.8.30.3", {"start": v(-57.25, -4) * mm, "end": v(-57.25, -3) * mm});
            skLineSegment(sketch, "E7.8.30.4", {"start": v(-56.25, -4) * mm, "end": v(-56.25, -3) * mm});
            skLineSegment(sketch, "E7.9.0.0", {"start": v(-54.5, -49) * mm, "end": v(-55.5, -49) * mm});
            skLineSegment(sketch, "E7.9.0.1", {"start": v(-54.5, -48) * mm, "end": v(-55.5, -48) * mm});
            skLineSegment(sketch, "E7.9.0.2", {"start": v(-55.5, -49) * mm, "end": v(-54.5, -49) * mm});
            skLineSegment(sketch, "E7.9.0.3", {"start": v(-55.5, -49) * mm, "end": v(-55.5, -48) * mm});
            skLineSegment(sketch, "E7.9.0.4", {"start": v(-54.5, -49) * mm, "end": v(-54.5, -48) * mm});
            skLineSegment(sketch, "E7.9.1.0", {"start": v(-54.5, -47.5) * mm, "end": v(-55.5, -47.5) * mm});
            skLineSegment(sketch, "E7.9.1.1", {"start": v(-54.5, -46.5) * mm, "end": v(-55.5, -46.5) * mm});
            skLineSegment(sketch, "E7.9.1.2", {"start": v(-55.5, -47.5) * mm, "end": v(-54.5, -47.5) * mm});
            skLineSegment(sketch, "E7.9.1.3", {"start": v(-55.5, -47.5) * mm, "end": v(-55.5, -46.5) * mm});
            skLineSegment(sketch, "E7.9.1.4", {"start": v(-54.5, -47.5) * mm, "end": v(-54.5, -46.5) * mm});
            skLineSegment(sketch, "E7.9.2.0", {"start": v(-54.52, -46) * mm, "end": v(-55.52, -46) * mm});
            skLineSegment(sketch, "E7.9.2.1", {"start": v(-54.52, -45) * mm, "end": v(-55.52, -45) * mm});
            skLineSegment(sketch, "E7.9.2.2", {"start": v(-55.52, -46) * mm, "end": v(-54.52, -46) * mm});
            skLineSegment(sketch, "E7.9.2.3", {"start": v(-55.52, -46) * mm, "end": v(-55.52, -45) * mm});
            skLineSegment(sketch, "E7.9.2.4", {"start": v(-54.52, -46) * mm, "end": v(-54.52, -45) * mm});
            skLineSegment(sketch, "E7.9.3.0", {"start": v(-54.52, -44.5) * mm, "end": v(-55.52, -44.5) * mm});
            skLineSegment(sketch, "E7.9.3.1", {"start": v(-54.52, -43.5) * mm, "end": v(-55.52, -43.5) * mm});
            skLineSegment(sketch, "E7.9.3.2", {"start": v(-55.52, -44.5) * mm, "end": v(-54.52, -44.5) * mm});
            skLineSegment(sketch, "E7.9.3.3", {"start": v(-55.52, -44.5) * mm, "end": v(-55.52, -43.5) * mm});
            skLineSegment(sketch, "E7.9.3.4", {"start": v(-54.52, -44.5) * mm, "end": v(-54.52, -43.5) * mm});
            skLineSegment(sketch, "E7.9.4.0", {"start": v(-54.53, -43) * mm, "end": v(-55.53, -43) * mm});
            skLineSegment(sketch, "E7.9.4.1", {"start": v(-54.53, -42) * mm, "end": v(-55.53, -42) * mm});
            skLineSegment(sketch, "E7.9.4.2", {"start": v(-55.53, -43) * mm, "end": v(-54.53, -43) * mm});
            skLineSegment(sketch, "E7.9.4.3", {"start": v(-55.53, -43) * mm, "end": v(-55.53, -42) * mm});
            skLineSegment(sketch, "E7.9.4.4", {"start": v(-54.53, -43) * mm, "end": v(-54.53, -42) * mm});
            skLineSegment(sketch, "E7.9.5.0", {"start": v(-54.54, -41.5) * mm, "end": v(-55.54, -41.5) * mm});
            skLineSegment(sketch, "E7.9.5.1", {"start": v(-54.54, -40.5) * mm, "end": v(-55.54, -40.5) * mm});
            skLineSegment(sketch, "E7.9.5.2", {"start": v(-55.54, -41.5) * mm, "end": v(-54.54, -41.5) * mm});
            skLineSegment(sketch, "E7.9.5.3", {"start": v(-55.54, -41.5) * mm, "end": v(-55.54, -40.5) * mm});
            skLineSegment(sketch, "E7.9.5.4", {"start": v(-54.54, -41.5) * mm, "end": v(-54.54, -40.5) * mm});
            skLineSegment(sketch, "E7.9.6.0", {"start": v(-54.55, -40) * mm, "end": v(-55.55, -40) * mm});
            skLineSegment(sketch, "E7.9.6.1", {"start": v(-54.55, -39) * mm, "end": v(-55.55, -39) * mm});
            skLineSegment(sketch, "E7.9.6.2", {"start": v(-55.55, -40) * mm, "end": v(-54.55, -40) * mm});
            skLineSegment(sketch, "E7.9.6.3", {"start": v(-55.55, -40) * mm, "end": v(-55.55, -39) * mm});
            skLineSegment(sketch, "E7.9.6.4", {"start": v(-54.55, -40) * mm, "end": v(-54.55, -39) * mm});
            skLineSegment(sketch, "E7.9.7.0", {"start": v(-54.56, -38.5) * mm, "end": v(-55.56, -38.5) * mm});
            skLineSegment(sketch, "E7.9.7.1", {"start": v(-54.56, -37.5) * mm, "end": v(-55.56, -37.5) * mm});
            skLineSegment(sketch, "E7.9.7.2", {"start": v(-55.56, -38.5) * mm, "end": v(-54.56, -38.5) * mm});
            skLineSegment(sketch, "E7.9.7.3", {"start": v(-55.56, -38.5) * mm, "end": v(-55.56, -37.5) * mm});
            skLineSegment(sketch, "E7.9.7.4", {"start": v(-54.56, -38.5) * mm, "end": v(-54.56, -37.5) * mm});
            skLineSegment(sketch, "E7.9.8.0", {"start": v(-54.57, -37) * mm, "end": v(-55.57, -37) * mm});
            skLineSegment(sketch, "E7.9.8.1", {"start": v(-54.57, -36) * mm, "end": v(-55.57, -36) * mm});
            skLineSegment(sketch, "E7.9.8.2", {"start": v(-55.57, -37) * mm, "end": v(-54.57, -37) * mm});
            skLineSegment(sketch, "E7.9.8.3", {"start": v(-55.57, -37) * mm, "end": v(-55.57, -36) * mm});
            skLineSegment(sketch, "E7.9.8.4", {"start": v(-54.57, -37) * mm, "end": v(-54.57, -36) * mm});
            skLineSegment(sketch, "E7.9.9.0", {"start": v(-54.57, -35.5) * mm, "end": v(-55.57, -35.5) * mm});
            skLineSegment(sketch, "E7.9.9.1", {"start": v(-54.57, -34.5) * mm, "end": v(-55.57, -34.5) * mm});
            skLineSegment(sketch, "E7.9.9.2", {"start": v(-55.57, -35.5) * mm, "end": v(-54.57, -35.5) * mm});
            skLineSegment(sketch, "E7.9.9.3", {"start": v(-55.57, -35.5) * mm, "end": v(-55.57, -34.5) * mm});
            skLineSegment(sketch, "E7.9.9.4", {"start": v(-54.57, -35.5) * mm, "end": v(-54.57, -34.5) * mm});
            skLineSegment(sketch, "E7.9.10.0", {"start": v(-54.58, -34) * mm, "end": v(-55.58, -34) * mm});
            skLineSegment(sketch, "E7.9.10.1", {"start": v(-54.58, -33) * mm, "end": v(-55.58, -33) * mm});
            skLineSegment(sketch, "E7.9.10.2", {"start": v(-55.58, -34) * mm, "end": v(-54.58, -34) * mm});
            skLineSegment(sketch, "E7.9.10.3", {"start": v(-55.58, -34) * mm, "end": v(-55.58, -33) * mm});
            skLineSegment(sketch, "E7.9.10.4", {"start": v(-54.58, -34) * mm, "end": v(-54.58, -33) * mm});
            skLineSegment(sketch, "E7.9.11.0", {"start": v(-54.6, -32.5) * mm, "end": v(-55.6, -32.5) * mm});
            skLineSegment(sketch, "E7.9.11.1", {"start": v(-54.6, -31.5) * mm, "end": v(-55.6, -31.5) * mm});
            skLineSegment(sketch, "E7.9.11.2", {"start": v(-55.6, -32.5) * mm, "end": v(-54.6, -32.5) * mm});
            skLineSegment(sketch, "E7.9.11.3", {"start": v(-55.6, -32.5) * mm, "end": v(-55.6, -31.5) * mm});
            skLineSegment(sketch, "E7.9.11.4", {"start": v(-54.6, -32.5) * mm, "end": v(-54.6, -31.5) * mm});
            skLineSegment(sketch, "E7.9.12.0", {"start": v(-54.6, -31) * mm, "end": v(-55.6, -31) * mm});
            skLineSegment(sketch, "E7.9.12.1", {"start": v(-54.6, -30) * mm, "end": v(-55.6, -30) * mm});
            skLineSegment(sketch, "E7.9.12.2", {"start": v(-55.6, -31) * mm, "end": v(-54.6, -31) * mm});
            skLineSegment(sketch, "E7.9.12.3", {"start": v(-55.6, -31) * mm, "end": v(-55.6, -30) * mm});
            skLineSegment(sketch, "E7.9.12.4", {"start": v(-54.6, -31) * mm, "end": v(-54.6, -30) * mm});
            skLineSegment(sketch, "E7.9.13.0", {"start": v(-54.6, -29.5) * mm, "end": v(-55.6, -29.5) * mm});
            skLineSegment(sketch, "E7.9.13.1", {"start": v(-54.6, -28.5) * mm, "end": v(-55.6, -28.5) * mm});
            skLineSegment(sketch, "E7.9.13.2", {"start": v(-55.6, -29.5) * mm, "end": v(-54.6, -29.5) * mm});
            skLineSegment(sketch, "E7.9.13.3", {"start": v(-55.6, -29.5) * mm, "end": v(-55.6, -28.5) * mm});
            skLineSegment(sketch, "E7.9.13.4", {"start": v(-54.6, -29.5) * mm, "end": v(-54.6, -28.5) * mm});
            skLineSegment(sketch, "E7.9.14.0", {"start": v(-54.61, -28) * mm, "end": v(-55.61, -28) * mm});
            skLineSegment(sketch, "E7.9.14.1", {"start": v(-54.61, -27) * mm, "end": v(-55.61, -27) * mm});
            skLineSegment(sketch, "E7.9.14.2", {"start": v(-55.61, -28) * mm, "end": v(-54.61, -28) * mm});
            skLineSegment(sketch, "E7.9.14.3", {"start": v(-55.61, -28) * mm, "end": v(-55.61, -27) * mm});
            skLineSegment(sketch, "E7.9.14.4", {"start": v(-54.61, -28) * mm, "end": v(-54.61, -27) * mm});
            skLineSegment(sketch, "E7.9.15.0", {"start": v(-54.62, -26.5) * mm, "end": v(-55.62, -26.5) * mm});
            skLineSegment(sketch, "E7.9.15.1", {"start": v(-54.62, -25.5) * mm, "end": v(-55.62, -25.5) * mm});
            skLineSegment(sketch, "E7.9.15.2", {"start": v(-55.62, -26.5) * mm, "end": v(-54.62, -26.5) * mm});
            skLineSegment(sketch, "E7.9.15.3", {"start": v(-55.62, -26.5) * mm, "end": v(-55.62, -25.5) * mm});
            skLineSegment(sketch, "E7.9.15.4", {"start": v(-54.62, -26.5) * mm, "end": v(-54.62, -25.5) * mm});
            skLineSegment(sketch, "E7.9.16.0", {"start": v(-54.63, -25) * mm, "end": v(-55.63, -25) * mm});
            skLineSegment(sketch, "E7.9.16.1", {"start": v(-54.63, -24) * mm, "end": v(-55.63, -24) * mm});
            skLineSegment(sketch, "E7.9.16.2", {"start": v(-55.63, -25) * mm, "end": v(-54.63, -25) * mm});
            skLineSegment(sketch, "E7.9.16.3", {"start": v(-55.63, -25) * mm, "end": v(-55.63, -24) * mm});
            skLineSegment(sketch, "E7.9.16.4", {"start": v(-54.63, -25) * mm, "end": v(-54.63, -24) * mm});
            skLineSegment(sketch, "E7.9.17.0", {"start": v(-54.64, -23.5) * mm, "end": v(-55.64, -23.5) * mm});
            skLineSegment(sketch, "E7.9.17.1", {"start": v(-54.64, -22.5) * mm, "end": v(-55.64, -22.5) * mm});
            skLineSegment(sketch, "E7.9.17.2", {"start": v(-55.64, -23.5) * mm, "end": v(-54.64, -23.5) * mm});
            skLineSegment(sketch, "E7.9.17.3", {"start": v(-55.64, -23.5) * mm, "end": v(-55.64, -22.5) * mm});
            skLineSegment(sketch, "E7.9.17.4", {"start": v(-54.64, -23.5) * mm, "end": v(-54.64, -22.5) * mm});
            skLineSegment(sketch, "E7.9.18.0", {"start": v(-54.65, -22) * mm, "end": v(-55.65, -22) * mm});
            skLineSegment(sketch, "E7.9.18.1", {"start": v(-54.65, -21) * mm, "end": v(-55.65, -21) * mm});
            skLineSegment(sketch, "E7.9.18.2", {"start": v(-55.65, -22) * mm, "end": v(-54.65, -22) * mm});
            skLineSegment(sketch, "E7.9.18.3", {"start": v(-55.65, -22) * mm, "end": v(-55.65, -21) * mm});
            skLineSegment(sketch, "E7.9.18.4", {"start": v(-54.65, -22) * mm, "end": v(-54.65, -21) * mm});
            skLineSegment(sketch, "E7.9.19.0", {"start": v(-54.66, -20.5) * mm, "end": v(-55.66, -20.5) * mm});
            skLineSegment(sketch, "E7.9.19.1", {"start": v(-54.66, -19.5) * mm, "end": v(-55.66, -19.5) * mm});
            skLineSegment(sketch, "E7.9.19.2", {"start": v(-55.66, -20.5) * mm, "end": v(-54.66, -20.5) * mm});
            skLineSegment(sketch, "E7.9.19.3", {"start": v(-55.66, -20.5) * mm, "end": v(-55.66, -19.5) * mm});
            skLineSegment(sketch, "E7.9.19.4", {"start": v(-54.66, -20.5) * mm, "end": v(-54.66, -19.5) * mm});
            skLineSegment(sketch, "E7.9.20.0", {"start": v(-54.66, -19) * mm, "end": v(-55.66, -19) * mm});
            skLineSegment(sketch, "E7.9.20.1", {"start": v(-54.66, -18) * mm, "end": v(-55.66, -18) * mm});
            skLineSegment(sketch, "E7.9.20.2", {"start": v(-55.66, -19) * mm, "end": v(-54.66, -19) * mm});
            skLineSegment(sketch, "E7.9.20.3", {"start": v(-55.66, -19) * mm, "end": v(-55.66, -18) * mm});
            skLineSegment(sketch, "E7.9.20.4", {"start": v(-54.66, -19) * mm, "end": v(-54.66, -18) * mm});
            skLineSegment(sketch, "E7.9.21.0", {"start": v(-54.67, -17.5) * mm, "end": v(-55.67, -17.5) * mm});
            skLineSegment(sketch, "E7.9.21.1", {"start": v(-54.67, -16.5) * mm, "end": v(-55.67, -16.5) * mm});
            skLineSegment(sketch, "E7.9.21.2", {"start": v(-55.67, -17.5) * mm, "end": v(-54.67, -17.5) * mm});
            skLineSegment(sketch, "E7.9.21.3", {"start": v(-55.67, -17.5) * mm, "end": v(-55.67, -16.5) * mm});
            skLineSegment(sketch, "E7.9.21.4", {"start": v(-54.67, -17.5) * mm, "end": v(-54.67, -16.5) * mm});
            skLineSegment(sketch, "E7.9.22.0", {"start": v(-54.68, -16) * mm, "end": v(-55.68, -16) * mm});
            skLineSegment(sketch, "E7.9.22.1", {"start": v(-54.68, -15) * mm, "end": v(-55.68, -15) * mm});
            skLineSegment(sketch, "E7.9.22.2", {"start": v(-55.68, -16) * mm, "end": v(-54.68, -16) * mm});
            skLineSegment(sketch, "E7.9.22.3", {"start": v(-55.68, -16) * mm, "end": v(-55.68, -15) * mm});
            skLineSegment(sketch, "E7.9.22.4", {"start": v(-54.68, -16) * mm, "end": v(-54.68, -15) * mm});
            skLineSegment(sketch, "E7.9.23.0", {"start": v(-54.69, -14.5) * mm, "end": v(-55.69, -14.5) * mm});
            skLineSegment(sketch, "E7.9.23.1", {"start": v(-54.69, -13.5) * mm, "end": v(-55.69, -13.5) * mm});
            skLineSegment(sketch, "E7.9.23.2", {"start": v(-55.69, -14.5) * mm, "end": v(-54.69, -14.5) * mm});
            skLineSegment(sketch, "E7.9.23.3", {"start": v(-55.69, -14.5) * mm, "end": v(-55.69, -13.5) * mm});
            skLineSegment(sketch, "E7.9.23.4", {"start": v(-54.69, -14.5) * mm, "end": v(-54.69, -13.5) * mm});
            skLineSegment(sketch, "E7.9.24.0", {"start": v(-54.7, -13) * mm, "end": v(-55.7, -13) * mm});
            skLineSegment(sketch, "E7.9.24.1", {"start": v(-54.7, -12) * mm, "end": v(-55.7, -12) * mm});
            skLineSegment(sketch, "E7.9.24.2", {"start": v(-55.7, -13) * mm, "end": v(-54.7, -13) * mm});
            skLineSegment(sketch, "E7.9.24.3", {"start": v(-55.7, -13) * mm, "end": v(-55.7, -12) * mm});
            skLineSegment(sketch, "E7.9.24.4", {"start": v(-54.7, -13) * mm, "end": v(-54.7, -12) * mm});
            skLineSegment(sketch, "E7.9.25.0", {"start": v(-54.7, -11.5) * mm, "end": v(-55.7, -11.5) * mm});
            skLineSegment(sketch, "E7.9.25.1", {"start": v(-54.7, -10.5) * mm, "end": v(-55.7, -10.5) * mm});
            skLineSegment(sketch, "E7.9.25.2", {"start": v(-55.7, -11.5) * mm, "end": v(-54.7, -11.5) * mm});
            skLineSegment(sketch, "E7.9.25.3", {"start": v(-55.7, -11.5) * mm, "end": v(-55.7, -10.5) * mm});
            skLineSegment(sketch, "E7.9.25.4", {"start": v(-54.7, -11.5) * mm, "end": v(-54.7, -10.5) * mm});
            skLineSegment(sketch, "E7.9.26.0", {"start": v(-54.71, -10) * mm, "end": v(-55.71, -10) * mm});
            skLineSegment(sketch, "E7.9.26.1", {"start": v(-54.71, -9) * mm, "end": v(-55.71, -9) * mm});
            skLineSegment(sketch, "E7.9.26.2", {"start": v(-55.71, -10) * mm, "end": v(-54.71, -10) * mm});
            skLineSegment(sketch, "E7.9.26.3", {"start": v(-55.71, -10) * mm, "end": v(-55.71, -9) * mm});
            skLineSegment(sketch, "E7.9.26.4", {"start": v(-54.71, -10) * mm, "end": v(-54.71, -9) * mm});
            skLineSegment(sketch, "E7.9.27.0", {"start": v(-54.72, -8.5) * mm, "end": v(-55.72, -8.5) * mm});
            skLineSegment(sketch, "E7.9.27.1", {"start": v(-54.72, -7.5) * mm, "end": v(-55.72, -7.5) * mm});
            skLineSegment(sketch, "E7.9.27.2", {"start": v(-55.72, -8.5) * mm, "end": v(-54.72, -8.5) * mm});
            skLineSegment(sketch, "E7.9.27.3", {"start": v(-55.72, -8.5) * mm, "end": v(-55.72, -7.5) * mm});
            skLineSegment(sketch, "E7.9.27.4", {"start": v(-54.72, -8.5) * mm, "end": v(-54.72, -7.5) * mm});
            skLineSegment(sketch, "E7.9.28.0", {"start": v(-54.73, -7) * mm, "end": v(-55.73, -7) * mm});
            skLineSegment(sketch, "E7.9.28.1", {"start": v(-54.73, -6) * mm, "end": v(-55.73, -6) * mm});
            skLineSegment(sketch, "E7.9.28.2", {"start": v(-55.73, -7) * mm, "end": v(-54.73, -7) * mm});
            skLineSegment(sketch, "E7.9.28.3", {"start": v(-55.73, -7) * mm, "end": v(-55.73, -6) * mm});
            skLineSegment(sketch, "E7.9.28.4", {"start": v(-54.73, -7) * mm, "end": v(-54.73, -6) * mm});
            skLineSegment(sketch, "E7.9.29.0", {"start": v(-54.74, -5.5) * mm, "end": v(-55.74, -5.5) * mm});
            skLineSegment(sketch, "E7.9.29.1", {"start": v(-54.74, -4.5) * mm, "end": v(-55.74, -4.5) * mm});
            skLineSegment(sketch, "E7.9.29.2", {"start": v(-55.74, -5.5) * mm, "end": v(-54.74, -5.5) * mm});
            skLineSegment(sketch, "E7.9.29.3", {"start": v(-55.74, -5.5) * mm, "end": v(-55.74, -4.5) * mm});
            skLineSegment(sketch, "E7.9.29.4", {"start": v(-54.74, -5.5) * mm, "end": v(-54.74, -4.5) * mm});
            skLineSegment(sketch, "E7.9.30.0", {"start": v(-54.75, -4) * mm, "end": v(-55.75, -4) * mm});
            skLineSegment(sketch, "E7.9.30.1", {"start": v(-54.75, -3) * mm, "end": v(-55.75, -3) * mm});
            skLineSegment(sketch, "E7.9.30.2", {"start": v(-55.75, -4) * mm, "end": v(-54.75, -4) * mm});
            skLineSegment(sketch, "E7.9.30.3", {"start": v(-55.75, -4) * mm, "end": v(-55.75, -3) * mm});
            skLineSegment(sketch, "E7.9.30.4", {"start": v(-54.75, -4) * mm, "end": v(-54.75, -3) * mm});
            skLineSegment(sketch, "E7.direction1", {"start": v(-69, -49) * mm, "end": v(-67.5, -49) * mm, "construction": true});
            skLineSegment(sketch, "E7.direction2", {"start": v(-69, -49) * mm, "end": v(-69, -47.5) * mm, "construction": true});
            skSolve(sketch);
        }
        {
            var Q0;
            Q0 = qSketchRegion(id + "F5", true);
            extrude(context, id + "F6", {"entities" : qUnion([Q0]), "operationType" : NewBodyOperationType.REMOVE, "endBound" : BoundingType.SYMMETRIC, "oppositeDirection" : true, "depth" : 25 * mm, "offsetDistance" : 25 * mm});
        }
    });
